FCSTD DOCUMENT  (FreeCAD 1.0R39285 (Git))
Label: suspendAssy_13.5m
License: All rights reserved
LicenseURL: https://en.wikipedia.org/wiki/All_rights_reserved
objects: Sketcher::SketchObject×102, Part::FeaturePython×96, Part::Extrusion×79, App::Part×45, Part::Cut×31, Part::Feature×27, Part::Compound×20, Part::Mirroring×18, Spreadsheet::Sheet×14, Part::Revolution×12, PartDesign::Body×9, Part::MultiFuse×9, Part::Sweep×8, PartDesign::Revolution×7, Part::Cylinder×5, PartDesign::Pad×4, Part::Part2DObjectPython×4, PartDesign::Pocket×3, PartDesign::ShapeBinder×3, PartDesign::PolarPattern×1, +4 more types
note: 552 computed .brp shape members not serialized (recipe doc carries the construction recipe); baked Part::Feature solids carry a one-line shape summary decoded from their .brp

FEATURE [PartDesign::Body] Body  label="ainShaftBerg"
  AllowCompound = false
  Origin = -> Origin001
FEATURE [Sketcher::SketchObject] Sketch
  ArcFitTolerance = 0
  AttachmentSupport = -> [XZ_Plane001]
  FullyConstrained = true
  MakeInternals = false
  MapMode = 5
  Placement = pos=(0,0,0) rot=(1,0,0;1.5708rad)
  sketch-geometry (6):
    g0: LineSegment StartX=0 StartY=0 StartZ=0 EndX=120 EndY=0 EndZ=0
    g1: LineSegment StartX=120 StartY=0 StartZ=0 EndX=120 EndY=16 EndZ=0
    g2: LineSegment StartX=120 StartY=16 StartZ=0 EndX=40 EndY=16 EndZ=0
    g3: LineSegment StartX=40 StartY=16 StartZ=0 EndX=40 EndY=120 EndZ=0
    g4: LineSegment StartX=40 StartY=120 StartZ=0 EndX=0 EndY=120 EndZ=0
    g5: LineSegment StartX=0 StartY=120 StartZ=0 EndX=0 EndY=0 EndZ=0
  constraints (17):
    c: Coincident(g-1,g0)
    c: Horizontal(g0)
    c: Coincident(g0,g1)
    c: Vertical(g1)
    c: Coincident(g1,g2)
    c: Horizontal(g2)
    c: Coincident(g2,g3)
    c: Vertical(g3)
    c: Coincident(g3,g4)
    c: Horizontal(g4)
    c: Coincident(g4,g5)
    c: Coincident(g5,g0)
    c: Vertical(g5)
    c: DistanceX(g4,g4) = 40
    c: DistanceY(g1,g1) = 16
    c: DistanceX(g0,g0) = 120
    c: DistanceY(g5,g5) = 120
FEATURE [PartDesign::Revolution] Revolution
  Angle = 360
  Angle2 = 60
  Axis = (0,2e-16,1)
  Base = (0,0,0)
  Placement = pos=(0,0,0) rot=(1,0,0;1.5708rad)
  Profile = -> Sketch
  ReferenceAxis = -> Sketch [V_Axis]
  Reversed = true
  Suppressed = false
  Type = 0
FEATURE [Sketcher::SketchObject] Sketch001
  ArcFitTolerance = 0
  AttachmentSupport = -> [Revolution]
  FullyConstrained = true
  MakeInternals = false
  MapMode = 5
  Placement = pos=(0,7e-15,16) rot=(0,0,1;3.14159rad)
  sketch-geometry (1):
    g0: Circle CenterX=90 CenterY=0 CenterZ=0 NormalX=0 NormalY=0 NormalZ=1 AngleXU=0 Radius=9.5
  constraints (3):
    c: PointOnObject(g0,g-1)
    c: Diameter(g0) = 19
    c: DistanceX(g-1,g0) = 90
FEATURE [Part::Extrusion] Extrude
  Base = -> Sketch001
  Dir = (0,0,1)
  DirMode = 2
  FaceMakerClass = Part::FaceMakerBullseye
  FaceMakerMode = 3
  LengthFwd = 30
  LengthRev = 0
  Reversed = true
  Solid = true
  Symmetric = false
FEATURE [Part::FeaturePython] Array  # Draft array (typed FeaturePython)
  Angle = 360
  ArrayType = 1
  Axis = (0,0,1)
  Base = -> Extrude
  Center = (0,0,0)
  Count = 4
  Fuse = false
  IntervalAxis = (0,0,0)
  IntervalX = (50,0,0)
  IntervalY = (0,50,0)
  IntervalZ = (0,0,50)
  NumberCircles = 3
  NumberPolar = 4
  NumberX = 2
  NumberY = 2
  NumberZ = 1
  RadialDistance = 50
  Symmetry = 1
  TangentialDistance = 25
FEATURE [Part::Cut] Cut
  Base = -> Revolution
  Tool = -> Array
FEATURE [App::Part] Part001  label="mainShaftBrg"
  Group = -> [Body,Extrude,Array,Revolution,Sketch001,Sketch,Cut]
  Origin = -> Origin002
  Placement = pos=(0,0,0) rot=(0,0,1;0.785398rad)
  mass = 9.64324
FEATURE [Sketcher::SketchObject] Sketch014
  ArcFitTolerance = 0
  FullyConstrained = true
  MakeInternals = false
  Placement = pos=(0,0,0) rot=(1,0,0;1.5708rad)
  expr: Constraints[11] = Spreadsheet001.dia / 2 - 460
  sketch-geometry (4):
    g0: LineSegment StartX=6285 StartY=0 StartZ=0 EndX=6290 EndY=0 EndZ=0
    g1: LineSegment StartX=6290 StartY=0 StartZ=0 EndX=6290 EndY=250 EndZ=0
    g2: LineSegment StartX=6290 StartY=250 StartZ=0 EndX=6285 EndY=250 EndZ=0
    g3: LineSegment StartX=6285 StartY=250 StartZ=0 EndX=6285 EndY=0 EndZ=0
  constraints (12):
    c: Coincident(g0,g1)
    c: Coincident(g1,g2)
    c: Coincident(g2,g3)
    c: Coincident(g3,g0)
    c: Horizontal(g0)
    c: Horizontal(g2)
    c: Vertical(g1)
    c: Vertical(g3)
    c: PointOnObject(g0,g-1)
    c: Distance(g2) = 5
    c: DistanceY(g1,g1) = 250
    c: DistanceX(g-1,g0) = 6290
FEATURE [Part::Revolution] Revolve
  Angle = 360
  Axis = (0,0,1)
  Base = (0,0,0)
  FaceMakerClass = Part::FaceMakerBullseye
  Solid = true
  Source = -> Sketch014
  Symmetric = false
FEATURE [Sketcher::SketchObject] Sketch015
  ArcFitTolerance = 0
  FullyConstrained = true
  MakeInternals = false
  Placement = pos=(0,0,0) rot=(1,0,0;1.5708rad)
  sketch-geometry (3):
    g0: LineSegment StartX=-70 StartY=250 StartZ=0 EndX=70 EndY=250 EndZ=0
    g1: LineSegment StartX=70 StartY=250 StartZ=0 EndX=0 EndY=180 EndZ=0
    g2: LineSegment StartX=0 StartY=180 StartZ=0 EndX=-70 EndY=250 EndZ=0
  constraints (9):
    c: Horizontal(g0)
    c: Coincident(g0,g1)
    c: PointOnObject(g1,g-2)
    c: Coincident(g1,g2)
    c: Coincident(g2,g0)
    c: Angle(g1,g2) = 1.5708
    c: PointOnObject(g0,g-3)
    c: DistanceY(g1,g0) = 70
    c: Angle(g2,g-2) = 2.35619
FEATURE [Part::Extrusion] Extrude006  label="Extrude007"
  Base = -> Sketch015
  Dir = (0,-1,2e-16)
  DirMode = 2
  FaceMakerClass = Part::FaceMakerBullseye
  FaceMakerMode = 3
  LengthFwd = 10000
  LengthRev = 0
  Solid = true
  Symmetric = false
FEATURE [Part::FeaturePython] Array002  # Draft array (typed FeaturePython)
  AlwaysSyncPlacement = false
  Angle = 360
  ArrayType = 1
  Axis = (0,0,1)
  Base = -> Extrude006
  Center = (0,0,0)
  Count = 245
  ExpandArray = false
  Fuse = false
  IntervalAxis = (0,0,0)
  IntervalX = (50,0,0)
  IntervalY = (0,50,0)
  IntervalZ = (0,0,50)
  NumberCircles = 3
  NumberPolar = 245
  NumberX = 2
  NumberY = 2
  NumberZ = 1
  PlacementList = 245 placements: [(0,0,0),(0,0,0),(0,0,0),(0,0,0),(0,0,0),(0,0,0),(0,0,0),(0,0,0),(0,0,0),(0,0,0),(0,0,0),(0,0,0),(0,0,0),(0,0,0),(0,0,0),(0,0,0),(0,0,0),(0,0,0),(0,0,0),(0,0,0),(0,0,0),(0,0,0),(0,0,0),(0,0,0),(0,0,0),(0,0,0),(0,0,0),(0,0,0),(0,0,0),(0,0,0),(0,0,0),(0,0,0),(0,0,0),(0,0,0),(0,0,0),(0,0,0),(0,0,0),(0,0,0),(0,0,0),(0,0,0),(0,0,0),(0,0,0),(0,0,0),(0,0,0),(0,0,0),(0,0,0),(0,0,0),(0,0,0),(0,0,0),(0,0,0),+195 more]
  RadialDistance = 50
  Symmetry = 1
  TangentialDistance = 25
  expr: NumberPolar = Spreadsheet001.dia / 55
FEATURE [Part::Cut] Cut001  label="weir"
  Base = -> Revolve
  Tool = -> Array002
FEATURE [Sketcher::SketchObject] Sketch016
  ArcFitTolerance = 0
  FullyConstrained = true
  MakeInternals = false
  Placement = pos=(0,0,0) rot=(1,0,0;1.5708rad)
  expr: .Constraints.h0 = Spreadsheet001.h0
  expr: Constraints[11] = Spreadsheet001.dia / 2 - (450 + 300)
  sketch-geometry (4):
    g0: LineSegment StartX=5995 StartY=80 StartZ=0 EndX=6000 EndY=80 EndZ=0
    g1: LineSegment StartX=6000 StartY=80 StartZ=0 EndX=6000 EndY=380 EndZ=0
    g2: LineSegment StartX=6000 StartY=380 StartZ=0 EndX=5995 EndY=380 EndZ=0
    g3: LineSegment StartX=5995 StartY=380 StartZ=0 EndX=5995 EndY=80 EndZ=0
  constraints (12):
    c: Coincident(g0,g1)
    c: Coincident(g1,g2)
    c: Coincident(g2,g3)
    c: Coincident(g3,g0)
    c: Horizontal(g0)
    c: Horizontal(g2)
    c: Vertical(g1)
    c: Vertical(g3)
    c: DistanceX(g2,g2) = 5
    c: DistanceY(g1,g1) = 300  'h0'
    c: DistanceY(g-3,g1) = 130
    c: Distance(g1,g-2) = 6000
FEATURE [Part::Revolution] Revolve001
  Angle = 360
  Axis = (0,0,1)
  Base = (0,0,0)
  FaceMakerClass = Part::FaceMakerBullseye
  Solid = true
  Source = -> Sketch016
  Symmetric = false
FEATURE [Part::FeaturePython] AngleSteel001  # WARN: FeaturePython — macro-defined, semantics opaque (R4)
  A = 50
  B = 50
  L = 1000
  Placement = pos=(6000,0,474) rot=(0,1,0;1.5708rad)
  Solid = false
  g0 = 7.85
  mass = 0
  size = 7
  standard = SS_Equal
  t = 6
  expr: .Placement.Base.x = Spreadsheet001.dia / 2 - 750
FEATURE [Part::Revolution] Revolve002
  Angle = 360
  Axis = (0,0,1)
  Base = (0,0,0)
  FaceMakerClass = Part::FaceMakerBullseye
  Placement = pos=(0,0,-94) rot=(0,0,1;0rad)
  Solid = false
  Source = -> AngleSteel001
  Symmetric = false
FEATURE [Sketcher::SketchObject] Sketch017
  ArcFitTolerance = 0
  FullyConstrained = true
  MakeInternals = false
  Placement = pos=(0,0,0) rot=(1,0,0;1.5708rad)
  expr: Constraints[10] = Spreadsheet001.dia / 2 - (460 + 290)
  sketch-geometry (4):
    g0: LineSegment StartX=6000 StartY=80 StartZ=0 EndX=6290 EndY=-163.339 EndZ=0
    g1: LineSegment StartX=6290 StartY=-163.339 StartZ=0 EndX=6290 EndY=-6.69002 EndZ=0
    g2: LineSegment StartX=6290 StartY=-6.69002 StartZ=0 EndX=6000 EndY=236.649 EndZ=0
    g3: LineSegment StartX=6000 StartY=236.649 StartZ=0 EndX=6000 EndY=80 EndZ=0
  constraints (12):
    c: Coincident(g0,g1)
    c: Vertical(g1)
    c: Coincident(g1,g2)
    c: Coincident(g2,g3)
    c: Coincident(g3,g0)
    c: Vertical(g3)
    c: Parallel(g2,g0)
    c: DistanceX(g0,g0) = 290
    c: Distance(g1,g0) = 120
    c: Angle(g0,g3) = 2.26893
    c: Distance(g0,g-2) = 6000
    c: Distance(g0,g-1) = 80
FEATURE [Part::Extrusion] Extrude007  label="Extrude008"
  Base = -> Sketch017
  Dir = (0,-1,2e-16)
  DirMode = 2
  FaceMakerClass = Part::FaceMakerBullseye
  FaceMakerMode = 3
  LengthFwd = 6
  LengthRev = 0
  Solid = true
  Symmetric = true
FEATURE [Spreadsheet::Sheet] Spreadsheet001
  cells = A3='tankDia dia; B3(dia)=13500; A4='waterWay width; B4(W0)=450; A5='nonber of support; B5(n)=12; A6='buffleHight  h0; B6(h0)=300
FEATURE [Part::FeaturePython] AngleSteel002  # WARN: FeaturePython — macro-defined, semantics opaque (R4)
  A = 50
  B = 50
  L = 140
  Placement = pos=(6265,28,-150) rot=(0,0,1;3.14159rad)
  Solid = true
  g0 = 7.85
  mass = 0.620249
  size = 7
  standard = SS_Equal
  t = 6
  expr: .Placement.Base.x = Spreadsheet001.dia / 2 - 485
FEATURE [Part::Mirroring] Mirror002  label="AngleSteel001 (mirrored)"
  Base = (4800,0,0)
  Normal = (0,-1,0)
  Source = -> AngleSteel002
FEATURE [Part::Compound] Compound003  label="support"
  Links = -> [AngleSteel002,Mirror002,Extrude007]
FEATURE [Part::FeaturePython] Array003  label="Array001"  # Draft array (typed FeaturePython)
  AlwaysSyncPlacement = false
  Angle = 360
  ArrayType = 1
  Axis = (0,0,1)
  Base = -> Compound003
  Center = (0,0,0)
  Count = 12
  ExpandArray = false
  Fuse = false
  IntervalAxis = (0,0,0)
  IntervalX = (50,0,0)
  IntervalY = (0,50,0)
  IntervalZ = (0,0,50)
  NumberCircles = 3
  NumberPolar = 12
  NumberX = 2
  NumberY = 2
  NumberZ = 1
  PlacementList = 12 placements: [(0,0,0),(0,0,0),(0,0,0),(0,0,0),(0,0,0),(0,0,0),(0,0,0),(0,0,0),(0,0,0),(0,0,0),(0,0,0),(0,0,0)]
  RadialDistance = 50
  ScaleList = (12) [(1,1,1),(1,1,1),(1,1,1),(1,1,1),(1,1,1),(1,1,1),(1,1,1),(1,1,1),(1,1,1),(1,1,1),(1,1,1),(1,1,1)]
  Symmetry = 1
  TangentialDistance = 25
  expr: NumberPolar = Spreadsheet001.n
FEATURE [Part::Compound] Compound004  label="body"
  Links = -> [Revolve001,Revolve002]
  Placement = pos=(0,0,-50) rot=(0,0,1;0rad)
FEATURE [Part::FeaturePython] SquarePipe  # WARN: FeaturePython — macro-defined, semantics opaque (R4)
  A = 125
  B = 125
  L = 5830
  Placement = pos=(0,0,0) rot=(0,-1,0;1.5708rad)
  Solid = true
  g0 = 7.85
  mass = 106.891
  size = 39
  standard = SS
  t = 1
  expr: L = Spreadsheet002.L0
FEATURE [Sketcher::SketchObject] Sketch018
  ArcFitTolerance = 0
  AttachmentSupport = -> [SquarePipe]
  ExternalGeometry = -> [SquarePipe]
  FullyConstrained = true
  MakeInternals = false
  MapMode = 5
  Placement = pos=(-5830,0,0) rot=(0,-1,0;1.5708rad)
  sketch-geometry (4):
    g0: LineSegment StartX=-62.5 StartY=-62.5 StartZ=0 EndX=62.5 EndY=-62.5 EndZ=0
    g1: LineSegment StartX=62.5 StartY=-62.5 StartZ=0 EndX=62.5 EndY=62.5 EndZ=0
    g2: LineSegment StartX=62.5 StartY=62.5 StartZ=0 EndX=-62.5 EndY=62.5 EndZ=0
    g3: LineSegment StartX=-62.5 StartY=62.5 StartZ=0 EndX=-62.5 EndY=-62.5 EndZ=0
  constraints (11):
    c: Coincident(g0,g1)
    c: Coincident(g1,g2)
    c: Coincident(g2,g3)
    c: Coincident(g3,g0)
    c: Horizontal(g0)
    c: Horizontal(g2)
    c: Vertical(g3)
    c: DistanceX(g2,g2) = 125
    c: Equal(g1,g0)
    c: PointOnObject(g-4,g2)
    c: Tangent(g-3,g1) = -1.5708
FEATURE [Part::Extrusion] Extrude008  label="Extrude009"
  Base = -> Sketch018
  Dir = (-1,0,2e-16)
  DirMode = 2
  FaceMakerClass = Part::FaceMakerBullseye
  FaceMakerMode = 3
  LengthFwd = 6
  LengthRev = 0
  Solid = true
  Symmetric = false
FEATURE [Part::FeaturePython] Clone001  label="Extrude010"  # Draft clone (typed FeaturePython)
  AttacherType = Attacher::AttachEngine3D
  Fuse = false
  Objects = -> [Extrude008]
  Placement = pos=(5836,0,0) rot=(0,0,1;0rad)
  Scale = (1,1,1)
  expr: .Placement.Base.x = Spreadsheet002.L0 + 6
FEATURE [Spreadsheet::Sheet] Spreadsheet002
  cells = A1='tankDia   D0; B1(D0)=13500; A2='buffle Position; B2(bp)=920; A3='beamLength L; B3(L0)==D0 / 2 - bp; A4='bradeWidth W0; B4(W0)==w1 * n0; A5='brade      n0; B5(n0)=5; A6='brade     w1; B6(w1)=900
FEATURE [Sketcher::SketchObject] Sketch019  label="skimmerBrade01"
  ArcFitTolerance = 0
  FullyConstrained = true
  MakeInternals = false
  Placement = pos=(0,0,0) rot=(1,0,0;1.5708rad)
  sketch-geometry (7):
    g0: LineSegment StartX=6 StartY=62.5 StartZ=0 EndX=36 EndY=62.5 EndZ=0
    g1: LineSegment StartX=36 StartY=62.5 StartZ=0 EndX=100.694 EndY=26.1551 EndZ=0
    g2: ArcOfCircle CenterX=86 CenterY=0 CenterZ=0 NormalX=0 NormalY=0 NormalZ=1 AngleXU=0 Radius=30 StartAngle=5.22424 EndAngle=7.34213
    g3: LineSegment StartX=100.694 StartY=-26.1551 StartZ=0 EndX=36 EndY=-62.5 EndZ=0
    g4: LineSegment StartX=36 StartY=-62.5 StartZ=0 EndX=6 EndY=-62.5 EndZ=0
    g5: LineSegment StartX=6 StartY=-62.5 StartZ=0 EndX=6 EndY=62.5 EndZ=0
    g6: Circle CenterX=86 CenterY=0 CenterZ=0 NormalX=0 NormalY=0 NormalZ=1 AngleXU=0 Radius=13
  constraints (17):
    c: Horizontal(g0)
    c: Coincident(g0,g1)
    c: Tangent(g1,g2) = 1.5708
    c: Coincident(g3,g4)
    c: Coincident(g4,g5)
    c: Coincident(g5,g0)
    c: PointOnObject(g6,g-1)
    c: Coincident(g0,g-3)
    c: Coincident(g4,g-3)
    c: Horizontal(g4)
    c: DistanceX(g0,g0) = 30
    c: Equal(g0,g4)
    c: Coincident(g2,g6)
    c: DistanceX(g4,g2) = 80
    c: Diameter(g6) = 26
    c: Radius(g2) = 30
    c: Tangent(g2,g3) = 1.5708
FEATURE [Sketcher::SketchObject] Sketch020
  ArcFitTolerance = 0
  FullyConstrained = false
  MakeInternals = false
  Placement = pos=(0,0,0) rot=(1,0,0;1.5708rad)
  sketch-geometry (7):
    g0: ArcOfCircle CenterX=81.7032 CenterY=0 CenterZ=0 NormalX=0 NormalY=0 NormalZ=1 AngleXU=0 Radius=30 StartAngle=2.05435 EndAngle=4.1734
    g1: LineSegment StartX=67.7553 StartY=26.5604 StartZ=0 EndX=131.703 EndY=60.1419 EndZ=0
    g2: LineSegment StartX=131.703 StartY=60.1419 StartZ=0 EndX=161.703 EndY=60.1419 EndZ=0
    g3: LineSegment StartX=161.703 StartY=60.1419 StartZ=0 EndX=161.703 EndY=-64.8581 EndZ=0
    g4: LineSegment StartX=161.703 StartY=-64.8581 StartZ=0 EndX=131.703 EndY=-64.8581 EndZ=0
    g5: LineSegment StartX=131.703 StartY=-64.8581 StartZ=0 EndX=66.3053 EndY=-25.7469 EndZ=0
    g6: Circle CenterX=81.7032 CenterY=0 CenterZ=0 NormalX=0 NormalY=0 NormalZ=1 AngleXU=0 Radius=13
  constraints (17):
    c: PointOnObject(g0,g-1)
    c: Coincident(g1,g2)
    c: Horizontal(g2)
    c: Coincident(g2,g3)
    c: Coincident(g3,g4)
    c: Coincident(g4,g5)
    c: Tangent(g0,g5) = 1.5708
    c: Tangent(g0,g1) = 1.5708
    c: Vertical(g3)
    c: Distance(g0,g3) = 80
    c: Horizontal(g4)
    c: DistanceX(g2,g2) = 30
    c: Equal(g2,g4)
    c: Radius(g0) = 30
    c: Coincident(g6,g0)
    c: Diameter(g6) = 26
    c: DistanceY(g3,g3) = 125
FEATURE [Part::Extrusion] Extrude009  label="Extrude011"
  Base = -> Sketch020
  Dir = (0,-1,2e-16)
  DirMode = 2
  FaceMakerClass = Part::FaceMakerBullseye
  FaceMakerMode = 3
  LengthFwd = 6
  LengthRev = 0
  Placement = pos=(0,9,0) rot=(0,0,1;0rad)
  Solid = true
  Symmetric = true
FEATURE [Sketcher::SketchObject] Sketch021
  ArcFitTolerance = 0
  AttachmentSupport = -> [Extrude009]
  ExternalGeometry = -> [Extrude009]
  FullyConstrained = false
  MakeInternals = false
  MapMode = 5
  Placement = pos=(161.703,9,0) rot=(0.57735,0.57735,0.57735;2.0944rad)
  sketch-geometry (4):
    g0: LineSegment StartX=-59 StartY=-64.8581 StartZ=0 EndX=41 EndY=-64.8581 EndZ=0
    g1: LineSegment StartX=41 StartY=-64.8581 StartZ=0 EndX=41 EndY=60.1419 EndZ=0
    g2: LineSegment StartX=41 StartY=60.1419 StartZ=0 EndX=-59 EndY=60.1419 EndZ=0
    g3: LineSegment StartX=-59 StartY=60.1419 StartZ=0 EndX=-59 EndY=-64.8581 EndZ=0
  constraints (8):
    c: Coincident(g0,g3)
    c: Coincident(g2,g3)
    c: Coincident(g0,g1)
    c: Coincident(g1,g2)
    c: DistanceY(g1,g1) = 125
    c: Horizontal(g2)
    c: Horizontal(g0)
    c: PointOnObject(g-3,g2)
FEATURE [Part::Extrusion] Extrude010  label="Extrude012"
  Base = -> Sketch021
  Dir = (1,0,0)
  DirMode = 2
  FaceMakerClass = Part::FaceMakerBullseye
  FaceMakerMode = 3
  LengthFwd = 10
  LengthRev = 0
  Solid = true
  Symmetric = false
FEATURE [Part::Feature] Part__Feature001  label="CNROK75-U_b"
  shape: bbox 47.01 x 65.51 x 70.01 mm, 58 faces (baked)
FEATURE [Part::Feature] Part__Feature002  label="CNROK75-U_w"
  shape: bbox 41.3 x 78.6 x 78.6 mm, 86 faces (baked)
FEATURE [App::Part] CNROK75_U  label="CNROK75-U"
  Group = -> [Part__Feature001,Part__Feature002]
  Origin = -> Origin012
  Placement = pos=(-5780,2.9e-14,-118.52) rot=(1,0,0;1.5708rad)
  expr: .Placement.Base.x = -Spreadsheet002.L0 + 50
FEATURE [Part::FeaturePython] Clone002  label="Extrude013"  # Draft clone (typed FeaturePython)
  AttacherType = Attacher::AttachEngine3D
  Fuse = false
  Objects = -> [Extrude009]
  Placement = pos=(0,-9,0) rot=(0,0,1;0rad)
  Scale = (1,1,1)
FEATURE [App::Part] Part006  label="gusset"
  Group = -> [Sketch020,Sketch021,Extrude009,Extrude010,Clone002]
  Origin = -> Origin010
  Placement = pos=(178,-2.13e-14,0) rot=(0,0,1;3.14159rad)
FEATURE [Part::Feature] Part__Feature003  label="HNS3L_1"
  shape: bbox 64 x 7.5 x 21.75 mm, 15 faces (baked)
FEATURE [Part::Feature] Part__Feature004  label="HNS3L_2"
  shape: bbox 64 x 7.5 x 21.75 mm, 12 faces (baked)
FEATURE [App::Part] HNS3L
  Group = -> [Part__Feature003,Part__Feature004]
  Origin = -> Origin013
  Placement = pos=(-400,-8,115) rot=(1,0,0;3.14159rad)
  expr: .Placement.Base.x = -Spreadsheet002.w1 / 2 + 50
FEATURE [Sketcher::SketchObject] Sketch022
  ArcFitTolerance = 0
  FullyConstrained = true
  MakeInternals = false
  Placement = pos=(0,0,0) rot=(1,0,0;1.5708rad)
  expr: Constraints[10] = Spreadsheet002.w1
  sketch-geometry (5):
    g0: LineSegment StartX=-450 StartY=-107.5 StartZ=0 EndX=-450 EndY=107.5 EndZ=0
    g1: LineSegment StartX=-450 StartY=107.5 StartZ=0 EndX=450 EndY=107.5 EndZ=0
    g2: LineSegment StartX=450 StartY=107.5 StartZ=0 EndX=450 EndY=-107.5 EndZ=0
    g3: LineSegment StartX=450 StartY=-107.5 StartZ=0 EndX=-450 EndY=-107.5 EndZ=0
    g4: GeomPoint [constr] X=0 Y=0 Z=0
  constraints (12):
    c: Coincident(g0,g1)
    c: Coincident(g1,g2)
    c: Coincident(g2,g3)
    c: Coincident(g3,g0)
    c: Horizontal(g1)
    c: Horizontal(g3)
    c: Vertical(g0)
    c: Vertical(g2)
    c: Symmetric(g1,g0,g4)
    c: Coincident(g4,g-1)
    c: Distance(g1) = 900
    c: DistanceY(g2,g2) = 215
FEATURE [Part::Extrusion] Extrude011  label="Extrude014"
  Base = -> Sketch022
  Dir = (0,-1,2e-16)
  DirMode = 2
  FaceMakerClass = Part::FaceMakerBullseye
  FaceMakerMode = 3
  LengthFwd = 5
  LengthRev = 0
  Placement = pos=(0,-4.5,-12) rot=(0,0,1;0rad)
  Solid = true
  Symmetric = false
FEATURE [Part::FeaturePython] Clone003  label="HNS3L001"  # Draft clone (typed FeaturePython)
  AttacherType = Attacher::AttachEngine3D
  Fuse = false
  Objects = -> [HNS3L]
  Placement = pos=(336,-8,115) rot=(1,0,0;3.14159rad)
  Scale = (1,1,1)
  expr: .Placement.Base.x = Spreadsheet002.w1 / 2 - 114
FEATURE [Sketcher::SketchObject] Sketch023
  ArcFitTolerance = 0
  FullyConstrained = true
  MakeInternals = false
  Placement = pos=(0,0,0) rot=(1,0,0;1.5708rad)
  expr: Constraints[11] = Spreadsheet002.w1
  sketch-geometry (5):
    g0: LineSegment StartX=-450 StartY=-37.5 StartZ=0 EndX=-450 EndY=37.5 EndZ=0
    g1: LineSegment StartX=-450 StartY=37.5 StartZ=0 EndX=450 EndY=37.5 EndZ=0
    g2: LineSegment StartX=450 StartY=37.5 StartZ=0 EndX=450 EndY=-37.5 EndZ=0
    g3: LineSegment StartX=450 StartY=-37.5 StartZ=0 EndX=-450 EndY=-37.5 EndZ=0
    g4: GeomPoint [constr] X=0 Y=0 Z=0
  constraints (12):
    c: Coincident(g0,g1)
    c: Coincident(g1,g2)
    c: Coincident(g2,g3)
    c: Coincident(g3,g0)
    c: Horizontal(g1)
    c: Horizontal(g3)
    c: Vertical(g0)
    c: Vertical(g2)
    c: Symmetric(g1,g0,g4)
    c: Coincident(g4,g-1)
    c: DistanceY(g2,g2) = 75
    c: DistanceX(g3,g3) = 900
FEATURE [Part::Extrusion] Extrude012  label="Extrude015"
  Base = -> Sketch023
  Dir = (0,-1,2e-16)
  DirMode = 2
  FaceMakerClass = Part::FaceMakerBullseye
  FaceMakerMode = 3
  LengthFwd = 3
  LengthRev = 0
  Placement = pos=(0,-9.5,70) rot=(0,0,1;0rad)
  Solid = true
  Symmetric = false
FEATURE [Sketcher::SketchObject] Sketch024
  ArcFitTolerance = 0
  AttachmentSupport = -> [Extrude011]
  FullyConstrained = true
  MakeInternals = false
  MapMode = 5
  Placement = pos=(-450,-4.5,-12) rot=(0.57735,-0.57735,-0.57735;2.0944rad)
  sketch-geometry (4):
    g0: LineSegment StartX=2.4e-14 StartY=107.5 StartZ=0 EndX=-3 EndY=107.5 EndZ=0
    g1: LineSegment StartX=-3 StartY=107.5 StartZ=0 EndX=-3 EndY=44.5 EndZ=0
    g2: LineSegment StartX=-3 StartY=44.5 StartZ=0 EndX=2.4e-14 EndY=44.5 EndZ=0
    g3: LineSegment StartX=2.4e-14 StartY=44.5 StartZ=0 EndX=2.4e-14 EndY=107.5 EndZ=0
  constraints (11):
    c: Coincident(g0,g1)
    c: Coincident(g1,g2)
    c: Coincident(g2,g3)
    c: Coincident(g3,g0)
    c: Horizontal(g0)
    c: Horizontal(g2)
    c: Vertical(g1)
    c: Vertical(g3)
    c: DistanceX(g0,g0) = 3
    c: Coincident(g0,g-3)
    c: Horizontal(g1,g-4)
FEATURE [Part::Extrusion] Extrude013  label="Extrude016"
  Base = -> Sketch024
  Dir = (-1,0,0)
  DirMode = 2
  FaceMakerClass = Part::FaceMakerBullseye
  FaceMakerMode = 3
  LengthFwd = 900
  LengthRev = 0
  Reversed = true
  Solid = true
  Symmetric = false
  expr: LengthFwd = Spreadsheet002.w1
FEATURE [Sketcher::SketchObject] Sketch025
  ArcFitTolerance = 0
  AttachmentSupport = -> [Extrude011]
  FullyConstrained = false
  MakeInternals = false
  MapMode = 5
  Placement = pos=(-450,-4.5,-12) rot=(0.57735,-0.57735,-0.57735;2.0944rad)
  sketch-geometry (8):
    g0: LineSegment StartX=-104.645 StartY=156.908 StartZ=0 EndX=-4.64507 EndY=156.908 EndZ=0
    g1: LineSegment StartX=3.35493 StartY=148.908 StartZ=0 EndX=3.35493 EndY=130.908 EndZ=0
    g2: LineSegment StartX=3.35493 StartY=130.908 StartZ=0 EndX=0.354931 EndY=130.908 EndZ=0
    g3: LineSegment StartX=0.354931 StartY=130.908 StartZ=0 EndX=0.354931 EndY=148.908 EndZ=0
    g4: LineSegment StartX=-4.64507 StartY=153.908 StartZ=0 EndX=-104.645 EndY=153.908 EndZ=0
    g5: LineSegment StartX=-104.645 StartY=153.908 StartZ=0 EndX=-104.645 EndY=156.908 EndZ=0
    g6: ArcOfCircle CenterX=-4.64507 CenterY=148.908 CenterZ=0 NormalX=0 NormalY=0 NormalZ=1 AngleXU=0 Radius=5 StartAngle=3.3e-15 EndAngle=1.5708
    g7: ArcOfCircle CenterX=-4.64507 CenterY=148.908 CenterZ=0 NormalX=0 NormalY=0 NormalZ=1 AngleXU=0 Radius=8 StartAngle=-1.8e-15 EndAngle=1.5708
  constraints (19):
    c: Horizontal(g0)
    c: Vertical(g1)
    c: Coincident(g1,g2)
    c: Horizontal(g2)
    c: Coincident(g2,g3)
    c: Vertical(g3)
    c: Horizontal(g4)
    c: Coincident(g4,g5)
    c: Coincident(g5,g0)
    c: Vertical(g5)
    c: DistanceX(g2,g2) = 3
    c: Tangent(g3,g6) = -1.5708
    c: Tangent(g4,g6) = -1.5708
    c: Tangent(g1,g7) = 1.5708
    c: Tangent(g0,g7) = 1.5708
    c: Coincident(g6,g7)
    c: DistanceX(g4,g4) = 100
    c: DistanceY(g3,g3) = 18
    c: Radius(g6) = 5
FEATURE [Part::Extrusion] Extrude014  label="Extrude017"
  Base = -> Sketch025
  Dir = (-1,0,0)
  DirMode = 2
  FaceMakerClass = Part::FaceMakerBullseye
  FaceMakerMode = 3
  LengthFwd = 80
  LengthRev = 0
  Placement = pos=(42.5,0,0) rot=(0,0,1;0rad)
  Reversed = true
  Solid = true
  Symmetric = false
FEATURE [Part::FeaturePython] Clone004  label="Extrude018"  # Draft clone (typed FeaturePython)
  AttacherType = Attacher::AttachEngine3D
  Fuse = false
  Objects = -> [Extrude014]
  Placement = pos=(770,0,0) rot=(0,0,1;0rad)
  Scale = (1,1,1)
  expr: .Placement.Base.x = Spreadsheet002.w1 - (50 + 46 + 34)
FEATURE [App::Part] Part008  label="brade"
  Group = -> [Sketch022,Extrude011,Clone003,HNS3L,Sketch023,Extrude012,Sketch024,Extrude013,Sketch025,Extrude014,Clone004]
  Origin = -> Origin014
  Placement = pos=(-5270,-100,-207.547) rot=(0,0,1;0rad)
  expr: .Placement.Base.x = -Spreadsheet002.L0 + 560
FEATURE [Part::FeaturePython] Array004  label="brade001"  # Draft array (typed FeaturePython)
  AlwaysSyncPlacement = false
  Angle = 360
  ArrayType = 0
  Axis = (0,0,1)
  Base = -> Part008
  Center = (0,0,0)
  Count = 5
  ExpandArray = false
  Fuse = false
  IntervalAxis = (0,0,0)
  IntervalX = (900,0,0)
  IntervalY = (0,100,0)
  IntervalZ = (0,0,100)
  NumberCircles = 3
  NumberPolar = 5
  NumberX = 5
  NumberY = 1
  NumberZ = 1
  PlacementList = 5 placements: arithmetic series from (-5270,-100,-207.547) step (900,0,0) to (-1670,-100,-207.547)
  RadialDistance = 50
  ScaleList = (5) [(1,1,1),(1,1,1),(1,1,1),(1,1,1),(1,1,1)]
  Symmetry = 1
  TangentialDistance = 25
  expr: .IntervalX.x = Spreadsheet002.w1
  expr: NumberX = Spreadsheet002.n0
FEATURE [Part::FeaturePython] ChannelSteel  # WARN: FeaturePython — macro-defined, semantics opaque (R4)
  B = 75
  H = 150
  L = 1000
  Placement = pos=(176,0,-75) rot=(0,0,1;0rad)
  Solid = false
  g0 = 7.85
  mass = 0
  size = 3
  standard = SS
  t1 = 6.5
  t2 = 10
FEATURE [Sketcher::SketchObject] Sketch026
  ArcFitTolerance = 0
  FullyConstrained = true
  MakeInternals = false
  MapMode = 5
  Placement = pos=(0,0,62.5) rot=(0,0,1;0rad)
  sketch-geometry (6):
    g0: LineSegment StartX=-2985 StartY=62.5 StartZ=0 EndX=-2985 EndY=112.5 EndZ=0
    g1: ArcOfCircle CenterX=-3000 CenterY=112.5 CenterZ=0 NormalX=0 NormalY=0 NormalZ=1 AngleXU=0 Radius=15 StartAngle=0 EndAngle=1.98689
    g2: LineSegment StartX=-3006.06 StartY=126.22 StartZ=0 EndX=-3105 EndY=82.5 EndZ=0
    g3: LineSegment StartX=-3105 StartY=82.5 StartZ=0 EndX=-3105 EndY=62.5 EndZ=0
    g4: LineSegment StartX=-3105 StartY=62.5 StartZ=0 EndX=-2985 EndY=62.5 EndZ=0
    g5: Circle CenterX=-3000 CenterY=112.5 CenterZ=0 NormalX=0 NormalY=0 NormalZ=1 AngleXU=0 Radius=7.5
  constraints (16):
    c: Tangent(g0,g1) = -1.5708
    c: Coincident(g2,g3)
    c: Vertical(g3)
    c: Coincident(g3,g4)
    c: Coincident(g4,g0)
    c: Coincident(g5,g1)
    c: Diameter(g5) = 15
    c: Radius(g1) = 15
    c: Vertical(g0)
    c: Tangent(g1,g2) = -1.5708
    c: Horizontal(g4)
    c: DistanceY(g3,g3) = 20
    c: DistanceX(g4,g4) = 120
    c: DistanceY(g0,g1) = 50
    c: DistanceY(g-1,g0) = 62.5
    c: DistanceX(g-2,g1) = -3000
FEATURE [Part::Extrusion] Extrude017  label="Extrude020"
  Base = -> Sketch026
  Dir = (0,0,1)
  DirMode = 2
  FaceMakerClass = Part::FaceMakerBullseye
  FaceMakerMode = 3
  LengthFwd = 6
  LengthRev = 0
  Placement = pos=(0,0,-62.5) rot=(0,0,1;0rad)
  Solid = true
  Symmetric = true
FEATURE [Part::Mirroring] Mirror003  label="Extrude020 (mirrored)"
  Base = (-3100,0,0)
  Normal = (0,-1,0)
  Source = -> Extrude017
FEATURE [App::Part] Part005  label="hontai"
  Group = -> [Sketch019,Clone001,SquarePipe,Sketch018,Extrude008,Sketch026,Extrude017,Mirror003]
  Origin = -> Origin009
FEATURE [Part::Compound] Compound005  label="hontai001"
  Links = -> [Part005]
FEATURE [Sketcher::SketchObject] Sketch027  label="Sketch019"
  ArcFitTolerance = 0
  FullyConstrained = false
  MakeInternals = false
  MapMode = 5
  Placement = pos=(0,0,75) rot=(0,0,1;0rad)
  sketch-geometry (7):
    g0: LineSegment StartX=176 StartY=810 StartZ=0 EndX=156 EndY=810 EndZ=0
    g1: LineSegment StartX=156 StartY=810 StartZ=0 EndX=118.097 EndY=782.842 EndZ=0
    g2: ArcOfCircle CenterX=126 CenterY=771.812 CenterZ=0 NormalX=0 NormalY=0 NormalZ=1 AngleXU=0 Radius=13.569 StartAngle=2.19251 EndAngle=4.2132
    g3: LineSegment StartX=119.504 StartY=759.899 StartZ=0 EndX=156 EndY=740 EndZ=0
    g4: LineSegment StartX=156 StartY=740 StartZ=0 EndX=176 EndY=740 EndZ=0
    g5: LineSegment StartX=176 StartY=740 StartZ=0 EndX=176 EndY=810 EndZ=0
    g6: Circle CenterX=126 CenterY=771.812 CenterZ=0 NormalX=0 NormalY=0 NormalZ=1 AngleXU=0 Radius=7.5
  constraints (15):
    c: Horizontal(g0)
    c: Coincident(g0,g1)
    c: Tangent(g1,g2) = -1.5708
    c: Coincident(g3,g4)
    c: Horizontal(g4)
    c: Coincident(g4,g5)
    c: Coincident(g5,g0)
    c: Vertical(g5)
    c: Coincident(g6,g2)
    c: Diameter(g6) = 15
    c: DistanceY(g5,g5) = 70
    c: Tangent(g2,g3) = -1.5708
    c: Vertical(g0,g3)
    c: DistanceX(g0,g0) = 20
    c: Distance(g2,g5) = 50
FEATURE [Spreadsheet::Sheet] Spreadsheet003
  cells = A1='B; A2='rodDia dia; B2(dia)=12; C2='thickness; D2(t0)=6; A3='length L0; B3(L0)=3158; C3='l1; D3(l1)==L0 - (dia * 5 + lx); E3='lx; F3(lx)=150; B4='l; C4='l1; D4='a; E4='b; F4='c; G4='e; H4='f; I4='g; J4='h; K4='i; L4='r; A5='forkEndR; B5=80; D5=25; E5=10; F5=14; G5=16; H5=13; I5=40; J5=5; K5=13; L5=15; A6='turnBackle; B6=100; C6=20; D6=30; E6=16; F6=22; A7='forkEndL; B7=60; D7=25; E7=10; F7=13; G7=16; H7=13; I7=20; L7=15; A8=1; B8=2; C8=3; D8=4; E8=5; F8=6; G8=7; H8=8; I8=9; J8=10; K8=11; L8=12; A9='turnBackle; A10='d; B10='l; C10='l1; D10='a; E10='b; F10='c; G10='t0; A11=10; B11=75; C11=15; D11=24; E11=13; F11=17; G11=6; A12=12; B12=100; C12=20; D12=30; E12=16; F12=22; G12=6; A13=16; B13=125; C13=24; D13=36; E13=20; F13=27; G13=9; A14=20; B14=150; C14=28; D14=42; E14=23; F14=33; G14=9; A15=22; B15=175; C15=33; D15=48; E15=27; F15=37; G15=9; A16=24; B16=200; C16=38; D16=54; E16=30; F16=42; G16=12; A17=30; B17=250; C17=47; D17=66; E17=37; F17=52; G17=12; A18='forkEnd_L; A19='d; B19='l; C19='a; D19='b; E19='c; F19='e; G19='f; H19='g; I19='r; A20=10; B20=50; C20=20; D20=7; E20=10; F20=12; G20=10; H20=15; I20=12; A21=12; B21=60; C21=25; D21=10; E21=13; F21=16; G21=13; H21=20; I21=15; A22=16; B22=75; C22=30; D22=13; E22=16; F22=20; G22=16; H22=25; I22=19; A23=20; B23=90; C23=40; D23=16; E23=20; F23=24; G23=20; H23=30; I23=23; A24=22; B24=100; C24=45; D24=20; E24=23; F24=28; G24=23; H24=35; I24=27; A25=24; B25=115; C25=50; D25=23; E25=26; F25=32; G25=26; H25=40; I25=30; A26=30; B26=140; C26=65; D26=30; E26=33; F26=40; G26=33; H26=50; I26=38; A27='forkEnd_R; A28='d; B28='l; C28='a; D28='b; E28='c; F28='r; G28='e; H28='f; I28='g; +79 more cells
FEATURE [Sketcher::SketchObject] Sketch028
  ArcFitTolerance = 0
  FullyConstrained = true
  MakeInternals = false
  Placement = pos=(0,0,0) rot=(1,0,0;1.5708rad)
  expr: Constraints[11] = Spreadsheet003.I5 + Spreadsheet003.dia * 2
  expr: Constraints[1] = Spreadsheet003.F5 / 2
  expr: Constraints[3] = Spreadsheet003.L5
  sketch-geometry (5):
    g0: Circle CenterX=0 CenterY=0 CenterZ=0 NormalX=0 NormalY=0 NormalZ=1 AngleXU=0 Radius=7
    g1: ArcOfCircle CenterX=0 CenterY=0 CenterZ=0 NormalX=0 NormalY=0 NormalZ=1 AngleXU=0 Radius=15 StartAngle=4.71239 EndAngle=7.85398
    g2: LineSegment StartX=3.6683e-12 StartY=15 StartZ=0 EndX=-64 EndY=15 EndZ=0
    g3: LineSegment StartX=-64 StartY=15 StartZ=0 EndX=-64 EndY=-15 EndZ=0
    g4: LineSegment StartX=-64 StartY=-15 StartZ=0 EndX=0 EndY=-15 EndZ=0
  constraints (12):
    c: Coincident(g0,g-1)
    c: Radius(g0) = 7
    c: Coincident(g1,g0)
    c: Radius(g1) = 15
    c: Horizontal(g2)
    c: Coincident(g2,g3)
    c: Vertical(g3)
    c: Coincident(g3,g4)
    c: Horizontal(g4)
    c: Tangent(g1,g2) = -1.5708
    c: Tangent(g1,g4) = -1.5708
    c: Distance(g2) = 64
FEATURE [Part::Cylinder] Cylinder002  label="円柱001"
  Angle = 360
  AttacherType = Attacher::AttachEngine3D
  FirstAngle = 0
  Height = 150
  Placement = pos=(-24,0,0) rot=(0,-1,0;1.5708rad)
  Radius = 6
  SecondAngle = 0
  expr: .Placement.Base.x = -Spreadsheet003.dia * 2
  expr: Height = Spreadsheet003.lx
  expr: Radius = Spreadsheet003.dia / 2
FEATURE [Sketcher::SketchObject] Sketch029
  ArcFitTolerance = 0
  FullyConstrained = true
  MakeInternals = false
  Placement = pos=(0,0,0) rot=(1,0,0;1.5708rad)
  expr: Constraints[10] = Spreadsheet003.C6
  expr: Constraints[11] = Spreadsheet003.B6
  expr: Constraints[12] = Spreadsheet003.D6 / 2
  expr: Constraints[13] = Spreadsheet003.F6 / 2
  expr: Constraints[14] = Spreadsheet003.B6 / 2
  expr: Constraints[17] = Spreadsheet003.C6
  sketch-geometry (6):
    g0: LineSegment StartX=-50 StartY=0 StartZ=0 EndX=-50 EndY=11 EndZ=0
    g1: LineSegment StartX=-50 StartY=11 StartZ=0 EndX=-30 EndY=15 EndZ=0
    g2: LineSegment StartX=-30 StartY=15 StartZ=0 EndX=30 EndY=15 EndZ=0
    g3: LineSegment StartX=30 StartY=15 StartZ=0 EndX=50 EndY=11 EndZ=0
    g4: LineSegment StartX=50 StartY=11 StartZ=0 EndX=50 EndY=0 EndZ=0
    g5: LineSegment StartX=50 StartY=0 StartZ=0 EndX=-50 EndY=0 EndZ=0
  constraints (18):
    c: PointOnObject(g0,g-1)
    c: Vertical(g0)
    c: Coincident(g0,g1)
    c: Coincident(g1,g2)
    c: Horizontal(g2)
    c: Coincident(g2,g3)
    c: Coincident(g3,g4)
    c: PointOnObject(g4,g-1)
    c: Vertical(g4)
    c: Coincident(g4,g5)
    c: DistanceX(g2,g3) = 20
    c: DistanceX(g0,g3) = 100
    c: Distance(g1,g5) = 15
    c: Distance(g4) = 11
    c: DistanceX(g-1,g4) = 50
    c: Horizontal(g0,g3)
    c: Coincident(g5,g0)
    c: DistanceX(g0,g1) = 20
FEATURE [Part::Revolution] Revolve003
  Angle = 360
  Axis = (-1,0,0)
  AxisLink = -> Sketch029 [Edge6]
  Base = (-50,0,0)
  FaceMakerClass = Part::FaceMakerBullseye
  Solid = true
  Source = -> Sketch029
  Symmetric = false
FEATURE [Sketcher::SketchObject] Sketch030
  ArcFitTolerance = 0
  FullyConstrained = false
  MakeInternals = false
  Placement = pos=(0,0,0) rot=(0.57735,0.57735,0.57735;2.0944rad)
  expr: Constraints[16] = Spreadsheet003.F6
  expr: Constraints[17] = Spreadsheet003.F6 / 2
  sketch-geometry (8):
    g0: LineSegment StartX=-11 StartY=39.685 StartZ=0 EndX=-26 EndY=39.685 EndZ=0
    g1: LineSegment StartX=-26 StartY=39.685 StartZ=0 EndX=-26 EndY=-39.3666 EndZ=0
    g2: LineSegment StartX=-26 StartY=-39.3666 StartZ=0 EndX=-11 EndY=-39.3666 EndZ=0
    g3: LineSegment StartX=-11 StartY=-39.3666 StartZ=0 EndX=-11 EndY=39.685 EndZ=0
    g4: LineSegment StartX=11 StartY=39.685 StartZ=0 EndX=26 EndY=39.685 EndZ=0
    g5: LineSegment StartX=26 StartY=39.685 StartZ=0 EndX=26 EndY=-40.315 EndZ=0
    g6: LineSegment StartX=26 StartY=-40.315 StartZ=0 EndX=11 EndY=-40.315 EndZ=0
    g7: LineSegment StartX=11 StartY=-40.315 StartZ=0 EndX=11 EndY=39.685 EndZ=0
  constraints (22):
    c: Coincident(g0,g1)
    c: Coincident(g1,g2)
    c: Coincident(g2,g3)
    c: Coincident(g3,g0)
    c: Horizontal(g0)
    c: Horizontal(g2)
    c: Vertical(g1)
    c: Vertical(g3)
    c: Coincident(g4,g5)
    c: Coincident(g5,g6)
    c: Coincident(g6,g7)
    c: Coincident(g7,g4)
    c: Horizontal(g4)
    c: Horizontal(g6)
    c: Vertical(g5)
    c: Vertical(g7)
    c: DistanceX(g0,g4) = 22
    c: Distance(g-1,g7) = 11
    c: Distance(g5) = 80
    c: Distance(g4) = 15
    c: Distance(g0) = 15
    c: Horizontal(g0,g4)
FEATURE [Part::Extrusion] Extrude018  label="Extrude021"
  Base = -> Sketch030
  Dir = (1,0,0)
  DirMode = 2
  FaceMakerClass = Part::FaceMakerBullseye
  FaceMakerMode = 3
  LengthFwd = 300
  LengthRev = 0
  Solid = true
  Symmetric = true
FEATURE [Part::Cut] Cut009
  Base = -> Revolve003
  Tool = -> Extrude018
FEATURE [Sketcher::SketchObject] Sketch031
  ArcFitTolerance = 0
  FullyConstrained = true
  MakeInternals = false
  Placement = pos=(0,0,0) rot=(1,0,0;1.5708rad)
  expr: Constraints[17] = Spreadsheet003.E6
  expr: Constraints[18] = Spreadsheet003.B6 - 2 * Spreadsheet003.C6
  expr: Constraints[19] = (Spreadsheet003.B6 - 2 * Spreadsheet003.C6) / 2
  expr: Constraints[20] = Spreadsheet003.E6 / 2
  sketch-geometry (9):
    g0: LineSegment StartX=30 StartY=3 StartZ=0 EndX=30 EndY=-3 EndZ=0
    g1: LineSegment StartX=25 StartY=-8 StartZ=0 EndX=-25 EndY=-8 EndZ=0
    g2: LineSegment StartX=-30 StartY=-3 StartZ=0 EndX=-30 EndY=3 EndZ=0
    g3: LineSegment StartX=-25 StartY=8 StartZ=0 EndX=25 EndY=8 EndZ=0
    g4: GeomPoint [constr] X=0 Y=0 Z=0
    g5: ArcOfCircle CenterX=-25 CenterY=3 CenterZ=0 NormalX=0 NormalY=0 NormalZ=1 AngleXU=0 Radius=5 StartAngle=1.5708 EndAngle=3.14159
    g6: ArcOfCircle CenterX=-25 CenterY=-3 CenterZ=0 NormalX=0 NormalY=0 NormalZ=1 AngleXU=0 Radius=5 StartAngle=3.14159 EndAngle=4.71239
    g7: ArcOfCircle CenterX=25 CenterY=-3 CenterZ=0 NormalX=0 NormalY=0 NormalZ=1 AngleXU=0 Radius=5 StartAngle=4.71239 EndAngle=6.28319
    g8: ArcOfCircle CenterX=25 CenterY=3 CenterZ=0 NormalX=0 NormalY=0 NormalZ=1 AngleXU=0 Radius=5 StartAngle=0 EndAngle=1.5708
  constraints (21):
    c: Horizontal(g1)
    c: Horizontal(g3)
    c: Vertical(g0)
    c: Vertical(g2)
    c: Coincident(g4,g-1)
    c: Tangent(g3,g5) = 1.5708
    c: Tangent(g2,g5) = 1.5708
    c: Tangent(g1,g6) = 1.5708
    c: Tangent(g2,g6) = 1.5708
    c: Tangent(g1,g7) = 1.5708
    c: Tangent(g0,g7) = 1.5708
    c: Tangent(g0,g8) = 1.5708
    c: Tangent(g3,g8) = 1.5708
    c: Radius(g8) = 5
    c: Equal(g8,g7)
    c: Equal(g7,g6)
    c: Equal(g6,g5)
    c: DistanceY(g1,g3) = 16
    c: DistanceX(g2,g0) = 60
    c: Distance(g4,g2) = 30
    c: Distance(g4,g1) = 8
FEATURE [Part::Extrusion] Extrude019  label="Extrude022"
  Base = -> Sketch031
  Dir = (0,-1,2e-16)
  DirMode = 2
  FaceMakerClass = Part::FaceMakerBullseye
  FaceMakerMode = 3
  LengthFwd = 60
  LengthRev = 0
  Solid = true
  Symmetric = true
FEATURE [Part::Cut] Cut010
  Base = -> Cut009
  Tool = -> Extrude019
FEATURE [Sketcher::SketchObject] Sketch032
  ArcFitTolerance = 0
  FullyConstrained = true
  MakeInternals = false
  Placement = pos=(0,0,0) rot=(0.57735,0.57735,0.57735;2.0944rad)
  expr: Constraints[1] = Spreadsheet003.dia / 2
  sketch-geometry (1):
    g0: Circle CenterX=0 CenterY=0 CenterZ=0 NormalX=0 NormalY=0 NormalZ=1 AngleXU=0 Radius=6
  constraints (2):
    c: Coincident(g0,g-1)
    c: Radius(g0) = 6
FEATURE [Part::Extrusion] Extrude020  label="Extrude023"
  Base = -> Sketch032
  Dir = (1,0,0)
  DirMode = 2
  FaceMakerClass = Part::FaceMakerBullseye
  FaceMakerMode = 3
  LengthFwd = 300
  LengthRev = 0
  Solid = true
  Symmetric = true
FEATURE [Part::Cut] Cut011  label="turnBackle001"
  Base = -> Cut010
  Placement = pos=(-180,0,0) rot=(0,0,1;0rad)
  Tool = -> Extrude020
  expr: .Placement.Base.x = -(Spreadsheet003.dia * 2.5 + Spreadsheet003.lx)
FEATURE [Part::Cylinder] Cylinder003  label="rod001"
  Angle = 360
  AttacherType = Attacher::AttachEngine3D
  FirstAngle = 0
  Height = 2948
  Placement = pos=(-186,0,-1.37e-13) rot=(0,-1,0;1.5708rad)
  Radius = 6
  SecondAngle = 0
  expr: .Placement.Base.x = -(Spreadsheet003.dia * 3 + Spreadsheet003.lx)
  expr: Height = Spreadsheet003.l1
  expr: Radius = Spreadsheet003.dia / 2
FEATURE [Part::Extrusion] Extrude021  label="Extrude024"
  Base = -> Sketch028
  Dir = (0,-1,2e-16)
  DirMode = 2
  FaceMakerClass = Part::FaceMakerBullseye
  FaceMakerMode = 3
  LengthFwd = 6
  LengthRev = 0
  Placement = pos=(0,9,0) rot=(0,0,1;0rad)
  Solid = true
  Symmetric = true
  expr: .Placement.Base.y = Spreadsheet003.dia / 2 + Spreadsheet003.t0 / 2
  expr: LengthFwd = Spreadsheet003.t0
FEATURE [Part::FeaturePython] Clone005  label="Extrude025"  # Draft clone (typed FeaturePython)
  AttacherType = Attacher::AttachEngine3D
  Fuse = false
  Objects = -> [Extrude021]
  Placement = pos=(-3158,9,0) rot=(0,1,0;3.14159rad)
  Scale = (1,1,1)
  expr: .Placement.Base.x = -Spreadsheet003.L0
  expr: .Placement.Base.y = Spreadsheet003.t0 / 2 + Spreadsheet003.dia / 2
FEATURE [App::Part] Part009  label="TurnBackleB"
  Group = -> [Spreadsheet003,Sketch028,Cylinder002,Extrude021,Revolve003,Sketch030,Cut010,Cut009,Extrude018,Extrude019,Extrude020,Sketch031,Sketch029,Sketch032,Cut011,Cylinder003,Clone005]
  Origin = -> Origin015
  Placement = pos=(-3000,-112.525,14) rot=(0.022377,0.708337,-0.70552;3.18582rad)
FEATURE [Part::Mirroring] Mirror004  label="TurnBackleB (mirrored)"
  Base = (200,0,0)
  Normal = (0,-1,0)
  Source = -> Part009
FEATURE [App::Part] Part007  label="skimmerBrade"
  Group = -> [Part006,CNROK75_U,Spreadsheet002,Part008,Array004,ChannelSteel,Sketch027,Part005,Compound005,Part009,Mirror004]
  Origin = -> Origin011
  Placement = pos=(-246.5,0,5203.5) rot=(0,0,1;0rad)
  mass = 61.351
FEATURE [Part::FeaturePython] Single_flange_straight_pipe  # WARN: FeaturePython — macro-defined, semantics opaque (R4)
  L = 150
  dia = 17
  fittings = 06_Single_flange_straight_pipe
  material = 0
  standard = 0
  standard2 = 1
FEATURE [Part::FeaturePython] Elbow  # WARN: FeaturePython — macro-defined, semantics opaque (R4)
  Placement = pos=(581.952,178.548,0) rot=(0,0,1;2.35619rad)
  dia = 16
  fittings = 01_Elbow
  material = 0
  standard = 0
FEATURE [Part::FeaturePython] Single_flange_straight_pipe001  # WARN: FeaturePython — macro-defined, semantics opaque (R4)
  L = 550
  Placement = pos=(6600,-1.0634e-12,4800) rot=(0,0,1;0rad)
  dia = 6
  fittings = 06_Single_flange_straight_pipe
  mass = 44.6721
  material = 0
  standard = 0
  standard2 = 1
  expr: .Placement.Base.x = <<Spreadsheet_Assy>>.dia / 2 - 150
FEATURE [Part::FeaturePython] Flange  # WARN: FeaturePython — macro-defined, semantics opaque (R4)
  Placement = pos=(0,0,0) rot=(0.57735,0.57735,0.57735;2.0944rad)
  dia = 6
  fittings = 00_Flange
  material = 0
  standard = 1
FEATURE [Part::FeaturePython] Ring  # WARN: FeaturePython — macro-defined, semantics opaque (R4)
  D = 360
  Placement = pos=(0,0,0) rot=(0,1,0;1.5708rad)
  d = 315
  sface = 0
FEATURE [Part::Extrusion] Extrude035  label="Extrude041"
  Base = -> Ring
  Dir = (1,0,0)
  DirMode = 2
  FaceMakerClass = Part::FaceMakerBullseye
  FaceMakerMode = 3
  LengthFwd = 300
  LengthRev = 0
  Reversed = true
  Solid = true
  Symmetric = false
FEATURE [App::Part] Part015  label="skimmerBrg"
  Group = -> [Ring,Extrude035,Flange]
  Origin = -> Origin021
  Placement = pos=(6766,-1.1983e-12,0) rot=(0,0,1;0rad)
  mass = 72.0095
  expr: .Placement.Base.x = Spreadsheet006.L0 - Spreadsheet006.l1 + Spreadsheet006.l1 - 300 + Spreadsheet006.l4 - 19
FEATURE [Part::FeaturePython] Straight_tube  # WARN: FeaturePython — macro-defined, semantics opaque (R4)
  L = 4985
  Placement = pos=(1480,0,0) rot=(0,0,1;0rad)
  dia = 16
  fittings = 05_Straight pipe
  material = 1
  standard = 1
  expr: .Placement.Base.x = Spreadsheet006.l4 - 320
  expr: L = Spreadsheet006.L0 - 300
FEATURE [Sketcher::SketchObject] Sketch047
  ArcFitTolerance = 0
  FullyConstrained = true
  MakeInternals = false
  Placement = pos=(0,0,0) rot=(1,0,0;1.5708rad)
  expr: Constraints[35] = Spreadsheet006.L0 - 400 + 80
  sketch-geometry (12):
    g0: LineSegment StartX=4945 StartY=159.25 StartZ=0 EndX=4965 EndY=159.25 EndZ=0
    g1: LineSegment StartX=4965 StartY=159.25 StartZ=0 EndX=4965 EndY=164.25 EndZ=0
    g2: LineSegment StartX=4965 StartY=164.25 StartZ=0 EndX=4945 EndY=164.25 EndZ=0
    g3: LineSegment StartX=4945 StartY=164.25 StartZ=0 EndX=4945 EndY=159.25 EndZ=0
    g4: LineSegment StartX=0 StartY=159.25 StartZ=0 EndX=0 EndY=169.25 EndZ=0
    g5: LineSegment StartX=0 StartY=169.25 StartZ=0 EndX=19 EndY=169.25 EndZ=0
    g6: LineSegment StartX=19 StartY=169.25 StartZ=0 EndX=19 EndY=164.25 EndZ=0
    g7: LineSegment StartX=19 StartY=164.25 StartZ=0 EndX=31 EndY=164.25 EndZ=0
    g8: LineSegment StartX=31 StartY=164.25 StartZ=0 EndX=31 EndY=169.25 EndZ=0
    g9: LineSegment StartX=31 StartY=169.25 StartZ=0 EndX=50 EndY=169.25 EndZ=0
    g10: LineSegment StartX=50 StartY=169.25 StartZ=0 EndX=50 EndY=159.25 EndZ=0
    g11: LineSegment StartX=50 StartY=159.25 StartZ=0 EndX=0 EndY=159.25 EndZ=0
  constraints (36):
    c: Coincident(g0,g1)
    c: Coincident(g1,g2)
    c: Coincident(g2,g3)
    c: Coincident(g3,g0)
    c: Horizontal(g0)
    c: Horizontal(g2)
    c: Vertical(g1)
    c: Vertical(g3)
    c: DistanceY(g-1,g0) = 159.25
    c: DistanceY(g1,g1) = 5
    c: DistanceX(g2,g2) = 20
    c: Vertical(g4)
    c: Coincident(g4,g5)
    c: Horizontal(g5)
    c: Coincident(g5,g6)
    c: Vertical(g6)
    c: Coincident(g6,g7)
    c: Coincident(g7,g8)
    c: Coincident(g8,g9)
    c: Coincident(g9,g10)
    c: Coincident(g10,g11)
    c: Coincident(g11,g4)
    c: Horizontal(g11)
    c: Vertical(g10)
    c: Horizontal(g7)
    c: Horizontal(g9)
    c: Vertical(g8)
    c: DistanceY(g10,g10) = 10
    c: DistanceY(g7,g8) = 5
    c: Horizontal(g8,g5)
    c: DistanceX(g11,g11) = 50
    c: DistanceX(g7,g7) = 12
    c: DistanceX(g5,g5) = 19
    c: DistanceY(g-1,g4) = 159.25
    c: Vertical(g-1,g4)
    c: DistanceX(g-1,g0) = 4965
FEATURE [Part::Revolution] Revolve007
  Angle = 360
  Axis = (1,0,0)
  Base = (0,0,0)
  FaceMakerClass = Part::FaceMakerBullseye
  Placement = pos=(1500,0,0) rot=(0,0,1;0rad)
  Solid = true
  Source = -> Sketch047
  Symmetric = false
  expr: .Placement.Base.x = Spreadsheet006.l4 - 300
FEATURE [Spreadsheet::Sheet] Spreadsheet006  label="Spreadsheet_pipeSkimmer"
  cells = A2='tankDia  D0; B2(D0)=13000; A3='fullLength L0; B3(L0)=5285; A4='length       l1; B4(l1)=1100; A5='越流堰数 n0; B5(n0)=4; A6='越流堰長 l3; B6(l3)=1100; A7='開閉台  h2; B7(h2)=1120; A8='開閉台 位置 l2; B8(l2)=700; A9='軸受位置 l4; B9(l4)=1800
FEATURE [Sketcher::SketchObject] Sketch048
  ArcFitTolerance = 0
  FullyConstrained = false
  MakeInternals = false
  Placement = pos=(0,0,0) rot=(0.57735,0.57735,0.57735;2.0944rad)
  sketch-geometry (3):
    g0: LineSegment StartX=0 StartY=0 StartZ=0 EndX=114.659 EndY=220.257 EndZ=0
    g1: LineSegment StartX=0 StartY=0 StartZ=0 EndX=-114.659 EndY=220.257 EndZ=0
    g2: ArcOfCircle CenterX=0 CenterY=0 CenterZ=0 NormalX=0 NormalY=0 NormalZ=1 AngleXU=0 Radius=248.314 StartAngle=1.09083 EndAngle=2.05076
  constraints (7):
    c: Coincident(g-1,g0)
    c: Coincident(g1,g0)
    c: Coincident(g2,g0)
    c: Coincident(g2,g1)
    c: Coincident(g2,g0)
    c: Angle(g0,g-2) = 0.479966
    c: Angle(g0,g1) = 0.959931
FEATURE [Part::Extrusion] Extrude036  label="Extrude042"
  Base = -> Sketch048
  Dir = (1,0,0)
  DirMode = 2
  FaceMakerClass = Part::FaceMakerBullseye
  FaceMakerMode = 3
  LengthFwd = 1100
  LengthRev = 0
  Placement = pos=(-200,0,0) rot=(0,0,1;0rad)
  Solid = true
  Symmetric = false
  expr: LengthFwd = Spreadsheet006.l3
FEATURE [Part::FeaturePython] Array008  # Draft array (typed FeaturePython)
  AlwaysSyncPlacement = false
  Angle = 360
  ArrayType = 0
  Axis = (0,0,1)
  Base = -> Extrude036
  Center = (0,0,0)
  Count = 4
  ExpandArray = false
  Fuse = false
  IntervalAxis = (0,0,0)
  IntervalX = (1150,0,0)
  IntervalY = (0,100,0)
  IntervalZ = (0,0,100)
  NumberCircles = 3
  NumberPolar = 5
  NumberX = 4
  NumberY = 1
  NumberZ = 1
  Placement = pos=(1781,0,0) rot=(0,0,1;0rad)
  PlacementList = 4 placements: arithmetic series from (-200,0,0) step (1150,0,0) to (3250,0,0)
  RadialDistance = 50
  ScaleList = (4) [(1,1,1),(1,1,1),(1,1,1),(1,1,1)]
  Symmetry = 1
  TangentialDistance = 25
  expr: .IntervalX.x = Spreadsheet006.l3 + 50
  expr: .Placement.Base.x = Spreadsheet006.l4 - 19
  expr: NumberX = Spreadsheet006.n0
FEATURE [Part::Cut] Cut014
  Base = -> Straight_tube
  Tool = -> Array008
FEATURE [Sketcher::SketchObject] Sketch049
  ArcFitTolerance = 0
  FullyConstrained = false
  MakeInternals = false
  Placement = pos=(-30,0,0) rot=(0.57735,0.57735,0.57735;2.0944rad)
  expr: .Placement.Base.x = -30
  sketch-geometry (3):
    g0: LineSegment StartX=0 StartY=0 StartZ=0 EndX=-124.513 EndY=239.188 EndZ=0
    g1: LineSegment StartX=0 StartY=0 StartZ=0 EndX=124.513 EndY=239.188 EndZ=0
    g2: ArcOfCircle CenterX=0 CenterY=0 CenterZ=0 NormalX=0 NormalY=0 NormalZ=1 AngleXU=0 Radius=269.656 StartAngle=1.09083 EndAngle=2.05076
  constraints (7):
    c: Coincident(g0,g-1)
    c: Coincident(g1,g0)
    c: Coincident(g2,g1)
    c: Coincident(g2,g0)
    c: Coincident(g2,g0)
    c: Angle(g1,g0) = 0.959931
    c: Angle(g1,g-2) = 0.479966
FEATURE [Part::Extrusion] Extrude037  label="Extrude043"
  Base = -> Sketch049
  Dir = (1,0,0)
  DirMode = 2
  FaceMakerClass = Part::FaceMakerBullseye
  FaceMakerMode = 3
  LengthFwd = 1000
  LengthRev = 0
  Placement = pos=(1455,0,0) rot=(0,0,1;0rad)
  Reversed = true
  Solid = true
  Symmetric = false
  expr: .Placement.Base.x = -25 + Spreadsheet006.l4 - 320
  expr: LengthFwd = Spreadsheet006.l1 - 100
FEATURE [Part::Cut] Cut015
  Base = -> Cut014
  Tool = -> Extrude037
FEATURE [Sketcher::SketchObject] Sketch050
  ArcFitTolerance = 0
  FullyConstrained = true
  MakeInternals = false
  Placement = pos=(0,0,0) rot=(0.57735,0.57735,0.57735;2.0944rad)
  sketch-geometry (6):
    g0: LineSegment [constr] StartX=0 StartY=0 StartZ=0 EndX=247.487 EndY=247.487 EndZ=0
    g1: Circle CenterX=247.487 CenterY=247.487 CenterZ=0 NormalX=0 NormalY=0 NormalZ=1 AngleXU=0 Radius=7.5
    g2: ArcOfCircle CenterX=247.487 CenterY=247.487 CenterZ=0 NormalX=0 NormalY=0 NormalZ=1 AngleXU=0 Radius=20 StartAngle=5.62869 EndAngle=8.50848
    g3: LineSegment StartX=235.312 StartY=263.354 StartZ=0 EndX=74.8903 EndY=140.258 EndZ=0
    g4: LineSegment StartX=263.354 StartY=235.312 StartZ=0 EndX=140.258 EndY=74.8903 EndZ=0
    g5: ArcOfCircle CenterX=0 CenterY=0 CenterZ=0 NormalX=0 NormalY=0 NormalZ=1 AngleXU=0 Radius=159 StartAngle=0.490434 EndAngle=1.08036
  constraints (15):
    c: Coincident(g0,g-1)
    c: Angle(g-1,g0) = 0.785398
    c: Coincident(g1,g0)
    c: Radius(g1) = 7.5
    c: Coincident(g2,g1)
    c: Coincident(g5,g3)
    c: Coincident(g5,g4)
    c: Coincident(g5,g0)
    c: Tangent(g2,g3) = -1.5708
    c: Tangent(g2,g4) = 1.5708
    c: Equal(g4,g3)
    c: Radius(g5) = 159
    c: Angle(g3,g4) = 0.261799
    c: Distance(g5,g1) = 350
    c: Radius(g2) = 20
FEATURE [Part::Extrusion] Extrude038  label="Extrude044"
  Base = -> Sketch050
  Dir = (1,0,0)
  DirMode = 2
  FaceMakerClass = Part::FaceMakerBullseye
  FaceMakerMode = 3
  LengthFwd = 6
  LengthRev = 0
  Placement = pos=(0,0,0) rot=(0,-0.977851,0.209302;0rad)
  Solid = true
  Symmetric = true
FEATURE [App::Part] Part018  label="arm"
  Group = -> [Sketch050,Extrude038]
  Origin = -> Origin024
  Placement = pos=(6366,0,0) rot=(1,0,0;1.8326rad)
  expr: .Placement.Base.x = Spreadsheet006.L0 - Spreadsheet006.l2 + Spreadsheet006.l4 - 19
FEATURE [Sketcher::SketchObject] Sketch051
  ArcFitTolerance = 0
  FullyConstrained = false
  MakeInternals = false
  MapMode = 5
  Placement = pos=(681,0,0) rot=(0.57735,-0.57735,-0.57735;2.0944rad)
  expr: .Placement.Base.x = -Spreadsheet006.l1 + Spreadsheet006.l4 - 19
  sketch-geometry (1):
    g0: Circle CenterX=0 CenterY=0 CenterZ=0 NormalX=0 NormalY=0 NormalZ=1 AngleXU=0 Radius=159.25
  constraints (1):
    c: Coincident(g0,g-1)
FEATURE [Part::Extrusion] Extrude039  label="Extrude045"
  Base = -> Sketch051
  Dir = (-1,0,0)
  DirMode = 2
  FaceMakerClass = Part::FaceMakerBullseye
  FaceMakerMode = 3
  LengthFwd = 6
  LengthRev = 0
  Placement = pos=(-300,0,0) rot=(0,0,1;0rad)
  Solid = true
  Symmetric = false
  expr: .Placement.Base.x = -300
FEATURE [Part::Feature] Part__Feature005  label="電動トップハンドル_LTKD-01 v5"
  Placement = pos=(0,-389.711,-5.7e-14) rot=(1,0,0;1.5708rad)
  shape: bbox 555.2 x 557.2 x 1150 mm, 73 faces (baked)
FEATURE [App::Part] Part019  label="開閉台"
  Group = -> [Part__Feature005]
  Origin = -> Origin025
  Placement = pos=(0,-400,1120) rot=(0,0,1;3.14159rad)
  expr: .Placement.Base.z = Spreadsheet006.h2
FEATURE [Sketcher::SketchObject] Sketch052
  ArcFitTolerance = 0
  FullyConstrained = false
  MakeInternals = false
  Placement = pos=(0,0,0) rot=(0.57735,0.57735,0.57735;2.0944rad)
  sketch-geometry (5):
    g0: Circle CenterX=0 CenterY=0 CenterZ=0 NormalX=0 NormalY=0 NormalZ=1 AngleXU=0 Radius=7.5
    g1: ArcOfCircle CenterX=0 CenterY=0 CenterZ=0 NormalX=0 NormalY=0 NormalZ=1 AngleXU=0 Radius=20 StartAngle=3.14159 EndAngle=6.28319
    g2: LineSegment StartX=-20 StartY=9.32106e-06 StartZ=0 EndX=-20 EndY=80 EndZ=0
    g3: LineSegment StartX=-20 StartY=80 StartZ=0 EndX=20 EndY=80 EndZ=0
    g4: LineSegment StartX=20 StartY=80 StartZ=0 EndX=20 EndY=3.56439e-05 EndZ=0
  constraints (13):
    c: Coincident(g0,g-1)
    c: Coincident(g1,g0)
    c: Radius(g1) = 20
    c: Radius(g0) = 7.5
    c: Vertical(g2)
    c: Coincident(g2,g3)
    c: Horizontal(g3)
    c: Coincident(g3,g4)
    c: Vertical(g4)
    c: Coincident(g1,g4)
    c: Coincident(g1,g2)
    c: DistanceY(g-1,g3) = 80
    c: DistanceX(g3,g3) = 40
FEATURE [Part::Extrusion] Extrude040  label="Extrude046"
  Base = -> Sketch052
  Dir = (1,0,0)
  DirMode = 2
  FaceMakerClass = Part::FaceMakerBullseye
  FaceMakerMode = 3
  LengthFwd = 40
  LengthRev = 0
  Solid = true
  Symmetric = true
FEATURE [Sketcher::SketchObject] Sketch053
  ArcFitTolerance = 0
  ExternalGeometry = -> [Extrude040]
  FullyConstrained = false
  MakeInternals = false
  MapMode = 5
  Placement = pos=(0,-20,0) rot=(1,0,0;1.5708rad)
  sketch-geometry (4):
    g0: LineSegment StartX=-5 StartY=-25.0355 StartZ=0 EndX=5 EndY=-25.0355 EndZ=0
    g1: LineSegment StartX=5 StartY=-25.0355 StartZ=0 EndX=5 EndY=60 EndZ=0
    g2: LineSegment StartX=5 StartY=60 StartZ=0 EndX=-5 EndY=60 EndZ=0
    g3: LineSegment StartX=-5 StartY=60 StartZ=0 EndX=-5 EndY=-25.0355 EndZ=0
  constraints (11):
    c: Coincident(g0,g1)
    c: Coincident(g1,g2)
    c: Coincident(g2,g3)
    c: Coincident(g3,g0)
    c: Horizontal(g0)
    c: Horizontal(g2)
    c: Vertical(g1)
    c: Vertical(g3)
    c: Distance(g1,g-3) = 20
    c: DistanceX(g0,g0) = 10
    c: DistanceX(g0,g-1) = 5
FEATURE [Part::Extrusion] Extrude041  label="Extrude047"
  Base = -> Sketch053
  Dir = (0,-1,2e-16)
  DirMode = 2
  FaceMakerClass = Part::FaceMakerBullseye
  FaceMakerMode = 3
  LengthFwd = 50
  LengthRev = 0
  Reversed = true
  Solid = true
  Symmetric = false
FEATURE [Part::Cut] Cut016
  Base = -> Extrude040
  Tool = -> Extrude041
FEATURE [Sketcher::SketchObject] Sketch054
  ArcFitTolerance = 0
  FullyConstrained = true
  MakeInternals = false
  MapMode = 5
  Placement = pos=(0,0,80) rot=(0,0,1;0rad)
  sketch-geometry (1):
    g0: Circle CenterX=0 CenterY=0 CenterZ=0 NormalX=0 NormalY=0 NormalZ=1 AngleXU=0 Radius=15
  constraints (2):
    c: Coincident(g0,g-1)
    c: Radius(g0) = 15
FEATURE [Part::Extrusion] Extrude042  label="Extrude048"
  Base = -> Sketch054
  Dir = (0,0,1)
  DirMode = 2
  FaceMakerClass = Part::FaceMakerBullseye
  FaceMakerMode = 3
  LengthFwd = 700
  LengthRev = 0
  Solid = true
  Symmetric = false
FEATURE [Part::FeaturePython] Clone006  label="Cut017"  # Draft clone (typed FeaturePython)
  AttacherType = Attacher::AttachEngine3D
  Fuse = false
  Objects = -> [Cut016]
  Placement = pos=(-1.83e-13,0,850) rot=(0,1,0;3.14159rad)
  Scale = (1,1,1)
FEATURE [App::Part] Part020  label="rod"
  Group = -> [Cut016,Clone006,Sketch053,Sketch052,Sketch054,Extrude040,Extrude041,Extrude042]
  Origin = -> Origin026
FEATURE [Sketcher::SketchObject] Sketch055
  ArcFitTolerance = 0
  FullyConstrained = false
  MakeInternals = false
  Placement = pos=(0,0,0) rot=(0.57735,0.57735,0.57735;2.0944rad)
  sketch-geometry (5):
    g0: Circle CenterX=0 CenterY=0 CenterZ=0 NormalX=0 NormalY=0 NormalZ=1 AngleXU=0 Radius=7.5
    g1: ArcOfCircle CenterX=0 CenterY=0 CenterZ=0 NormalX=0 NormalY=0 NormalZ=1 AngleXU=0 Radius=20 StartAngle=3.14864 EndAngle=6.2925
    g2: LineSegment StartX=-19.9995 StartY=-0.141043 StartZ=0 EndX=-19.9995 EndY=80 EndZ=0
    g3: LineSegment StartX=-19.9995 StartY=80 StartZ=0 EndX=19.9991 EndY=80 EndZ=0
    g4: LineSegment StartX=19.9991 StartY=80 StartZ=0 EndX=19.9991 EndY=0.186233 EndZ=0
  constraints (12):
    c: Coincident(g0,g-1)
    c: Coincident(g1,g0)
    c: Vertical(g2)
    c: Coincident(g2,g3)
    c: Horizontal(g3)
    c: Coincident(g3,g4)
    c: Vertical(g4)
    c: Coincident(g1,g4)
    c: Coincident(g1,g2)
    c: Radius(g0) = 7.5
    c: Radius(g1) = 20
    c: DistanceY(g-1,g3) = 80
FEATURE [Part::Extrusion] Extrude043  label="Extrude049"
  Base = -> Sketch055
  Dir = (1,0,0)
  DirMode = 2
  FaceMakerClass = Part::FaceMakerBullseye
  FaceMakerMode = 3
  LengthFwd = 9
  LengthRev = 0
  Solid = true
  Symmetric = true
FEATURE [Part::Cylinder] Cylinder  label="円柱"
  Angle = 360
  AttacherType = Attacher::AttachEngine3D
  FirstAngle = 0
  Height = 1000
  Placement = pos=(0,0,30) rot=(0,0,1;0rad)
  Radius = 15
  SecondAngle = 0
FEATURE [App::Part] Part021  label="rod002"
  Group = -> [Sketch055,Cylinder,Extrude043]
  Origin = -> Origin027
FEATURE [Part::Compound] Compound011  label="pipeSkimmerRod"
  Links = -> [Part021]
  Placement = pos=(6366,-313.888,1024.93) rot=(0.999876,-0.016418,0.001902;5e-06rad)
  mass = 5.80682
  expr: .Placement.Base.x = Spreadsheet006.L0 - Spreadsheet006.l2 + Spreadsheet006.l4 - 19
FEATURE [Part::Compound] Compound012  label="pipeSkimmerControlDevice"
  Links = -> [Part019]
  Placement = pos=(6366,-303.595,0) rot=(0.999778,-0.016584,0;2e-06rad)
  mass = 120
  expr: .Placement.Base.x = Spreadsheet006.L0 - Spreadsheet006.l2 + Spreadsheet006.l4 - 19
FEATURE [Part::Compound] Compound013  label="pipeSkimmerRod001"
  Links = -> [Part020]
  Placement = pos=(6366,-303.109,175) rot=(1,-4e-06,1e-06;0.012683rad)
  mass = 5.72969
  expr: .Placement.Base.x = Spreadsheet006.L0 - Spreadsheet006.l2 + Spreadsheet006.l4 - 19
FEATURE [Part::FeaturePython] Straight_tube001  # WARN: FeaturePython — macro-defined, semantics opaque (R4)
  L = 1100
  Placement = pos=(1480,0,0) rot=(0,0,1;3.14159rad)
  dia = 16
  fittings = 05_Straight pipe
  material = 0
  standard = 0
  expr: .Placement.Base.x = Spreadsheet006.l4 - 320
  expr: L = Spreadsheet006.l1
FEATURE [Part::Cut] Cut017  label="Cut004"
  Base = -> Straight_tube001
  Refine = true
  Tool = -> Extrude037
FEATURE [App::Part] Part016  label="pipe"
  Group = -> [Sketch047,Revolve007,Part018,Extrude036,Extrude037,Cut015,Cut014,Straight_tube,Array008,Sketch048,Sketch049,Sketch051,Straight_tube001,Cut017]
  Origin = -> Origin022
FEATURE [Part::Compound] Compound010  label="pipeSkimmerBody"
  Links = -> [Part016,Extrude039]
  Placement = pos=(-7.28528e-06,0,0) rot=(0,-0.552174,0.703636;0rad)
  mass = 274.65
FEATURE [App::Part] Part017  label="pipeSkimmer"
  Group = -> [Part016,Part015,Spreadsheet006,Part019,Part020,Compound010,Part021,Compound011,Compound012,Compound013]
  Origin = -> Origin023
  Placement = pos=(-195,0,4800) rot=(0,0,1;0rad)
FEATURE [Part::FeaturePython] AngleSteel007  label="AngleSteel012"  # WARN: FeaturePython — macro-defined, semantics opaque (R4)
  A = 75
  B = 75
  L = 500
  Placement = pos=(487.5,-250,712.5) rot=(0.57735,-0.57735,-0.57735;4.18879rad)
  Solid = true
  g0 = 7.85
  mass = 3.4251
  size = 10
  standard = SS_Equal
  t = 6
  expr: .Placement.Base.x = Spreadsheet007.H0 - Spreadsheet007.h1 + 37.5
  expr: .Placement.Base.y = -Spreadsheet007.W0 / 2 + 75
  expr: .Placement.Base.z = Spreadsheet007.H0 - 37.5
  expr: L = Spreadsheet007.W0 - 150
FEATURE [Part::FeaturePython] Clone007  label="AngleSteel008"  # Draft clone (typed FeaturePython)
  AttacherType = Attacher::AttachEngine3D
  Fuse = false
  Objects = -> [AngleSteel007]
  Placement = pos=(37.5,-250,262.5) rot=(0.57735,-0.57735,-0.57735;4.18879rad)
  Scale = (1,1,1)
  expr: .Placement.Base.y = -Spreadsheet007.W0 / 2 + 75
  expr: .Placement.Base.z = Spreadsheet007.h1 - 37.5
FEATURE [Part::FeaturePython] Clone008  label="AngleSteel007"  # Draft clone (typed FeaturePython)
  AttacherType = Attacher::AttachEngine3D
  Fuse = false
  Objects = -> [AngleSteel007]
  Placement = pos=(37.5,-250,37.5) rot=(-1,0,0;1.5708rad)
  Scale = (1,1,1)
  expr: .Placement.Base.y = -Spreadsheet007.W0 / 2 + 75
FEATURE [Part::FeaturePython] Clone009  label="AngleSteel009"  # Draft clone (typed FeaturePython)
  AttacherType = Attacher::AttachEngine3D
  Fuse = false
  Objects = -> [AngleSteel007]
  Placement = pos=(6412.5,-250,37.54) rot=(0.57735,0.57735,0.57735;4.18879rad)
  Scale = (1,1,1)
  expr: .Placement.Base.x = Spreadsheet007.L0 - 37.5
  expr: .Placement.Base.y = -Spreadsheet007.W0 / 2 + 75
FEATURE [Part::FeaturePython] Clone010  label="AngleSteel010"  # Draft clone (typed FeaturePython)
  AttacherType = Attacher::AttachEngine3D
  Fuse = false
  Objects = -> [AngleSteel007]
  Placement = pos=(487.5,-250,37.5) rot=(-1,0,0;1.5708rad)
  Scale = (1,1,1)
  expr: .Placement.Base.x = Spreadsheet007.H0 - Spreadsheet007.h1 + 37.5
  expr: .Placement.Base.y = -Spreadsheet007.W0 / 2 + 75
FEATURE [Part::FeaturePython] Array009  label="bottmMember"  # Draft array (typed FeaturePython)
  AlwaysSyncPlacement = false
  Angle = 360
  ArrayType = 0
  Axis = (0,0,1)
  Base = -> Clone010
  Center = (0,0,0)
  Count = 9
  ExpandArray = false
  Fuse = false
  IntervalAxis = (0,0,0)
  IntervalX = (684.375,0,0)
  IntervalY = (0,100,0)
  IntervalZ = (0,0,100)
  NumberCircles = 3
  NumberPolar = 5
  NumberX = 9
  NumberY = 1
  NumberZ = 1
  PlacementList = 9 placements: arithmetic series from (487.5,-250,37.5) step (684.375,0,0) to (5962.5,-250,37.5)
  RadialDistance = 50
  ScaleList = (9) [(1,1,1),(1,1,1),(1,1,1),(1,1,1),(1,1,1),(1,1,1),(1,1,1),(1,1,1),(1,1,1)]
  Symmetry = 1
  TangentialDistance = 25
  expr: .IntervalX.x = Spreadsheet007.p0
  expr: NumberX = Spreadsheet007.n0
FEATURE [Part::FeaturePython] Clone011  label="AngleSteel011"  # Draft clone (typed FeaturePython)
  AttacherType = Attacher::AttachEngine3D
  Fuse = false
  Objects = -> [AngleSteel007]
  Placement = pos=(5962.5,-250,712.5) rot=(0,0.707107,0.707107;3.14159rad)
  Scale = (1,1,1)
  expr: .Placement.Base.x = Spreadsheet007.L0 - (Spreadsheet007.H0 - Spreadsheet007.h1) - 37.5
  expr: .Placement.Base.y = -Spreadsheet007.W0 / 2 + 75
  expr: .Placement.Base.z = Spreadsheet007.H0 - 37.5
FEATURE [Part::FeaturePython] Array010  label="topMember"  # Draft array (typed FeaturePython)
  AlwaysSyncPlacement = false
  Angle = 360
  ArrayType = 0
  Axis = (0,0,1)
  Base = -> AngleSteel007
  Center = (0,0,0)
  Count = 8
  ExpandArray = false
  Fuse = false
  IntervalAxis = (0,0,0)
  IntervalX = (684.375,0,0)
  IntervalY = (0,100,0)
  IntervalZ = (0,0,100)
  NumberCircles = 3
  NumberPolar = 5
  NumberX = 8
  NumberY = 1
  NumberZ = 1
  PlacementList = 8 placements: arithmetic series from (487.5,-250,712.5) step (684.375,0,0) to (5278.12,-250,712.5)
  RadialDistance = 50
  ScaleList = (8) [(1,1,1),(1,1,1),(1,1,1),(1,1,1),(1,1,1),(1,1,1),(1,1,1),(1,1,1)]
  Symmetry = 1
  TangentialDistance = 25
  expr: .IntervalX.x = <<Spreadsheet007>>.p0
  expr: NumberX = Spreadsheet007.n0 - 1
FEATURE [Sketcher::SketchObject] Sketch057
  ArcFitTolerance = 0
  FullyConstrained = false
  MakeInternals = false
  Placement = pos=(0,0,0) rot=(1,0,0;1.5708rad)
  sketch-geometry (7):
    g0: LineSegment StartX=0 StartY=36.614 StartZ=0 EndX=0 EndY=161.614 EndZ=0
    g1: LineSegment StartX=0 StartY=161.614 StartZ=0 EndX=-30 EndY=161.614 EndZ=0
    g2: LineSegment StartX=-30 StartY=161.614 StartZ=0 EndX=-95.0179 EndY=130.728 EndZ=0
    g3: ArcOfCircle CenterX=-80 CenterY=99.114 CenterZ=0 NormalX=0 NormalY=0 NormalZ=1 AngleXU=0 Radius=35 StartAngle=2.01427 EndAngle=4.26891
    g4: LineSegment StartX=-95.0179 StartY=67.4997 StartZ=0 EndX=-30 EndY=36.614 EndZ=0
    g5: LineSegment StartX=-30 StartY=36.614 StartZ=0 EndX=0 EndY=36.614 EndZ=0
    g6: Circle CenterX=-80 CenterY=99.114 CenterZ=0 NormalX=0 NormalY=0 NormalZ=1 AngleXU=0 Radius=15
  constraints (18):
    c: Vertical(g0)
    c: Coincident(g0,g1)
    c: Horizontal(g1)
    c: Coincident(g1,g2)
    c: Tangent(g2,g3) = -1.5708
    c: Coincident(g4,g5)
    c: Coincident(g5,g0)
    c: Coincident(g6,g3)
    c: Horizontal(g5)
    c: PointOnObject(g0,g-2)
    c: DistanceY(g0,g0) = 125
    c: Equal(g1,g5)
    c: DistanceX(g1,g1) = 30
    c: Tangent(g3,g4) = -1.5708
    c: Distance(g3,g0) = 80
    c: Radius(g6) = 15
    c: Radius(g3) = 35
    c: Equal(g2,g4)
FEATURE [Part::Extrusion] Extrude045  label="bracketBottom"
  Base = -> Sketch057
  Dir = (0,-1,2e-16)
  DirMode = 2
  FaceMakerClass = Part::FaceMakerBullseye
  FaceMakerMode = 3
  LengthFwd = 16
  LengthRev = 0
  Reversed = true
  Solid = true
  Symmetric = false
FEATURE [Part::FeaturePython] AngleSteel008  label="AngleSteel013"  # WARN: FeaturePython — macro-defined, semantics opaque (R4)
  A = 75
  B = 75
  L = 975.317
  Placement = pos=(471.345,-37.5,728.919) rot=(0,1,0;2.35004rad)
  Solid = true
  g0 = 7.85
  mass = 6.68112
  size = 10
  standard = SS_Equal
  t = 6
  expr: .Placement.Base.x = Spreadsheet007.H0 - Spreadsheet007.h1 + Spreadsheet007.lx
  expr: .Placement.Base.z = Spreadsheet007.H0 - Spreadsheet007.lz
  expr: .Placement.Rotation.Angle = Spreadsheet007.sita + 90
  expr: L = Spreadsheet007.l2 - 40
FEATURE [Part::FeaturePython] Array011  label="diagonalMember"  # Draft array (typed FeaturePython)
  AlwaysSyncPlacement = false
  Angle = 360
  ArrayType = 0
  Axis = (0,0,1)
  Base = -> AngleSteel008
  Center = (0,0,0)
  Count = 8
  ExpandArray = false
  Fuse = false
  IntervalAxis = (0,0,0)
  IntervalX = (684.375,0,0)
  IntervalY = (0,100,0)
  IntervalZ = (0,0,100)
  NumberCircles = 3
  NumberPolar = 5
  NumberX = 8
  NumberY = 1
  NumberZ = 1
  PlacementList = 8 placements: arithmetic series from (471.345,-37.5,728.919) step (684.375,0,0) to (5261.97,-37.5,728.919)
  RadialDistance = 50
  ScaleList = (8) [(1,1,1),(1,1,1),(1,1,1),(1,1,1),(1,1,1),(1,1,1),(1,1,1),(1,1,1)]
  Symmetry = 1
  TangentialDistance = 25
  expr: .IntervalX.x = Spreadsheet007.p0
  expr: NumberX = Spreadsheet007.n0 - 1
FEATURE [Part::FeaturePython] AngleSteel009  label="AngleSteel014"  # WARN: FeaturePython — macro-defined, semantics opaque (R4)
  A = 75
  B = 75
  L = 720
  Placement = pos=(487.5,43.5,15) rot=(0,0,1;1.5708rad)
  Solid = true
  g0 = 7.85
  mass = 4.93215
  size = 10
  standard = SS_Equal
  t = 6
  expr: .Placement.Base.x = Spreadsheet007.H0 - Spreadsheet007.h1 + 37.5
  expr: L = Spreadsheet007.H0 - 30
FEATURE [Part::FeaturePython] Array012  label="verticalMember"  # Draft array (typed FeaturePython)
  AlwaysSyncPlacement = false
  Angle = 360
  ArrayType = 0
  Axis = (0,0,1)
  Base = -> AngleSteel009
  Center = (0,0,0)
  Count = 9
  ExpandArray = false
  Fuse = false
  IntervalAxis = (0,0,0)
  IntervalX = (684.375,0,0)
  IntervalY = (0,100,0)
  IntervalZ = (0,0,100)
  NumberCircles = 3
  NumberPolar = 5
  NumberX = 9
  NumberY = 1
  NumberZ = 1
  PlacementList = 9 placements: arithmetic series from (487.5,43.5,15) step (684.375,0,0) to (5962.5,43.5,15)
  RadialDistance = 50
  ScaleList = (9) [(1,1,1),(1,1,1),(1,1,1),(1,1,1),(1,1,1),(1,1,1),(1,1,1),(1,1,1),(1,1,1)]
  Symmetry = 1
  TangentialDistance = 25
  expr: .IntervalX.x = Spreadsheet007.p0
  expr: NumberX = Spreadsheet007.n0
FEATURE [Sketcher::SketchObject] Sketch058
  ArcFitTolerance = 0
  AttachmentSupport = -> [XZ_Plane028]
  FullyConstrained = true
  MakeInternals = false
  MapMode = 5
  Placement = pos=(0,0,0) rot=(1,0,0;1.5708rad)
  expr: Constraints[12] = Spreadsheet007.L0
  expr: Constraints[15] = Spreadsheet007.h1
  expr: Constraints[16] = Spreadsheet007.H0
  sketch-geometry (6):
    g0: LineSegment StartX=0 StartY=0 StartZ=0 EndX=0 EndY=300 EndZ=0
    g1: LineSegment StartX=0 StartY=300 StartZ=0 EndX=450 EndY=750 EndZ=0
    g2: LineSegment StartX=450 StartY=750 StartZ=0 EndX=6000 EndY=750 EndZ=0
    g3: LineSegment StartX=6000 StartY=750 StartZ=0 EndX=6450 EndY=300 EndZ=0
    g4: LineSegment StartX=6450 StartY=300 StartZ=0 EndX=6450 EndY=0 EndZ=0
    g5: LineSegment StartX=6450 StartY=0 StartZ=0 EndX=0 EndY=0 EndZ=0
  constraints (18):
    c: PointOnObject(g0,g-2)
    c: PointOnObject(g0,g-2)
    c: Coincident(g0,g1)
    c: Coincident(g1,g2)
    c: Horizontal(g2)
    c: Coincident(g2,g3)
    c: Coincident(g3,g4)
    c: PointOnObject(g4,g-1)
    c: Vertical(g4)
    c: Coincident(g4,g5)
    c: Coincident(g5,g0)
    c: Horizontal(g5)
    c: Distance(g5) = 6450
    c: Angle(g-2,g1) = 2.35619
    c: Angle(g2,g3) = 2.35619
    c: DistanceY(g0,g0) = 300
    c: Distance(g2,g5) = 750
    c: Equal(g4,g0)
FEATURE [Sketcher::SketchObject] Sketch056
  ArcFitTolerance = 0
  ExternalGeometry = -> [Sketch058,AngleSteel007]
  FullyConstrained = true
  MakeInternals = false
  Placement = pos=(0,0,0) rot=(1,0,0;1.5708rad)
  expr: Constraints[12] = (Spreadsheet007.L0 - (Spreadsheet007.H0 - Spreadsheet007.h1)) / (Spreadsheet007.n0 - 1) - 150
  sketch-geometry (6):
    g0: LineSegment StartX=1250 StartY=750 StartZ=0 EndX=1250 EndY=780 EndZ=0
    g1: LineSegment StartX=1250 StartY=780 StartZ=0 EndX=1104.7 EndY=878.931 EndZ=0
    g2: ArcOfCircle CenterX=1085 CenterY=850 CenterZ=0 NormalX=0 NormalY=0 NormalZ=1 AngleXU=0 Radius=35 StartAngle=0.97303 EndAngle=3.14159
    g3: Circle CenterX=1085 CenterY=850 CenterZ=0 NormalX=0 NormalY=0 NormalZ=1 AngleXU=0 Radius=15
    g4: LineSegment StartX=1050 StartY=850 StartZ=0 EndX=1050 EndY=750 EndZ=0
    g5: LineSegment StartX=1050 StartY=750 StartZ=0 EndX=1250 EndY=750 EndZ=0
  constraints (16):
    c: Coincident(g0,g1)
    c: Tangent(g1,g2) = -1.5708
    c: Coincident(g3,g2)
    c: Vertical(g0)
    c: DistanceY(g0,g0) = 30
    c: Radius(g3) = 15
    c: Radius(g2) = 35
    c: DistanceX(g2,g0) = 200
    c: PointOnObject(g4,g-3)
    c: PointOnObject(g0,g-3)
    c: Coincident(g5,g4)
    c: Coincident(g5,g0)
    c: DistanceX(g-4,g4) = 600
    c: Vertical(g4)
    c: Tangent(g4,g2) = -1.5708
    c: DistanceY(g4,g2) = 100
FEATURE [Part::Extrusion] Extrude044  label="bracketTop"
  Base = -> Sketch056
  Dir = (0,-1,2e-16)
  DirMode = 2
  FaceMakerClass = Part::FaceMakerBullseye
  FaceMakerMode = 3
  LengthFwd = 16
  LengthRev = 0
  Reversed = true
  Solid = true
  Symmetric = false
FEATURE [Spreadsheet::Sheet] Spreadsheet007
  cells = A2='L0; B2(L0)=6450; A3='H0; B3(H0)=750; A4='h1; B4(h1)=300; A5='W0; B5(W0)=650; A6='div n0; B6(n0)=9; A7='p0; B7(p0)=684.375; A8='sita; B8(sita)=44.6474187181845; A9='l2; B9(l2)=1015.31726106917; A10='lx; B10(lx)=21.344550743983; A11='lz; B11(lz)=21.081037771835; A12='beta; B12(beta)=5.7; A13='picketFence  pl; B13(pk)=1000; A14='bradePosition br; B14(br)=750; A15='no of brade n0; B15(n00)=6; A16='bradeSpacing; B16(brs)=1020
FEATURE [Part::FeaturePython] AngleSteel010  label="AngleSteel015"  # WARN: FeaturePython — macro-defined, semantics opaque (R4)
  A = 75
  B = 75
  L = 1000
  Placement = pos=(0,0,0) rot=(0,0,1;1.5708rad)
  Solid = false
  g0 = 7.85
  mass = 0
  size = 10
  standard = SS_Equal
  t = 6
FEATURE [Part::Sweep] Sweep001  label="mainMaterial"
  Frenet = false
  Sections = -> [AngleSteel010]
  Solid = true
  Spine = -> Sketch058 [Edge6,Edge5,Edge4,Edge3,Edge2,Edge1]
  Transition = 1
FEATURE [Part::Compound] Compound014  label="rake"
  Links = -> [Sweep001,Array012,Array011,Extrude045,Extrude044]
  Placement = pos=(0,-325,0) rot=(0,0,1;0rad)
  expr: .Placement.Base.y = -Spreadsheet007.W0 / 2
FEATURE [Part::Mirroring] Mirror016  label="rake001"
  Base = (0,-8.88e-14,400)
  Normal = (0,-1,0)
  Source = -> Compound014
FEATURE [Part::FeaturePython] AngleSteel011  label="AngleSteel016"  # WARN: FeaturePython — macro-defined, semantics opaque (R4)
  A = 50
  B = 50
  L = 200
  Placement = pos=(25,0,0) rot=(0,0,1;0rad)
  Solid = true
  g0 = 7.85
  mass = 0.88607
  size = 7
  standard = SS_Equal
  t = 6
FEATURE [Sketcher::SketchObject] Sketch059
  ArcFitTolerance = 0
  FullyConstrained = false
  MakeInternals = false
  Placement = pos=(0,0,0) rot=(1,0,0;1.5708rad)
  expr: Constraints[6] = Spreadsheet007.beta
  sketch-geometry (3):
    g0: LineSegment StartX=0 StartY=0 StartZ=0 EndX=64.1183 EndY=6.39986 EndZ=0
    g1: LineSegment StartX=64.1183 StartY=6.39986 StartZ=0 EndX=64.1183 EndY=0 EndZ=0
    g2: LineSegment StartX=64.1183 StartY=0 StartZ=0 EndX=0 EndY=0 EndZ=0
  constraints (7):
    c: Coincident(g-1,g0)
    c: Coincident(g0,g1)
    c: Vertical(g1)
    c: Coincident(g1,g2)
    c: Coincident(g2,g0)
    c: Horizontal(g2)
    c: Angle(g2,g0) = 0.0994838
FEATURE [Part::Extrusion] Extrude046  label="Extrude050"
  Base = -> Sketch059
  Dir = (0,-1,2e-16)
  DirMode = 2
  FaceMakerClass = Part::FaceMakerBullseye
  FaceMakerMode = 3
  LengthFwd = 50
  LengthRev = 0
  Solid = true
  Symmetric = true
FEATURE [Part::Cut] Cut018
  Base = -> AngleSteel011
  Placement = pos=(450,0,750) rot=(0,1,0;0.099484rad)
  Tool = -> Extrude046
  expr: .Placement.Base.x = Spreadsheet007.H0 - Spreadsheet007.h1
  expr: .Placement.Base.z = Spreadsheet007.H0
FEATURE [Part::FeaturePython] Array013  label="picketFenceReciever"  # Draft array (typed FeaturePython)
  AlwaysSyncPlacement = false
  Angle = 360
  ArrayType = 0
  Axis = (0,0,1)
  Base = -> Cut018
  Center = (0,0,0)
  Count = 9
  ExpandArray = false
  Fuse = false
  IntervalAxis = (0,0,0)
  IntervalX = (684.375,0,0)
  IntervalY = (0,100,0)
  IntervalZ = (0,0,100)
  NumberCircles = 3
  NumberPolar = 5
  NumberX = 9
  NumberY = 1
  NumberZ = 1
  PlacementList = 9 placements: arithmetic series from (450,0,750) step (684.375,0,0) to (5925,0,750)
  RadialDistance = 50
  ScaleList = (9) [(1,1,1),(1,1,1),(1,1,1),(1,1,1),(1,1,1),(1,1,1),(1,1,1),(1,1,1),(1,1,1)]
  Symmetry = 1
  TangentialDistance = 25
  expr: .IntervalX.x = Spreadsheet007.p0
  expr: NumberX = Spreadsheet007.n0
FEATURE [Part::FeaturePython] AngleSteel012  label="AngleSteel017"  # WARN: FeaturePython — macro-defined, semantics opaque (R4)
  A = 50
  B = 50
  L = 1500
  Placement = pos=(25,0,0) rot=(0,0,1;1.5708rad)
  Solid = true
  g0 = 7.85
  mass = 6.64552
  size = 7
  standard = SS_Equal
  t = 6
FEATURE [App::Part] Part023  label="Part001"
  Group = -> [AngleSteel012]
  Origin = -> Origin029
  Placement = pos=(450.993,50,760) rot=(0,1,0;0.099484rad)
  expr: .Placement.Base.x = Spreadsheet007.H0 - Spreadsheet007.h1 + 10 * sin(Spreadsheet007.beta)
  expr: .Placement.Base.z = Spreadsheet007.H0 + 10
FEATURE [Part::FeaturePython] Array014  # Draft array (typed FeaturePython)
  AlwaysSyncPlacement = false
  Angle = 360
  ArrayType = 0
  Axis = (0,0,1)
  Base = -> Part023
  Center = (0,0,0)
  Count = 9
  ExpandArray = false
  Fuse = false
  IntervalAxis = (0,0,0)
  IntervalX = (684.375,0,0)
  IntervalY = (0,100,0)
  IntervalZ = (0,0,100)
  NumberCircles = 3
  NumberPolar = 5
  NumberX = 9
  NumberY = 1
  NumberZ = 1
  PlacementList = 9 placements: arithmetic series from (450.993,50,760) step (684.375,0,0) to (5925.99,50,760)
  RadialDistance = 50
  ScaleList = (9) [(1,1,1),(1,1,1),(1,1,1),(1,1,1),(1,1,1),(1,1,1),(1,1,1),(1,1,1),(1,1,1)]
  Symmetry = 1
  TangentialDistance = 25
  expr: .IntervalX.x = Spreadsheet007.p0
  expr: NumberX = Spreadsheet007.n0
FEATURE [Sketcher::SketchObject] Sketch060
  ArcFitTolerance = 0
  FullyConstrained = true
  MakeInternals = false
  Placement = pos=(0,0,0) rot=(1,0,0;1.5708rad)
  expr: Constraints[11] = Spreadsheet007.beta
  expr: Constraints[1] = Spreadsheet007.H0 + Spreadsheet007.pk / cos(Spreadsheet007.beta)
  expr: Constraints[2] = Spreadsheet007.H0 - Spreadsheet007.h1 + (Spreadsheet007.pk + 10) * sin(Spreadsheet007.beta) - 20
  expr: Constraints[3] = Spreadsheet007.L0
  sketch-geometry (4):
    g0: LineSegment StartX=530.313 StartY=1754.97 StartZ=0 EndX=6980.31 EndY=1111.17 EndZ=0
    g1: LineSegment StartX=6980.31 StartY=1111.17 StartZ=0 EndX=6980.31 EndY=2554.97 EndZ=0
    g2: LineSegment StartX=530.313 StartY=1754.97 StartZ=0 EndX=530.313 EndY=2554.97 EndZ=0
    g3: LineSegment StartX=530.313 StartY=2554.97 StartZ=0 EndX=6980.31 EndY=2554.97 EndZ=0
  constraints (12):
    c: Coincident(g0,g1)
    c: DistanceY(g-1,g0) = 1754.97
    c: DistanceX(g-1,g0) = 530.313
    c: DistanceX(g0,g1) = 6450
    c: Vertical(g1)
    c: Coincident(g0,g2)
    c: Vertical(g2)
    c: Coincident(g2,g3)
    c: Horizontal(g3)
    c: Coincident(g1,g3)
    c: DistanceY(g2,g2) = 800
    c: Angle(g0,g3) = 0.0994838
FEATURE [Part::Extrusion] Extrude047  label="Extrude051"
  Base = -> Sketch060
  Dir = (0,-1,2e-16)
  DirMode = 2
  FaceMakerClass = Part::FaceMakerBullseye
  FaceMakerMode = 3
  LengthFwd = 200
  LengthRev = 0
  Solid = true
  Symmetric = true
FEATURE [Part::Cut] Cut019  label="picketFence"
  Base = -> Array014
  Tool = -> Extrude047
FEATURE [App::Part] Part022  label="RakeArm"
  Group = -> [AngleSteel010,Sketch058,Sweep001,AngleSteel009,Array012,AngleSteel008,Array011,Sketch057,Extrude045,Sketch056,Extrude044,Compound014,Mirror016,AngleSteel007,Array010,Clone011,Clone010,Array009,Clone009,Clone008,Clone007,Sketch059,Extrude046,AngleSteel011,Cut018,Array013,Part023,Array014,Sketch060,Extrude047,Cut019]
  Origin = -> Origin028
FEATURE [Part::FeaturePython] AngleSteel013  label="AngleSteel018"  # WARN: FeaturePython — macro-defined, semantics opaque (R4)
  A = 75
  B = 75
  L = 1000
  Placement = pos=(0,0,0) rot=(0.707107,0.707107,0;3.14159rad)
  Solid = false
  g0 = 7.85
  mass = 0
  size = 10
  standard = SS_Equal
  t = 6
FEATURE [Part::Extrusion] Extrude048  label="Extrude052"
  Base = -> AngleSteel013
  Dir = (1,-2e-16,1e-16)
  DirMode = 2
  FaceMakerClass = Part::FaceMakerBullseye
  FaceMakerMode = 3
  LengthFwd = 1600
  LengthRev = 0
  Solid = false
  Symmetric = true
FEATURE [Sketcher::SketchObject] Sketch061
  ArcFitTolerance = 0
  AttachmentSupport = -> [Extrude048]
  ExternalGeometry = -> [Extrude048]
  FullyConstrained = false
  MakeInternals = false
  MapMode = 5
  Placement = pos=(0,1.6e-15,0) rot=(1,0,0;1.5708rad)
  sketch-geometry (8):
    g0: Circle CenterX=-700 CenterY=-40.4478 CenterZ=0 NormalX=0 NormalY=0 NormalZ=1 AngleXU=0 Radius=7
    g1: Circle CenterX=700 CenterY=-39.6228 CenterZ=0 NormalX=0 NormalY=0 NormalZ=1 AngleXU=0 Radius=7
    g2: Circle CenterX=-500 CenterY=-40.4478 CenterZ=0 NormalX=0 NormalY=0 NormalZ=1 AngleXU=0 Radius=7
    g3: Circle CenterX=-299.492 CenterY=-40.4478 CenterZ=0 NormalX=0 NormalY=0 NormalZ=1 AngleXU=0 Radius=7
    g4: Circle CenterX=-99.2385 CenterY=-40.4478 CenterZ=0 NormalX=0 NormalY=0 NormalZ=1 AngleXU=0 Radius=7
    g5: Circle CenterX=101.015 CenterY=-40.4478 CenterZ=0 NormalX=0 NormalY=0 NormalZ=1 AngleXU=0 Radius=7
    g6: Circle CenterX=301.269 CenterY=-40.4478 CenterZ=0 NormalX=0 NormalY=0 NormalZ=1 AngleXU=0 Radius=7
    g7: Circle CenterX=501.523 CenterY=-40.4478 CenterZ=0 NormalX=0 NormalY=0 NormalZ=1 AngleXU=0 Radius=7
  constraints (11):
    c: Diameter(g0) = 14
    c: Diameter(g1) = 14
    c: DistanceX(g-3,g0) = 100
    c: DistanceX(g1,g-4) = 100
    c: Equal(g0,g2) = 14
    c: Equal(g0,g3) = 14
    c: Equal(g0,g4) = 14
    c: Equal(g0,g5) = 14
    c: Equal(g0,g6) = 14
    c: Equal(g0,g7) = 14
    c: DistanceX(g0,g2) = 200
FEATURE [Part::Extrusion] Extrude049  label="Extrude053"
  Base = -> Sketch061
  Dir = (0,-1,2e-16)
  DirMode = 2
  FaceMakerClass = Part::FaceMakerBullseye
  FaceMakerMode = 3
  LengthFwd = 10
  LengthRev = 0
  Reversed = true
  Solid = true
  Symmetric = false
FEATURE [Part::Cut] Cut020  label="angle"
  Base = -> Extrude048
  Tool = -> Extrude049
FEATURE [Sketcher::SketchObject] Sketch062
  ArcFitTolerance = 0
  FullyConstrained = false
  MakeInternals = false
  Placement = pos=(0,0,0) rot=(1,0,0;1.5708rad)
  sketch-geometry (67):
    g0: LineSegment StartX=-800 StartY=-70 StartZ=0 EndX=-800 EndY=70 EndZ=0
    g1: LineSegment StartX=-800 StartY=70 StartZ=0 EndX=800 EndY=70 EndZ=0
    g2: LineSegment StartX=800 StartY=70 StartZ=0 EndX=800 EndY=-70 EndZ=0
    g3: LineSegment StartX=800 StartY=-70 StartZ=0 EndX=-800 EndY=-70 EndZ=0
    g4: GeomPoint [constr] X=0 Y=0 Z=0
    g5: Circle CenterX=-700 CenterY=40 CenterZ=0 NormalX=0 NormalY=0 NormalZ=1 AngleXU=0 Radius=7
    g6: Circle CenterX=100 CenterY=40 CenterZ=0 NormalX=0 NormalY=0 NormalZ=1 AngleXU=0 Radius=7
    g7: Circle CenterX=-500 CenterY=40 CenterZ=0 NormalX=0 NormalY=0 NormalZ=1 AngleXU=0 Radius=7
    g8: Circle CenterX=-300 CenterY=40 CenterZ=0 NormalX=0 NormalY=0 NormalZ=1 AngleXU=0 Radius=7
    g9: Circle CenterX=-100 CenterY=40 CenterZ=0 NormalX=0 NormalY=0 NormalZ=1 AngleXU=0 Radius=7
    g10: Circle CenterX=300 CenterY=40 CenterZ=0 NormalX=0 NormalY=0 NormalZ=1 AngleXU=0 Radius=7
    g11: Circle CenterX=500 CenterY=40 CenterZ=0 NormalX=0 NormalY=0 NormalZ=1 AngleXU=0 Radius=7
    g12: Circle CenterX=700 CenterY=40 CenterZ=0 NormalX=0 NormalY=0 NormalZ=1 AngleXU=0 Radius=7
    g13: LineSegment StartX=-743 StartY=5 StartZ=0 EndX=-743 EndY=-45 EndZ=0
    g14: ArcOfCircle CenterX=-750 CenterY=-45 CenterZ=0 NormalX=0 NormalY=0 NormalZ=1 AngleXU=0 Radius=7 StartAngle=3.14159 EndAngle=6.28319
    g15: LineSegment StartX=-757 StartY=-45 StartZ=0 EndX=-757 EndY=5 EndZ=0
    g16: ArcOfCircle CenterX=-750 CenterY=5 CenterZ=0 NormalX=0 NormalY=0 NormalZ=1 AngleXU=0 Radius=7 StartAngle=2e-16 EndAngle=3.14159
    g17: LineSegment StartX=-593 StartY=5 StartZ=0 EndX=-593 EndY=-45 EndZ=0
    g18: ArcOfCircle CenterX=-600 CenterY=-45 CenterZ=0 NormalX=0 NormalY=0 NormalZ=1 AngleXU=0 Radius=7 StartAngle=3.14159 EndAngle=6.28319
    g19: LineSegment StartX=-607 StartY=-45 StartZ=0 EndX=-607 EndY=5 EndZ=0
    g20: ArcOfCircle CenterX=-600 CenterY=5 CenterZ=0 NormalX=0 NormalY=0 NormalZ=1 AngleXU=0 Radius=7 StartAngle=1e-16 EndAngle=3.14159
    g21: LineSegment [constr] StartX=-743 StartY=5 StartZ=0 EndX=-593 EndY=5 EndZ=0
    g22: LineSegment StartX=-443 StartY=5 StartZ=0 EndX=-443 EndY=-45 EndZ=0
    g23: ArcOfCircle CenterX=-450 CenterY=-45 CenterZ=0 NormalX=0 NormalY=0 NormalZ=1 AngleXU=0 Radius=7 StartAngle=3.14159 EndAngle=6.28319
    g24: LineSegment StartX=-457 StartY=-45 StartZ=0 EndX=-457 EndY=5 EndZ=0
    g25: ArcOfCircle CenterX=-450 CenterY=5 CenterZ=0 NormalX=0 NormalY=0 NormalZ=1 AngleXU=0 Radius=7 StartAngle=1e-16 EndAngle=3.14159
    g26: LineSegment [constr] StartX=-593 StartY=5 StartZ=0 EndX=-443 EndY=5 EndZ=0
    g27: LineSegment StartX=-293 StartY=5 StartZ=0 EndX=-293 EndY=-45 EndZ=0
    g28: ArcOfCircle CenterX=-300 CenterY=-45 CenterZ=0 NormalX=0 NormalY=0 NormalZ=1 AngleXU=0 Radius=7 StartAngle=3.14159 EndAngle=6.28319
    g29: LineSegment StartX=-307 StartY=-45 StartZ=0 EndX=-307 EndY=5 EndZ=0
    g30: ArcOfCircle CenterX=-300 CenterY=5 CenterZ=0 NormalX=0 NormalY=0 NormalZ=1 AngleXU=0 Radius=7 StartAngle=1e-16 EndAngle=3.14159
    g31: LineSegment [constr] StartX=-443 StartY=5 StartZ=0 EndX=-293 EndY=5 EndZ=0
    g32: LineSegment StartX=-143 StartY=5 StartZ=0 EndX=-143 EndY=-45 EndZ=0
    g33: ArcOfCircle CenterX=-150 CenterY=-45 CenterZ=0 NormalX=0 NormalY=0 NormalZ=1 AngleXU=0 Radius=7 StartAngle=3.14159 EndAngle=6.28319
    g34: LineSegment StartX=-157 StartY=-45 StartZ=0 EndX=-157 EndY=5 EndZ=0
    g35: ArcOfCircle CenterX=-150 CenterY=5 CenterZ=0 NormalX=0 NormalY=0 NormalZ=1 AngleXU=0 Radius=7 StartAngle=1e-16 EndAngle=3.14159
    g36: LineSegment [constr] StartX=-293 StartY=5 StartZ=0 EndX=-143 EndY=5 EndZ=0
    g37: LineSegment StartX=7 StartY=5 StartZ=0 EndX=7 EndY=-45 EndZ=0
    g38: ArcOfCircle CenterX=-3.42e-14 CenterY=-45 CenterZ=0 NormalX=0 NormalY=0 NormalZ=1 AngleXU=0 Radius=7 StartAngle=3.14159 EndAngle=6.28319
    g39: LineSegment StartX=-7 StartY=-45 StartZ=0 EndX=-7 EndY=5 EndZ=0
    g40: ArcOfCircle CenterX=-3.42e-14 CenterY=5 CenterZ=0 NormalX=0 NormalY=0 NormalZ=1 AngleXU=0 Radius=7 StartAngle=1e-16 EndAngle=3.14159
    g41: LineSegment [constr] StartX=-143 StartY=5 StartZ=0 EndX=7 EndY=5 EndZ=0
    g42: LineSegment StartX=157 StartY=5 StartZ=0 EndX=157 EndY=-45 EndZ=0
    g43: ArcOfCircle CenterX=150 CenterY=-45 CenterZ=0 NormalX=0 NormalY=0 NormalZ=1 AngleXU=0 Radius=7 StartAngle=3.14159 EndAngle=6.28319
    g44: LineSegment StartX=143 StartY=-45 StartZ=0 EndX=143 EndY=5 EndZ=0
    g45: ArcOfCircle CenterX=150 CenterY=5 CenterZ=0 NormalX=0 NormalY=0 NormalZ=1 AngleXU=0 Radius=7 StartAngle=1e-16 EndAngle=3.14159
    g46: LineSegment [constr] StartX=7 StartY=5 StartZ=0 EndX=157 EndY=5 EndZ=0
    g47: LineSegment StartX=307 StartY=5 StartZ=0 EndX=307 EndY=-45 EndZ=0
    g48: ArcOfCircle CenterX=300 CenterY=-45 CenterZ=0 NormalX=0 NormalY=0 NormalZ=1 AngleXU=0 Radius=7 StartAngle=3.14159 EndAngle=6.28319
    g49: LineSegment StartX=293 StartY=-45 StartZ=0 EndX=293 EndY=5 EndZ=0
    g50: ArcOfCircle CenterX=300 CenterY=5 CenterZ=0 NormalX=0 NormalY=0 NormalZ=1 AngleXU=0 Radius=7 StartAngle=1e-16 EndAngle=3.14159
    g51: LineSegment [constr] StartX=157 StartY=5 StartZ=0 EndX=307 EndY=5 EndZ=0
    g52: LineSegment StartX=457 StartY=5 StartZ=0 EndX=457 EndY=-45 EndZ=0
    g53: ArcOfCircle CenterX=450 CenterY=-45 CenterZ=0 NormalX=0 NormalY=0 NormalZ=1 AngleXU=0 Radius=7 StartAngle=3.14159 EndAngle=6.28319
    g54: LineSegment StartX=443 StartY=-45 StartZ=0 EndX=443 EndY=5 EndZ=0
    g55: ArcOfCircle CenterX=450 CenterY=5 CenterZ=0 NormalX=0 NormalY=0 NormalZ=1 AngleXU=0 Radius=7 StartAngle=2e-16 EndAngle=3.14159
    g56: LineSegment [constr] StartX=307 StartY=5 StartZ=0 EndX=457 EndY=5 EndZ=0
    g57: LineSegment StartX=607 StartY=5 StartZ=0 EndX=607 EndY=-45 EndZ=0
    g58: ArcOfCircle CenterX=600 CenterY=-45 CenterZ=0 NormalX=0 NormalY=0 NormalZ=1 AngleXU=0 Radius=7 StartAngle=3.14159 EndAngle=6.28319
    g59: LineSegment StartX=593 StartY=-45 StartZ=0 EndX=593 EndY=5 EndZ=0
    g60: ArcOfCircle CenterX=600 CenterY=5 CenterZ=0 NormalX=0 NormalY=0 NormalZ=1 AngleXU=0 Radius=7 StartAngle=1e-16 EndAngle=3.14159
    g61: LineSegment [constr] StartX=457 StartY=5 StartZ=0 EndX=607 EndY=5 EndZ=0
    g62: LineSegment StartX=757 StartY=5 StartZ=0 EndX=757 EndY=-45 EndZ=0
    g63: ArcOfCircle CenterX=750 CenterY=-45 CenterZ=0 NormalX=0 NormalY=0 NormalZ=1 AngleXU=0 Radius=7 StartAngle=3.14159 EndAngle=6.28319
    g64: LineSegment StartX=743 StartY=-45 StartZ=0 EndX=743 EndY=5 EndZ=0
    g65: ArcOfCircle CenterX=750 CenterY=5 CenterZ=0 NormalX=0 NormalY=0 NormalZ=1 AngleXU=0 Radius=7 StartAngle=1e-16 EndAngle=3.14159
    g66: LineSegment [constr] StartX=607 StartY=5 StartZ=0 EndX=757 EndY=5 EndZ=0
  constraints (160):
    c: Coincident(g0,g1)
    c: Coincident(g1,g2)
    c: Coincident(g2,g3)
    c: Coincident(g3,g0)
    c: Horizontal(g1)
    c: Horizontal(g3)
    c: Vertical(g0)
    c: Vertical(g2)
    c: Symmetric(g1,g0,g4)
    c: Coincident(g4,g-1)
    c: DistanceX(g1,g1) = 1600
    c: DistanceY(g2,g2) = 140
    c: Diameter(g5) = 14
    c: Diameter(g6) = 14
    c: DistanceX(g0,g5) = 100
    c: Distance(g5,g1) = 30
    c: Distance(g6,g1) = 30
    c: Equal(g5,g7) = 14
    c: Equal(g5,g8) = 14
    c: Equal(g5,g9) = 14
    c: Equal(g5,g10) = 14
    c: Equal(g5,g11) = 14
    c: Equal(g5,g12) = 14
    c: DistanceX(g5,g7) = 200
    c: DistanceX(g7,g8) = 200
    c: DistanceX(g8,g9) = 200
    c: DistanceX(g9,g6) = 200
    c: DistanceX(g6,g10) = 200
    c: DistanceX(g10,g11) = 200
    c: DistanceX(g11,g12) = 200
    c: Vertical(g13)
    c: Tangent(g13,g14) = 1.5708
    c: Vertical(g15)
    c: Tangent(g15,g16) = 1.5708
    c: DistanceY(g15,g15) = 50
    c: Tangent(g16,g13) = 1.5708
    c: Tangent(g14,g15) = 1.5708
    c: DistanceX(g15,g13) = 14
    c: Distance(g14,g3) = 25
    c: Distance(g14,g0) = 50
    c: Vertical(g17)
    c: Tangent(g17,g18) = 1.5708
    c: Vertical(g19)
    c: Tangent(g19,g20) = 1.5708
    c: Equal(g15,g19) = 50
    c: Tangent(g20,g17) = 1.5708
    c: Tangent(g18,g19) = 1.5708
    c: DistanceX(g19,g17) = 14
    c: Coincident(g13,g21)
    c: Coincident(g17,g21)
    c: Distance(g21) = 150
    c: Angle(g21) = 0
    c: Vertical(g22)
    c: Tangent(g22,g23) = 1.5708
    c: Vertical(g24)
    c: Tangent(g24,g25) = 1.5708
    c: Equal(g15,g24) = 50
    c: Tangent(g25,g22) = 1.5708
    c: Tangent(g23,g24) = 1.5708
    c: DistanceX(g24,g22) = 14
    c: Coincident(g17,g26)
    c: Coincident(g22,g26)
    c: Equal(g21,g26)
    c: Parallel(g26,g21)
    c: Vertical(g27)
    c: Tangent(g27,g28) = 1.5708
    c: Vertical(g29)
    c: Tangent(g29,g30) = 1.5708
    c: Equal(g15,g29) = 50
    c: Tangent(g30,g27) = 1.5708
    c: Tangent(g28,g29) = 1.5708
    c: DistanceX(g29,g27) = 14
    c: Coincident(g22,g31)
    c: Coincident(g27,g31)
    c: Equal(g21,g31)
    c: Parallel(g31,g21)
    c: Vertical(g32)
    c: Tangent(g32,g33) = 1.5708
    c: Vertical(g34)
    c: Tangent(g34,g35) = 1.5708
    c: Equal(g15,g34) = 50
    c: Tangent(g35,g32) = 1.5708
    c: Tangent(g33,g34) = 1.5708
    c: DistanceX(g34,g32) = 14
    c: Coincident(g27,g36)
    c: Coincident(g32,g36)
    c: Equal(g21,g36)
    c: Parallel(g36,g21)
    c: Vertical(g37)
    c: Tangent(g37,g38) = 1.5708
    c: Vertical(g39)
    c: Tangent(g39,g40) = 1.5708
    c: Equal(g15,g39) = 50
    c: Tangent(g40,g37) = 1.5708
    c: Tangent(g38,g39) = 1.5708
    c: DistanceX(g39,g37) = 14
    c: Coincident(g32,g41)
    c: Coincident(g37,g41)
    c: Equal(g21,g41)
    c: Parallel(g41,g21)
    c: Vertical(g42)
    c: Tangent(g42,g43) = 1.5708
    c: Vertical(g44)
    c: Tangent(g44,g45) = 1.5708
    c: Equal(g15,g44) = 50
    c: Tangent(g45,g42) = 1.5708
    c: Tangent(g43,g44) = 1.5708
    c: DistanceX(g44,g42) = 14
    c: Coincident(g37,g46)
    c: Coincident(g42,g46)
    c: Equal(g21,g46)
    c: Parallel(g46,g21)
    c: Vertical(g47)
    c: Tangent(g47,g48) = 1.5708
    c: Vertical(g49)
    c: Tangent(g49,g50) = 1.5708
    c: Equal(g15,g49) = 50
    c: Tangent(g50,g47) = 1.5708
    c: Tangent(g48,g49) = 1.5708
    c: DistanceX(g49,g47) = 14
    c: Coincident(g42,g51)
    c: Coincident(g47,g51)
    c: Equal(g21,g51)
    c: Parallel(g51,g21)
    c: Vertical(g52)
    c: Tangent(g52,g53) = 1.5708
    c: Vertical(g54)
    c: Tangent(g54,g55) = 1.5708
    c: Equal(g15,g54) = 50
    c: Tangent(g55,g52) = 1.5708
    c: Tangent(g53,g54) = 1.5708
    c: DistanceX(g54,g52) = 14
    c: Coincident(g47,g56)
    c: Coincident(g52,g56)
    c: Equal(g21,g56)
    c: Parallel(g56,g21)
    c: Vertical(g57)
    c: Tangent(g57,g58) = 1.5708
    c: Vertical(g59)
    c: Tangent(g59,g60) = 1.5708
    c: Equal(g15,g59) = 50
    c: Tangent(g60,g57) = 1.5708
    c: Tangent(g58,g59) = 1.5708
    c: DistanceX(g59,g57) = 14
    c: Coincident(g52,g61)
    c: Coincident(g57,g61)
    c: Equal(g21,g61)
    c: Parallel(g61,g21)
    c: Vertical(g62)
    c: Tangent(g62,g63) = 1.5708
    c: Vertical(g64)
    c: Tangent(g64,g65) = 1.5708
    c: Equal(g15,g64) = 50
    c: Tangent(g65,g62) = 1.5708
    c: Tangent(g63,g64) = 1.5708
    c: DistanceX(g64,g62) = 14
    c: Coincident(g57,g66)
    c: Coincident(g62,g66)
    c: Equal(g21,g66)
    c: Parallel(g66,g21)
FEATURE [Part::Extrusion] Extrude050  label="plate_1"
  Base = -> Sketch062
  Dir = (0,-1,2e-16)
  DirMode = 2
  FaceMakerClass = Part::FaceMakerBullseye
  FaceMakerMode = 3
  LengthFwd = 5
  LengthRev = 0
  Placement = pos=(1.14e-13,-2.99e-13,-80.4478) rot=(0,0,1;0rad)
  Solid = true
  Symmetric = false
FEATURE [Sketcher::SketchObject] Sketch063
  ArcFitTolerance = 0
  FullyConstrained = true
  MakeInternals = false
  Placement = pos=(0,0,0) rot=(1,0,0;1.5708rad)
  sketch-geometry (26):
    g0: LineSegment StartX=-800 StartY=-55 StartZ=0 EndX=-800 EndY=55 EndZ=0
    g1: LineSegment StartX=-800 StartY=55 StartZ=0 EndX=800 EndY=55 EndZ=0
    g2: LineSegment StartX=800 StartY=55 StartZ=0 EndX=800 EndY=-55 EndZ=0
    g3: LineSegment StartX=800 StartY=-55 StartZ=0 EndX=-800 EndY=-55 EndZ=0
    g4: GeomPoint [constr] X=0 Y=0 Z=0
    g5: Circle CenterX=-750 CenterY=25 CenterZ=0 NormalX=0 NormalY=0 NormalZ=1 AngleXU=0 Radius=7
    g6: Circle CenterX=-600 CenterY=25 CenterZ=0 NormalX=0 NormalY=0 NormalZ=1 AngleXU=0 Radius=7
    g7: LineSegment [constr] StartX=-750 StartY=25 StartZ=0 EndX=-600 EndY=25 EndZ=0
    g8: Circle CenterX=-450 CenterY=25 CenterZ=0 NormalX=0 NormalY=0 NormalZ=1 AngleXU=0 Radius=7
    g9: LineSegment [constr] StartX=-600 StartY=25 StartZ=0 EndX=-450 EndY=25 EndZ=0
    g10: Circle CenterX=-300 CenterY=25 CenterZ=0 NormalX=0 NormalY=0 NormalZ=1 AngleXU=0 Radius=7
    g11: LineSegment [constr] StartX=-450 StartY=25 StartZ=0 EndX=-300 EndY=25 EndZ=0
    g12: Circle CenterX=-150 CenterY=25 CenterZ=0 NormalX=0 NormalY=0 NormalZ=1 AngleXU=0 Radius=7
    g13: LineSegment [constr] StartX=-300 StartY=25 StartZ=0 EndX=-150 EndY=25 EndZ=0
    g14: Circle CenterX=1.11421e-10 CenterY=25 CenterZ=0 NormalX=0 NormalY=0 NormalZ=1 AngleXU=0 Radius=7
    g15: LineSegment [constr] StartX=-150 StartY=25 StartZ=0 EndX=1.11413e-10 EndY=25 EndZ=0
    g16: Circle CenterX=150 CenterY=25 CenterZ=0 NormalX=0 NormalY=0 NormalZ=1 AngleXU=0 Radius=7
    g17: LineSegment [constr] StartX=1.11421e-10 StartY=25 StartZ=0 EndX=150 EndY=25 EndZ=0
    g18: Circle CenterX=300 CenterY=25 CenterZ=0 NormalX=0 NormalY=0 NormalZ=1 AngleXU=0 Radius=7
    g19: LineSegment [constr] StartX=150 StartY=25 StartZ=0 EndX=300 EndY=25 EndZ=0
    g20: Circle CenterX=450 CenterY=25 CenterZ=0 NormalX=0 NormalY=0 NormalZ=1 AngleXU=0 Radius=7
    g21: LineSegment [constr] StartX=300 StartY=25 StartZ=0 EndX=450 EndY=25 EndZ=0
    g22: Circle CenterX=600 CenterY=25 CenterZ=0 NormalX=0 NormalY=0 NormalZ=1 AngleXU=0 Radius=7
    g23: LineSegment [constr] StartX=450 StartY=25 StartZ=0 EndX=600 EndY=25 EndZ=0
    g24: Circle CenterX=750 CenterY=25 CenterZ=0 NormalX=0 NormalY=0 NormalZ=1 AngleXU=0 Radius=7
    g25: LineSegment [constr] StartX=600 StartY=25 StartZ=0 EndX=750 EndY=25 EndZ=0
  constraints (65):
    c: Coincident(g0,g1)
    c: Coincident(g1,g2)
    c: Coincident(g2,g3)
    c: Coincident(g3,g0)
    c: Horizontal(g1)
    c: Horizontal(g3)
    c: Vertical(g0)
    c: Vertical(g2)
    c: Symmetric(g1,g0,g4)
    c: Coincident(g4,g-1)
    c: DistanceX(g1,g1) = 1600
    c: DistanceY(g2,g2) = 110
    c: Diameter(g5) = 14
    c: Distance(g5,g1) = 30
    c: Distance(g5,g0) = 50
    c: Equal(g5,g6) = 14
    c: Coincident(g5,g7)
    c: Coincident(g6,g7)
    c: Distance(g7) = 150
    c: Angle(g7) = 0
    c: Equal(g5,g8) = 14
    c: Coincident(g6,g9)
    c: Coincident(g8,g9)
    c: Equal(g7,g9)
    c: Parallel(g9,g7)
    c: Equal(g5,g10) = 14
    c: Coincident(g8,g11)
    c: Coincident(g10,g11)
    c: Equal(g7,g11)
    c: Parallel(g11,g7)
    c: Equal(g5,g12) = 14
    c: Coincident(g10,g13)
    c: Coincident(g12,g13)
    c: Equal(g7,g13)
    c: Parallel(g13,g7)
    c: Equal(g5,g14) = 14
    c: Coincident(g12,g15)
    c: Coincident(g14,g15)
    c: Equal(g7,g15)
    c: Parallel(g15,g7)
    c: Equal(g5,g16) = 14
    c: Coincident(g14,g17)
    c: Coincident(g16,g17)
    c: Equal(g7,g17)
    c: Parallel(g17,g7)
    c: Equal(g5,g18) = 14
    c: Coincident(g16,g19)
    c: Coincident(g18,g19)
    c: Equal(g7,g19)
    c: Parallel(g19,g7)
    c: Equal(g5,g20) = 14
    c: Coincident(g18,g21)
    c: Coincident(g20,g21)
    c: Equal(g7,g21)
    c: Parallel(g21,g7)
    c: Equal(g5,g22) = 14
    c: Coincident(g20,g23)
    c: Coincident(g22,g23)
    c: Equal(g7,g23)
    c: Parallel(g23,g7)
    c: Equal(g5,g24) = 14
    c: Coincident(g22,g25)
    c: Coincident(g24,g25)
    c: Equal(g7,g25)
    c: Parallel(g25,g7)
FEATURE [Part::Extrusion] Extrude051  label="rubberPlate"
  Base = -> Sketch063
  Dir = (0,-1,2e-16)
  DirMode = 2
  FaceMakerClass = Part::FaceMakerBullseye
  FaceMakerMode = 3
  LengthFwd = 10
  LengthRev = 0
  Placement = pos=(2.27e-13,-5,-125.45) rot=(0,0,1;0rad)
  Solid = true
  Symmetric = false
FEATURE [Sketcher::SketchObject] Sketch064
  ArcFitTolerance = 0
  FullyConstrained = true
  MakeInternals = false
  Placement = pos=(0,0,0) rot=(1,0,0;1.5708rad)
  sketch-geometry (26):
    g0: LineSegment StartX=-800 StartY=-25 StartZ=0 EndX=-800 EndY=25 EndZ=0
    g1: LineSegment StartX=-800 StartY=25 StartZ=0 EndX=800 EndY=25 EndZ=0
    g2: LineSegment StartX=800 StartY=25 StartZ=0 EndX=800 EndY=-25 EndZ=0
    g3: LineSegment StartX=800 StartY=-25 StartZ=0 EndX=-800 EndY=-25 EndZ=0
    g4: GeomPoint [constr] X=0 Y=0 Z=0
    g5: Circle CenterX=-750 CenterY=0 CenterZ=0 NormalX=0 NormalY=0 NormalZ=1 AngleXU=0 Radius=7
    g6: Circle CenterX=-600 CenterY=0 CenterZ=0 NormalX=0 NormalY=0 NormalZ=1 AngleXU=0 Radius=7
    g7: LineSegment [constr] StartX=-750 StartY=0 StartZ=0 EndX=-600 EndY=0 EndZ=0
    g8: Circle CenterX=-450 CenterY=0 CenterZ=0 NormalX=0 NormalY=0 NormalZ=1 AngleXU=0 Radius=7
    g9: LineSegment [constr] StartX=-600 StartY=0 StartZ=0 EndX=-450 EndY=0 EndZ=0
    g10: Circle CenterX=-300 CenterY=0 CenterZ=0 NormalX=0 NormalY=0 NormalZ=1 AngleXU=0 Radius=7
    g11: LineSegment [constr] StartX=-450 StartY=0 StartZ=0 EndX=-300 EndY=0 EndZ=0
    g12: Circle CenterX=-150 CenterY=0 CenterZ=0 NormalX=0 NormalY=0 NormalZ=1 AngleXU=0 Radius=7
    g13: LineSegment [constr] StartX=-300 StartY=0 StartZ=0 EndX=-150 EndY=0 EndZ=0
    g14: Circle CenterX=5.68e-14 CenterY=0 CenterZ=0 NormalX=0 NormalY=0 NormalZ=1 AngleXU=0 Radius=7
    g15: LineSegment [constr] StartX=-150 StartY=0 StartZ=0 EndX=5.68e-14 EndY=0 EndZ=0
    g16: Circle CenterX=150 CenterY=0 CenterZ=0 NormalX=0 NormalY=0 NormalZ=1 AngleXU=0 Radius=7
    g17: LineSegment [constr] StartX=5.68e-14 StartY=0 StartZ=0 EndX=150 EndY=0 EndZ=0
    g18: Circle CenterX=300 CenterY=0 CenterZ=0 NormalX=0 NormalY=0 NormalZ=1 AngleXU=0 Radius=7
    g19: LineSegment [constr] StartX=150 StartY=0 StartZ=0 EndX=300 EndY=0 EndZ=0
    g20: Circle CenterX=450 CenterY=0 CenterZ=0 NormalX=0 NormalY=0 NormalZ=1 AngleXU=0 Radius=7
    g21: LineSegment [constr] StartX=300 StartY=0 StartZ=0 EndX=450 EndY=0 EndZ=0
    g22: Circle CenterX=600 CenterY=0 CenterZ=0 NormalX=0 NormalY=0 NormalZ=1 AngleXU=0 Radius=7
    g23: LineSegment [constr] StartX=450 StartY=0 StartZ=0 EndX=600 EndY=0 EndZ=0
    g24: Circle CenterX=750 CenterY=0 CenterZ=0 NormalX=0 NormalY=0 NormalZ=1 AngleXU=0 Radius=7
    g25: LineSegment [constr] StartX=600 StartY=0 StartZ=0 EndX=750 EndY=0 EndZ=0
  constraints (65):
    c: Coincident(g0,g1)
    c: Coincident(g1,g2)
    c: Coincident(g2,g3)
    c: Coincident(g3,g0)
    c: Horizontal(g1)
    c: Horizontal(g3)
    c: Vertical(g0)
    c: Vertical(g2)
    c: Symmetric(g1,g0,g4)
    c: Coincident(g4,g-1)
    c: DistanceX(g1,g1) = 1600
    c: DistanceY(g2,g2) = 50
    c: PointOnObject(g5,g-1)
    c: Diameter(g5) = 14
    c: DistanceX(g0,g5) = 50
    c: Equal(g5,g6) = 14
    c: Coincident(g5,g7)
    c: Coincident(g6,g7)
    c: Distance(g7) = 150
    c: Angle(g7) = 0
    c: Equal(g5,g8) = 14
    c: Coincident(g6,g9)
    c: Coincident(g8,g9)
    c: Equal(g7,g9)
    c: Parallel(g9,g7)
    c: Equal(g5,g10) = 14
    c: Coincident(g8,g11)
    c: Coincident(g10,g11)
    c: Equal(g7,g11)
    c: Parallel(g11,g7)
    c: Equal(g5,g12) = 14
    c: Coincident(g10,g13)
    c: Coincident(g12,g13)
    c: Equal(g7,g13)
    c: Parallel(g13,g7)
    c: Equal(g5,g14) = 14
    c: Coincident(g12,g15)
    c: Coincident(g14,g15)
    c: Equal(g7,g15)
    c: Parallel(g15,g7)
    c: Equal(g5,g16) = 14
    c: Coincident(g14,g17)
    c: Coincident(g16,g17)
    c: Equal(g7,g17)
    c: Parallel(g17,g7)
    c: Equal(g5,g18) = 14
    c: Coincident(g16,g19)
    c: Coincident(g18,g19)
    c: Equal(g7,g19)
    c: Parallel(g19,g7)
    c: Equal(g5,g20) = 14
    c: Coincident(g18,g21)
    c: Coincident(g20,g21)
    c: Equal(g7,g21)
    c: Parallel(g21,g7)
    c: Equal(g5,g22) = 14
    c: Coincident(g20,g23)
    c: Coincident(g22,g23)
    c: Equal(g7,g23)
    c: Parallel(g23,g7)
    c: Equal(g5,g24) = 14
    c: Coincident(g22,g25)
    c: Coincident(g24,g25)
    c: Equal(g7,g25)
    c: Parallel(g25,g7)
FEATURE [Part::Extrusion] Extrude052  label="plate_2"
  Base = -> Sketch064
  Dir = (0,-1,2e-16)
  DirMode = 2
  FaceMakerClass = Part::FaceMakerBullseye
  FaceMakerMode = 3
  LengthFwd = 5
  LengthRev = 0
  Placement = pos=(0,-15,-100.45) rot=(0,0,1;0rad)
  Solid = true
  Symmetric = false
FEATURE [App::Part] Part024  label="blade"
  Group = -> [AngleSteel013,Extrude048,Extrude049,Sketch061,Cut020,Sketch062,Extrude050,Sketch063,Extrude051,Sketch064,Extrude052]
  Origin = -> Origin030
  Placement = pos=(750,0,0) rot=(0,0,1;5.49779rad)
  expr: .Placement.Base.x = Spreadsheet007.br
FEATURE [Part::FeaturePython] Array015  # Draft array (typed FeaturePython)
  AlwaysSyncPlacement = false
  Angle = 360
  ArrayType = 0
  Axis = (0,0,1)
  Base = -> Part024
  Center = (0,0,0)
  Count = 6
  ExpandArray = false
  Fuse = false
  IntervalAxis = (0,0,0)
  IntervalX = (1020,0,0)
  IntervalY = (0,100,0)
  IntervalZ = (0,0,100)
  NumberCircles = 3
  NumberPolar = 5
  NumberX = 6
  NumberY = 1
  NumberZ = 1
  PlacementList = 6 placements: arithmetic series from (750,0,0) step (1020,0,0) to (5850,0,0)
  RadialDistance = 50
  ScaleList = (6) [(1,1,1),(1,1,1),(1,1,1),(1,1,1),(1,1,1),(1,1,1)]
  Symmetry = 1
  TangentialDistance = 25
  expr: .IntervalX.x = Spreadsheet007.brs
  expr: NumberX = Spreadsheet007.n00
FEATURE [Part::Feature] Part__Feature007  label="7926A5 Inner ring"
  shape: bbox 24 x 167.8 x 167.8 mm, 8 faces (baked)
FEATURE [Part::Feature] Part__Feature008  label="7926A5 Outer ring"
  shape: bbox 24 x 194.8 x 194.8 mm, 8 faces (baked)
FEATURE [Part::Feature] Part__Feature009  label="7926A5 Ball"
  Placement = pos=(12,77.5,0) rot=(0,0,1;3.14159rad)
  shape: bbox 13.75 x 13.75 x 13.75 mm, 1 faces (baked)
FEATURE [Part::Feature] Part__Feature010  label="7926A5 Ball001"
  Placement = pos=(12,70.7998,31.5221) rot=(0,0,1;3.14159rad)
  shape: bbox 13.75 x 13.75 x 13.75 mm, 1 faces (baked)
FEATURE [Part::Feature] Part__Feature011  label="7926A5 Ball002"
  Placement = pos=(12,51.8576,57.5937) rot=(0,0,1;3.14159rad)
  shape: bbox 13.75 x 13.75 x 13.75 mm, 1 faces (baked)
FEATURE [Part::Feature] Part__Feature012  label="7926A5 Ball003"
  Placement = pos=(12,23.9488,73.7069) rot=(0,0,1;3.14159rad)
  shape: bbox 13.75 x 13.75 x 13.75 mm, 1 faces (baked)
FEATURE [Part::Feature] Part__Feature013  label="7926A5 Ball004"
  Placement = pos=(12,-8.10096,77.0754) rot=(0,0,1;3.14159rad)
  shape: bbox 13.75 x 13.75 x 13.75 mm, 1 faces (baked)
FEATURE [Part::Feature] Part__Feature014  label="7926A5 Ball005"
  Placement = pos=(12,-38.75,67.117) rot=(0,0,1;3.14159rad)
  shape: bbox 13.75 x 13.75 x 13.75 mm, 1 faces (baked)
FEATURE [Part::Feature] Part__Feature015  label="7926A5 Ball006"
  Placement = pos=(12,-62.6988,45.5534) rot=(0,0,1;3.14159rad)
  shape: bbox 13.75 x 13.75 x 13.75 mm, 1 faces (baked)
FEATURE [Part::Feature] Part__Feature016  label="7926A5 Ball007"
  Placement = pos=(12,-75.8064,16.1132) rot=(0,0,1;3.14159rad)
  shape: bbox 13.75 x 13.75 x 13.75 mm, 1 faces (baked)
FEATURE [Part::Feature] Part__Feature017  label="7926A5 Ball008"
  Placement = pos=(12,-75.8064,-16.1132) rot=(0,0,1;3.14159rad)
  shape: bbox 13.75 x 13.75 x 13.75 mm, 1 faces (baked)
FEATURE [Part::Feature] Part__Feature018  label="7926A5 Ball009"
  Placement = pos=(12,-62.6988,-45.5534) rot=(0,0,1;3.14159rad)
  shape: bbox 13.75 x 13.75 x 13.75 mm, 1 faces (baked)
FEATURE [Part::Feature] Part__Feature019  label="7926A5 Ball010"
  Placement = pos=(12,-38.75,-67.117) rot=(0,0,1;3.14159rad)
  shape: bbox 13.75 x 13.75 x 13.75 mm, 1 faces (baked)
FEATURE [Part::Feature] Part__Feature020  label="7926A5 Ball011"
  Placement = pos=(12,-8.10096,-77.0754) rot=(0,0,1;3.14159rad)
  shape: bbox 13.75 x 13.75 x 13.75 mm, 1 faces (baked)
FEATURE [Part::Feature] Part__Feature021  label="7926A5 Ball012"
  Placement = pos=(12,23.9488,-73.7069) rot=(0,0,1;3.14159rad)
  shape: bbox 13.75 x 13.75 x 13.75 mm, 1 faces (baked)
FEATURE [Part::Feature] Part__Feature022  label="7926A5 Ball013"
  Placement = pos=(12,51.8576,-57.5937) rot=(0,0,1;3.14159rad)
  shape: bbox 13.75 x 13.75 x 13.75 mm, 1 faces (baked)
FEATURE [Part::Feature] Part__Feature023  label="7926A5 Ball014"
  Placement = pos=(12,70.7998,-31.5221) rot=(0,0,1;3.14159rad)
  shape: bbox 13.75 x 13.75 x 13.75 mm, 1 faces (baked)
FEATURE [Part::Compound] Compound019
  Links = -> [Part__Feature007,Part__Feature008,Part__Feature009,Part__Feature010,Part__Feature011,Part__Feature012,Part__Feature013,Part__Feature014,Part__Feature015,Part__Feature016,Part__Feature017,Part__Feature018,Part__Feature019,Part__Feature020,Part__Feature021,Part__Feature022,Part__Feature023]
FEATURE [App::Part] NSK_7926A5
  Group = -> [Part__Feature007,Part__Feature008,Part__Feature009,Part__Feature010,Part__Feature011,Part__Feature012,Part__Feature013,Part__Feature014,Part__Feature015,Part__Feature016,Part__Feature017,Part__Feature018,Part__Feature019,Part__Feature020,Part__Feature021,Part__Feature022,Part__Feature023,Compound019]
  Origin = -> Origin039
  Placement = pos=(0,0,0) rot=(0,1,0;4.71239rad)
FEATURE [Sketcher::SketchObject] Sketch081
  ArcFitTolerance = 0
  AttachmentSupport = -> [XZ_Plane040]
  FullyConstrained = false
  MakeInternals = false
  MapMode = 5
  Placement = pos=(0,0,0) rot=(1,0,0;1.5708rad)
  sketch-geometry (6):
    g0: LineSegment StartX=90 StartY=28 StartZ=0 EndX=90 EndY=0 EndZ=0
    g1: LineSegment StartX=90 StartY=0 StartZ=0 EndX=84.9357 EndY=0 EndZ=0
    g2: LineSegment StartX=84.9357 StartY=0 StartZ=0 EndX=84.9357 EndY=-5 EndZ=0
    g3: LineSegment StartX=84.9357 StartY=-5 StartZ=0 EndX=110 EndY=-5 EndZ=0
    g4: LineSegment StartX=110 StartY=-5 StartZ=0 EndX=110 EndY=28 EndZ=0
    g5: LineSegment StartX=110 StartY=28 StartZ=0 EndX=90 EndY=28 EndZ=0
  constraints (17):
    c: PointOnObject(g0,g-1)
    c: Vertical(g0)
    c: Coincident(g0,g1)
    c: PointOnObject(g1,g-1)
    c: Coincident(g1,g2)
    c: Vertical(g2)
    c: Coincident(g2,g3)
    c: Horizontal(g3)
    c: Coincident(g3,g4)
    c: Vertical(g4)
    c: Coincident(g4,g5)
    c: Coincident(g5,g0)
    c: Horizontal(g5)
    c: DistanceX(g-1,g0) = 90
    c: DistanceY(g0,g0) = 28
    c: DistanceX(g-2,g4) = 110
    c: DistanceY(g2,g2) = 5
FEATURE [PartDesign::Revolution] Revolution003
  Angle = 360
  Angle2 = 60
  Axis = (0,2e-16,1)
  Base = (0,0,0)
  Placement = pos=(0,0,0) rot=(1,0,0;1.5708rad)
  Profile = -> Sketch081
  ReferenceAxis = -> Sketch081 [V_Axis]
  Reversed = true
  Suppressed = false
  Type = 0
FEATURE [PartDesign::Body] Body005
  AllowCompound = false
  Group = -> [Sketch081,Revolution003]
  Origin = -> Origin040
  Tip = -> Revolution003
FEATURE [Part::FeaturePython] Screw  label="M10x20-Screw"  # Fasteners workbench fastener (typed FeaturePython)
  Placement = pos=(100,0,28.046) rot=(0,0,1;0rad)
  diameter = 10
  invert = false
  leftHanded = false
  length = 0
  lengthCustom = 20
  matchOuter = false
  offset = 0
  thread = true
  type = 22
FEATURE [Part::FeaturePython] Array021  # Draft array (typed FeaturePython)
  AlwaysSyncPlacement = false
  Angle = 360
  ArrayType = 1
  Axis = (0,0,1)
  Base = -> Screw
  Center = (0,0,0)
  Count = 6
  ExpandArray = false
  Fuse = false
  IntervalAxis = (0,0,0)
  IntervalX = (50,0,0)
  IntervalY = (0,50,0)
  IntervalZ = (0,0,50)
  NumberCircles = 3
  NumberPolar = 6
  NumberX = 2
  NumberY = 2
  NumberZ = 1
  PlacementList = 6 placements: [(100,0,28.046),(50,86.6025,28.046),(-50,86.6025,28.046),(-100,1.22465e-14,28.046),(-50,-86.6025,28.046),(50,-86.6025,28.046)]
  RadialDistance = 50
  ScaleList = (6) [(1,1,1),(1,1,1),(1,1,1),(1,1,1),(1,1,1),(1,1,1)]
  Symmetry = 1
  TangentialDistance = 25
FEATURE [Part::Cut] Cut024
  Base = -> Body005
  Tool = -> Array021
FEATURE [Sketcher::SketchObject] Sketch082
  ArcFitTolerance = 0
  AttachmentSupport = -> [XZ_Plane041]
  FullyConstrained = true
  MakeInternals = false
  MapMode = 5
  Placement = pos=(0,0,0) rot=(1,0,0;1.5708rad)
  sketch-geometry (8):
    g0: LineSegment StartX=65 StartY=-272 StartZ=0 EndX=65 EndY=28 EndZ=0
    g1: LineSegment StartX=65 StartY=28 StartZ=0 EndX=70 EndY=28 EndZ=0
    g2: LineSegment StartX=70 StartY=28 StartZ=0 EndX=70 EndY=35 EndZ=0
    g3: LineSegment StartX=70 StartY=35 StartZ=0 EndX=65 EndY=35 EndZ=0
    g4: LineSegment StartX=65 StartY=35 StartZ=0 EndX=65 EndY=325 EndZ=0
    g5: LineSegment StartX=65 StartY=325 StartZ=0 EndX=0 EndY=325 EndZ=0
    g6: LineSegment StartX=0 StartY=325 StartZ=0 EndX=0 EndY=-272 EndZ=0
    g7: LineSegment StartX=0 StartY=-272 StartZ=0 EndX=65 EndY=-272 EndZ=0
  constraints (24):
    c: Vertical(g0)
    c: Coincident(g0,g1)
    c: Horizontal(g1)
    c: Coincident(g1,g2)
    c: Vertical(g2)
    c: Coincident(g2,g3)
    c: Coincident(g3,g4)
    c: Vertical(g4)
    c: Coincident(g4,g5)
    c: Horizontal(g5)
    c: Coincident(g5,g6)
    c: Vertical(g6)
    c: Coincident(g6,g7)
    c: Horizontal(g7)
    c: Horizontal(g3)
    c: DistanceY(g2,g2) = 7
    c: DistanceX(g5,g5) = 65
    c: DistanceX(g3,g3) = 5
    c: Vertical(g3,g0)
    c: PointOnObject(g5,g-2)
    c: DistanceY(g-1,g0) = 28
    c: DistanceY(g4,g4) = 290
    c: Coincident(g0,g7)
    c: DistanceY(g0,g0) = 300
FEATURE [PartDesign::Revolution] Revolution004
  Angle = 360
  Angle2 = 60
  Axis = (0,2e-16,1)
  Base = (0,0,0)
  Placement = pos=(0,0,0) rot=(1,0,0;1.5708rad)
  Profile = -> Sketch082
  ReferenceAxis = -> Sketch082 [V_Axis]
  Reversed = true
  Suppressed = false
  Type = 0
FEATURE [PartDesign::Body] Body006  label="shaft001"
  AllowCompound = false
  Group = -> [Sketch082,Revolution004]
  Origin = -> Origin041
  Tip = -> Revolution004
FEATURE [Sketcher::SketchObject] Sketch083
  ArcFitTolerance = 0
  AttachmentSupport = -> [XZ_Plane042]
  FullyConstrained = false
  MakeInternals = false
  MapMode = 5
  Placement = pos=(0,0,0) rot=(1,0,0;1.5708rad)
  sketch-geometry (12):
    g0: LineSegment StartX=90 StartY=28 StartZ=0 EndX=110 EndY=28 EndZ=0
    g1: LineSegment StartX=110 StartY=28 StartZ=0 EndX=110 EndY=38 EndZ=0
    g2: LineSegment StartX=110 StartY=38 StartZ=0 EndX=90 EndY=38 EndZ=0
    g3: LineSegment StartX=90 StartY=38 StartZ=0 EndX=90 EndY=58 EndZ=0
    g4: LineSegment StartX=90 StartY=58 StartZ=0 EndX=80 EndY=58 EndZ=0
    g5: LineSegment StartX=74.4009 StartY=44 StartZ=0 EndX=74.4009 EndY=39 EndZ=0
    g6: LineSegment StartX=74.4009 StartY=39 StartZ=0 EndX=86 EndY=39 EndZ=0
    g7: LineSegment StartX=86 StartY=39 StartZ=0 EndX=86 EndY=24 EndZ=0
    g8: LineSegment StartX=86 StartY=24 StartZ=0 EndX=90 EndY=24 EndZ=0
    g9: LineSegment StartX=90 StartY=24 StartZ=0 EndX=90 EndY=28 EndZ=0
    g10: LineSegment StartX=74.4009 StartY=44 StartZ=0 EndX=80 EndY=44 EndZ=0
    g11: LineSegment StartX=80 StartY=44 StartZ=0 EndX=80 EndY=58 EndZ=0
  constraints (35):
    c: Horizontal(g0)
    c: Coincident(g0,g1)
    c: Vertical(g1)
    c: Coincident(g1,g2)
    c: Horizontal(g2)
    c: Coincident(g2,g3)
    c: Vertical(g3)
    c: Coincident(g3,g4)
    c: Horizontal(g4)
    c: Vertical(g5)
    c: Coincident(g5,g6)
    c: Horizontal(g6)
    c: Coincident(g6,g7)
    c: Vertical(g7)
    c: Coincident(g7,g8)
    c: Horizontal(g8)
    c: Coincident(g8,g9)
    c: Coincident(g9,g0)
    c: Vertical(g9)
    c: Horizontal(g10)
    c: Coincident(g10,g11)
    c: Vertical(g11)
    c: Coincident(g4,g11)
    c: Coincident(g5,g10)
    c: DistanceX(g8,g8) = 4
    c: DistanceX(g-2,g8) = 90
    c: DistanceY(g9,g9) = 4
    c: DistanceY(g-1,g0) = 28
    c: Vertical(g0,g2)
    c: DistanceX(g-1,g0) = 110
    c: DistanceY(g5,g5) = 5
    c: DistanceY(g7,g7) = 15
    c: DistanceY(g1,g1) = 10
    c: DistanceX(g-1,g10) = 80
    c: DistanceY(g3,g3) = 20
FEATURE [PartDesign::Revolution] Revolution005
  Angle = 360
  Angle2 = 60
  Axis = (0,2e-16,1)
  Base = (0,0,0)
  Placement = pos=(0,0,0) rot=(1,0,0;1.5708rad)
  Profile = -> Sketch083
  ReferenceAxis = -> Sketch083 [V_Axis]
  Reversed = true
  Suppressed = false
  Type = 0
FEATURE [Sketcher::SketchObject] Sketch084
  ArcFitTolerance = 0
  AttachmentSupport = -> [Revolution005]
  FullyConstrained = true
  MakeInternals = false
  MapMode = 5
  Placement = pos=(0,1.67e-14,38) rot=(0,0,1;3.14159rad)
  sketch-geometry (1):
    g0: Circle CenterX=100 CenterY=0 CenterZ=0 NormalX=0 NormalY=0 NormalZ=1 AngleXU=0 Radius=6
  constraints (3):
    c: PointOnObject(g0,g-1)
    c: Diameter(g0) = 12
    c: DistanceX(g-1,g0) = 100
FEATURE [PartDesign::Pocket] Pocket002
  BaseFeature = -> Revolution005
  Direction = (0,0,-1)
  Length = 5
  Length2 = 5
  Placement = pos=(0,0,0) rot=(1,0,0;1.5708rad)
  Profile = -> Sketch084
  ReferenceAxis = -> Sketch084 [N_Axis]
  Suppressed = false
  Type = 1
FEATURE [PartDesign::PolarPattern] PolarPattern
  Angle = 360
  Axis = -> Sketch084 [N_Axis]
  BaseFeature = -> Pocket002
  Mode = 0
  Occurrences = 6
  Offset = 120
  Originals = -> [Pocket002]
  Placement = pos=(0,0,0) rot=(1,0,0;1.5708rad)
  Suppressed = false
  TransformMode = 0
FEATURE [PartDesign::Body] Body007  label="oilsealCover"
  AllowCompound = false
  Group = -> [Sketch083,Revolution005,Sketch084,Pocket002,PolarPattern]
  Origin = -> Origin042
  Tip = -> PolarPattern
FEATURE [Sketcher::SketchObject] Sketch085
  ArcFitTolerance = 0
  ExternalGeometry = -> [Cut024]
  FullyConstrained = true
  MakeInternals = false
  Placement = pos=(0,0,0) rot=(1,0,0;1.5708rad)
  sketch-geometry (4):
    g0: LineSegment StartX=110 StartY=0 StartZ=0 EndX=210 EndY=0 EndZ=0
    g1: LineSegment StartX=210 StartY=0 StartZ=0 EndX=210 EndY=15 EndZ=0
    g2: LineSegment StartX=210 StartY=15 StartZ=0 EndX=110 EndY=15 EndZ=0
    g3: LineSegment StartX=110 StartY=15 StartZ=0 EndX=110 EndY=0 EndZ=0
  constraints (12):
    c: Coincident(g0,g1)
    c: Coincident(g1,g2)
    c: Coincident(g2,g3)
    c: Coincident(g3,g0)
    c: Horizontal(g0)
    c: Horizontal(g2)
    c: Vertical(g1)
    c: Vertical(g3)
    c: PointOnObject(g0,g-1)
    c: PointOnObject(g0,g-3)
    c: DistanceX(g2,g2) = 100
    c: DistanceY(g1,g1) = 15
FEATURE [Part::Revolution] Revolve009
  Angle = 360
  Axis = (0,0,1)
  Base = (0,0,0)
  FaceMakerClass = Part::FaceMakerBullseye
  Solid = true
  Source = -> Sketch085
  Symmetric = false
FEATURE [Sketcher::SketchObject] Sketch086
  ArcFitTolerance = 0
  AttachmentSupport = -> [XZ_Plane044]
  FullyConstrained = true
  MakeInternals = false
  MapMode = 5
  Placement = pos=(0,0,0) rot=(1,0,0;1.5708rad)
  expr: Constraints[12] = Spreadsheet010.b0
  expr: Constraints[13] = Spreadsheet010.h0
  expr: Constraints[14] = Spreadsheet010.r1
  expr: Constraints[15] = Spreadsheet010.b0 * 0.67
  expr: Constraints[16] = Spreadsheet010.b0 * 0.16
  expr: Constraints[17] = Spreadsheet010.b0 * 0.65
  expr: Constraints[18] = Spreadsheet010.h0 * 0.07
  expr: Constraints[19] = Spreadsheet010.h0 * 0.1
  expr: Constraints[20] = Spreadsheet010.b0 * 0.29
  expr: Constraints[21] = Spreadsheet010.h0 * 0.114
  expr: Constraints[22] = Spreadsheet010.h0 * 0.19
  expr: Constraints[23] = Spreadsheet010.h0 * 0.335
  expr: Constraints[24] = Spreadsheet010.b0 * 0.163
  expr: Constraints[25] = Spreadsheet010.b0 * 0.316
  expr: Constraints[26] = Spreadsheet010.b0 * 0.38
  expr: Constraints[27] = Spreadsheet010.h0 * 0.317
  expr: Constraints[28] = Spreadsheet010.b0 * 0.126
  expr: Constraints[29] = Spreadsheet010.b0 * 0.099
  expr: Constraints[30] = Spreadsheet010.b0 * 0.22
  expr: Constraints[31] = Spreadsheet010.h0 * 0.217
  expr: Constraints[32] = Spreadsheet010.h0 * 0.122
  expr: Constraints[44] = Spreadsheet010.h0 * 0.289
  expr: Constraints[45] = Spreadsheet010.h0 * 0.339
  sketch-geometry (15):
    g0: LineSegment StartX=10.08 StartY=80 StartZ=0 EndX=12 EndY=78.17 EndZ=0
    g1: LineSegment StartX=12 StartY=78.17 StartZ=0 EndX=11.4818 EndY=67.46 EndZ=0
    g2: LineSegment StartX=11.4818 StartY=67.46 StartZ=0 EndX=6.92177 EndY=67.46 EndZ=0
    g3: LineSegment StartX=6.92177 StartY=67.46 StartZ=0 EndX=3.12977 EndY=65 EndZ=0
    g4: LineSegment StartX=1.17377 StartY=71.405 StartZ=0 EndX=2.68577 EndY=71.405 EndZ=0
    g5: LineSegment StartX=5.88 StartY=70.085 StartZ=0 EndX=8.52 EndY=70.715 EndZ=0
    g6: LineSegment StartX=8.52 StartY=70.715 StartZ=0 EndX=8.52 EndY=75.74 EndZ=0
    g7: LineSegment StartX=8.52 StartY=75.74 StartZ=0 EndX=0.72 EndY=75.74 EndZ=0
    g8: LineSegment StartX=0.72 StartY=75.74 StartZ=0 EndX=1e-16 EndY=76.79 EndZ=0
    g9: LineSegment StartX=0 StartY=76.79 StartZ=0 EndX=0 EndY=78.29 EndZ=0
    g10: LineSegment StartX=0 StartY=78.29 StartZ=0 EndX=2.04 EndY=80 EndZ=0
    g11: ArcOfCircle CenterX=3.87377 CenterY=69.755 CenterZ=0 NormalX=0 NormalY=0 NormalZ=1 AngleXU=0 Radius=2.03319 StartAngle=0.163028 EndAngle=2.19482
    g12: LineSegment StartX=2.04 StartY=80 StartZ=0 EndX=10.08 EndY=80 EndZ=0
    g13: LineSegment StartX=1.17377 StartY=68.555 StartZ=0 EndX=1.17377 EndY=71.405 EndZ=0
    g14: LineSegment StartX=3.12977 StartY=65 StartZ=0 EndX=1.17377 EndY=68.555 EndZ=0
  constraints (46):
    c: Horizontal(g2)
    c: Coincident(g2,g3)
    c: Coincident(g6,g7)
    c: Horizontal(g7)
    c: Coincident(g7,g8)
    c: PointOnObject(g8,g-2)
    c: Coincident(g8,g9)
    c: PointOnObject(g9,g-2)
    c: Coincident(g9,g10)
    c: Coincident(g12,g10)
    c: Coincident(g12,g0)
    c: Horizontal(g12)
    c: DistanceX(g9,g0) = 12
    c: DistanceY(g3,g10) = 15
    c: DistanceY(g-1,g3) = 65
    c: DistanceX(g12,g12) = 8.04
    c: DistanceX(g0,g0) = 1.92
    c: DistanceX(g7,g7) = 7.8
    c: DistanceY(g7,g8) = 1.05
    c: DistanceY(g9,g9) = 1.5
    c: DistanceX(g6,g0) = 3.48
    c: DistanceY(g9,g10) = 1.71
    c: DistanceY(g13,g13) = 2.85
    c: DistanceY(g6,g6) = 5.025
    c: DistanceX(g4,g3) = 1.956
    c: DistanceX(g3,g2) = 3.792
    c: DistanceX(g2,g2) = 4.56
    c: DistanceY(g3,g11) = 4.755
    c: DistanceX(g4,g4) = 1.512
    c: DistanceX(g4,g11) = 1.188
    c: DistanceX(g5,g5) = 2.64
    c: DistanceY(g2,g6) = 3.255
    c: DistanceY(g0,g0) = 1.83
    c: Coincident(g11,g4)
    c: Coincident(g6,g5)
    c: Coincident(g11,g5)
    c: Coincident(g4,g13)
    c: Vertical(g13)
    c: Coincident(g13,g14)
    c: Horizontal(g4)
    c: Vertical(g6)
    c: Coincident(g14,g3)
    c: Coincident(g1,g2)
    c: Coincident(g1,g0)
    c: DistanceY(g4,g7) = 4.335
    c: DistanceY(g3,g5) = 5.085
FEATURE [Spreadsheet::Sheet] Spreadsheet010
  cells = A1='name; B1='130 160 12; A2='d1; B2(d1)=130; A3='D0; B3(D0)=160; A4='b0; B4(b0)=12; A5='r1=d1/2; B5(r1)==d1 / 2; A6='R0=D0/2; B6(R0)==D0 / 2; A7='h0=(D0-d1)/2; B7(h0)==(D0 - d1) / 2
FEATURE [PartDesign::Revolution] Revolution006
  Angle = 360
  Angle2 = 60
  Axis = (1,0,0)
  Base = (0,0,0)
  Placement = pos=(0,0,0) rot=(1,0,0;1.5708rad)
  Profile = -> Sketch086
  ReferenceAxis = -> Sketch086 [H_Axis]
  Suppressed = false
  Type = 0
FEATURE [PartDesign::Body] Body008  label="Oilseal"
  AllowCompound = false
  Group = -> [Sketch086,Revolution006]
  Origin = -> Origin044
  Placement = pos=(0,0,0) rot=(0,-1,0;1.5708rad)
  Tip = -> Revolution006
FEATURE [App::Part] Part032  label="oilseal"
  Group = -> [Body008,Spreadsheet010]
  Origin = -> Origin045
  Placement = pos=(0,0,44) rot=(0,0,1;0rad)
FEATURE [Part::FeaturePython] __basic  # WARN: FeaturePython — macro-defined, semantics opaque (R4)
  D = 300
  I = 32460.7
  L = 520
  g0 = 7.85
  mass = 288.54
  type = 0_basic
  expr: D = Spreadsheet011.D
  expr: L = Spreadsheet011.L
FEATURE [Part::FeaturePython] __keyway_boss  # WARN: FeaturePython — macro-defined, semantics opaque (R4)
  D = 130
  g0 = 7.85
  mass = 0
  expr: D = Spreadsheet011.d
FEATURE [Part::Extrusion] Extrude066  label="Extrude069"
  Base = -> __keyway_boss
  Dir = (1,0,0)
  DirMode = 2
  FaceMakerClass = Part::FaceMakerBullseye
  FaceMakerMode = 3
  LengthFwd = 520
  LengthRev = 0
  Solid = false
  Symmetric = false
  expr: LengthFwd = Spreadsheet011.L
FEATURE [Part::Cut] Cut025
  Base = -> __basic
  Tool = -> Extrude066
FEATURE [Sketcher::SketchObject] Sketch087
  ArcFitTolerance = 0
  FullyConstrained = true
  MakeInternals = false
  Placement = pos=(0,0,0) rot=(0.57735,-0.57735,-0.57735;2.0944rad)
  expr: Constraints[10] = Spreadsheet011.E
  expr: Constraints[9] = Spreadsheet011.D
  sketch-geometry (4):
    g0: LineSegment StartX=-150 StartY=-1 StartZ=0 EndX=150 EndY=-1 EndZ=0
    g1: LineSegment StartX=150 StartY=-1 StartZ=0 EndX=150 EndY=1 EndZ=0
    g2: LineSegment StartX=150 StartY=1 StartZ=0 EndX=-150 EndY=1 EndZ=0
    g3: LineSegment StartX=-150 StartY=1 StartZ=0 EndX=-150 EndY=-1 EndZ=0
  constraints (11):
    c: Coincident(g0,g1)
    c: Coincident(g1,g2)
    c: Coincident(g2,g3)
    c: Coincident(g3,g0)
    c: Horizontal(g0)
    c: Horizontal(g2)
    c: Vertical(g1)
    c: Vertical(g3)
    c: Symmetric(g1,g0,g-1)
    c: DistanceX(g2,g2) = 300
    c: DistanceY(g3,g3) = 2
FEATURE [Part::Extrusion] Extrude067  label="Extrude070"
  Base = -> Sketch087
  Dir = (-1,0,0)
  DirMode = 2
  FaceMakerClass = Part::FaceMakerBullseye
  FaceMakerMode = 3
  LengthFwd = 520
  LengthRev = 0
  Reversed = true
  Solid = true
  Symmetric = false
  expr: LengthFwd = Spreadsheet011.L
FEATURE [Part::Cut] Cut026
  Base = -> Cut025
  Tool = -> Extrude067
FEATURE [Sketcher::SketchObject] Sketch088
  ArcFitTolerance = 0
  FullyConstrained = true
  MakeInternals = false
  Placement = pos=(0,0,59) rot=(0,0,1;0rad)
  expr: .Placement.Base.z = Spreadsheet011.C0 + Spreadsheet011.E / 2
  expr: Constraints[10] = Spreadsheet011.F0
  expr: Constraints[6] = Spreadsheet011.A0 / 2
  expr: Constraints[8] = Spreadsheet011.H0
  expr: Constraints[9] = Spreadsheet011.D / 2
  sketch-geometry (4):
    g0: LineSegment StartX=24.5 StartY=150 StartZ=0 EndX=24.5 EndY=91.5 EndZ=0
    g1: ArcOfCircle CenterX=65 CenterY=91.5 CenterZ=0 NormalX=0 NormalY=0 NormalZ=1 AngleXU=0 Radius=40.5 StartAngle=3.14159 EndAngle=6.28319
    g2: LineSegment StartX=105.5 StartY=91.5 StartZ=0 EndX=105.5 EndY=150 EndZ=0
    g3: LineSegment StartX=105.5 StartY=150 StartZ=0 EndX=24.5 EndY=150 EndZ=0
  constraints (11):
    c: Vertical(g0)
    c: Tangent(g0,g1) = -1.5708
    c: Coincident(g2,g3)
    c: Coincident(g3,g0)
    c: Horizontal(g3)
    c: Vertical(g2)
    c: DistanceY(g-1,g1) = 91.5
    c: Tangent(g1,g2) = -1.5708
    c: DistanceX(g3,g3) = 81
    c: DistanceY(g-1,g0) = 150
    c: DistanceX(g-1,g1) = 65
FEATURE [Part::Extrusion] Extrude068  label="Extrude071"
  Base = -> Sketch088
  Dir = (0,0,1)
  DirMode = 2
  FaceMakerClass = Part::FaceMakerBullseye
  FaceMakerMode = 3
  LengthFwd = 180
  LengthRev = 0
  Solid = true
  Symmetric = false
  expr: LengthFwd = Spreadsheet011.D * 0.6
FEATURE [Sketcher::SketchObject] Sketch089
  ArcFitTolerance = 0
  FullyConstrained = true
  MakeInternals = false
  expr: Constraints[0] = Spreadsheet011.F0
  expr: Constraints[1] = Spreadsheet011.S0
  expr: Constraints[2] = Spreadsheet011.A0 / 2
  sketch-geometry (1):
    g0: Circle CenterX=65 CenterY=91.5 CenterZ=0 NormalX=0 NormalY=0 NormalZ=1 AngleXU=0 Radius=17.5
  constraints (3):
    c: DistanceX(g-1,g0) = 65
    c: Diameter(g0) = 35
    c: DistanceY(g-1,g0) = 91.5
FEATURE [Part::Extrusion] Extrude069  label="Extrude072"
  Base = -> Sketch089
  Dir = (0,0,1)
  DirMode = 2
  FaceMakerClass = Part::FaceMakerBullseye
  FaceMakerMode = 3
  LengthFwd = 118
  LengthRev = 0
  Solid = true
  Symmetric = true
  expr: LengthFwd = Spreadsheet011.C0 * 2 + Spreadsheet011.E
FEATURE [Part::FeaturePython] Array022  label="BoltHoles"  # Draft array (typed FeaturePython)
  Angle = 360
  ArrayType = 0
  Axis = (0,0,1)
  Base = -> Extrude069
  Center = (0,0,0)
  Count = 16
  Fuse = false
  IntervalAxis = (0,0,0)
  IntervalX = (130,0,0)
  IntervalY = (0,-183,0)
  IntervalZ = (0,0,59)
  NumberCircles = 3
  NumberPolar = 5
  NumberX = 8
  NumberY = 2
  NumberZ = 1
  RadialDistance = 50
  Symmetry = 1
  TangentialDistance = 25
  expr: .IntervalX.x = Spreadsheet011.G0
  expr: .IntervalY.y = -Spreadsheet011.A0
  expr: .IntervalZ.z = Spreadsheet011.C0 + Spreadsheet011.E / 2
  expr: NumberX = Spreadsheet011.BoltNo
FEATURE [Spreadsheet::Sheet] Spreadsheet011
  cells = B2=130; A3='d; B3(d)=130; A4='D; B4(D)=300; A5='L; B5(L)=520; A6='A0; B6(A0)=183; A7='B; B7(B)=101; A8='C0; B8(C0)=58; A9='E; B9(E)=2; A10='F0; B10(F0)=65; A11='G0; B11(G0)=130; A12='H0; B12(H0)=81; A13='S0; B13(S0)=35; A14='BoltNo; B14(BoltNo)=8; A15='BoltSize; B15(BoltSize)='M32; A16='BoltL; B16(BoltL)==2 * B8 + B9 + B13
FEATURE [Part::FeaturePython] Array023  # Draft array (typed FeaturePython)
  Angle = 360
  ArrayType = 0
  Axis = (0,0,1)
  Base = -> Extrude068
  Center = (0,0,0)
  Count = 4
  Fuse = false
  IntervalAxis = (0,0,0)
  IntervalX = (130,0,0)
  IntervalY = (0,1,0)
  IntervalZ = (0,0,50)
  NumberCircles = 3
  NumberPolar = 5
  NumberX = 4
  NumberY = 1
  NumberZ = 1
  RadialDistance = 50
  Symmetry = 1
  TangentialDistance = 25
  expr: .IntervalX.x = Spreadsheet011.G0
  expr: NumberX = Spreadsheet011.BoltNo / 2
FEATURE [Part::Mirroring] mirror  label="Array (mirrored) "
  Base = (-1000,0,0)
  Normal = (0,-1,0)
  Source = -> Array023
FEATURE [Part::MultiFuse] Fusion005
  Shapes = -> [mirror,Array023]
FEATURE [Part::Mirroring] mirror001  label="Fusion (mirrored) "
  Base = (-1000,0,0)
  Normal = (0,0,-1)
  Source = -> Fusion005
FEATURE [Part::MultiFuse] Fusion006
  Shapes = -> [mirror001,Fusion005]
FEATURE [Part::Cut] Cut027
  Base = -> Cut026
  Tool = -> Fusion006
FEATURE [Part::Cut] Cut004  label="SplitTubeJoint"
  Base = -> Cut027
  Tool = -> Array022
FEATURE [App::Part] Part033  label="筒割形継手"
  Group = -> [__keyway_boss,Sketch088,Array022,__basic,Extrude067,Extrude068,Extrude069,Extrude066,Cut025,Cut026,Sketch087,Sketch089,Spreadsheet011,Array023,mirror,Fusion005,mirror001,Fusion006,Cut027,Cut004]
  Origin = -> Origin046
  Placement = pos=(-1.56e-14,0,70.092) rot=(0,1,0;4.71239rad)
FEATURE [Part::FeaturePython] Clone016  label="筒割形継手001"  # Draft clone (typed FeaturePython)
  AttacherType = Attacher::AttachEngine3D
  Fuse = false
  Objects = -> [Part033]
  Placement = pos=(1.2e-13,0,-533.21) rot=(0,-1,0;1.5708rad)
  Scale = (1,1,1)
FEATURE [Sketcher::SketchObject] Sketch090
  ArcFitTolerance = 0
  AttachmentSupport = -> [Revolve009]
  FullyConstrained = false
  MakeInternals = false
  MapMode = 5
  Placement = pos=(0,0,15) rot=(0,0,1;0rad)
  sketch-geometry (1):
    g0: Circle CenterX=185 CenterY=-0.1655 CenterZ=0 NormalX=0 NormalY=0 NormalZ=1 AngleXU=0 Radius=9.5
  constraints (2):
    c: Diameter(g0) = 19
    c: DistanceX(g-1,g0) = 185
FEATURE [Part::Extrusion] Extrude070  label="Extrude073"
  Base = -> Sketch090
  Dir = (0,0,1)
  DirMode = 2
  FaceMakerClass = Part::FaceMakerBullseye
  FaceMakerMode = 3
  LengthFwd = 30
  LengthRev = 0
  Reversed = true
  Solid = true
  Symmetric = false
FEATURE [Part::FeaturePython] Array024  # Draft array (typed FeaturePython)
  AlwaysSyncPlacement = false
  Angle = 360
  ArrayType = 1
  Axis = (0,0,1)
  Base = -> Extrude070
  Center = (0,0,590.09)
  Count = 6
  ExpandArray = false
  Fuse = false
  IntervalAxis = (0,0,0)
  IntervalX = (50,0,0)
  IntervalY = (0,50,0)
  IntervalZ = (0,0,50)
  NumberCircles = 3
  NumberPolar = 6
  NumberX = 2
  NumberY = 2
  NumberZ = 1
  PlacementList = 6 placements: [(0,0,0),(0,0,0),(0,0,0),(0,0,0),(0,0,1.13687e-13),(0,0,0)]
  RadialDistance = 50
  ScaleList = (6) [(1,1,1),(1,1,1),(1,1,1),(1,1,1),(1,1,1),(1,1,1)]
  Symmetry = 1
  TangentialDistance = 25
FEATURE [Part::Cut] Cut005
  Base = -> Revolve009
  Tool = -> Array024
FEATURE [App::Part] Part031  label="house"
  Group = -> [Cut024,Body005,Revolve009,Extrude070,Array024,Screw,Array021,Sketch085,Sketch090,Cut005]
  Origin = -> Origin043
FEATURE [Part::Feature] Part__Feature024  label="減速機 v2"
  Placement = pos=(0,-7.2e-14,324.85) rot=(1,0,0;1.5708rad)
  shape: bbox 550 x 550 x 1097 mm, 38 faces (baked)
FEATURE [Sketcher::SketchObject] Sketch091
  ArcFitTolerance = 0
  FullyConstrained = true
  MakeInternals = false
  Placement = pos=(0,0,0) rot=(1,0,0;1.5708rad)
  sketch-geometry (12):
    g0: LineSegment StartX=170 StartY=0 StartZ=0 EndX=400 EndY=0 EndZ=0
    g1: LineSegment StartX=400 StartY=0 StartZ=0 EndX=400 EndY=-20 EndZ=0
    g2: LineSegment StartX=400 StartY=-20 StartZ=0 EndX=170 EndY=-20 EndZ=0
    g3: LineSegment StartX=170 StartY=-20 StartZ=0 EndX=170 EndY=0 EndZ=0
    g4: LineSegment StartX=250 StartY=625 StartZ=0 EndX=345 EndY=625 EndZ=0
    g5: LineSegment StartX=345 StartY=625 StartZ=0 EndX=345 EndY=595 EndZ=0
    g6: LineSegment StartX=345 StartY=595 StartZ=0 EndX=250 EndY=595 EndZ=0
    g7: LineSegment StartX=250 StartY=595 StartZ=0 EndX=250 EndY=625 EndZ=0
    g8: LineSegment StartX=245 StartY=595 StartZ=0 EndX=257 EndY=595 EndZ=0
    g9: LineSegment StartX=257 StartY=595 StartZ=0 EndX=257 EndY=0 EndZ=0
    g10: LineSegment StartX=257 StartY=0 StartZ=0 EndX=245 EndY=0 EndZ=0
    g11: LineSegment StartX=245 StartY=0 StartZ=0 EndX=245 EndY=595 EndZ=0
  constraints (36):
    c: Coincident(g0,g1)
    c: Coincident(g1,g2)
    c: Coincident(g2,g3)
    c: Coincident(g3,g0)
    c: Horizontal(g0)
    c: Horizontal(g2)
    c: Vertical(g1)
    c: Vertical(g3)
    c: Coincident(g4,g5)
    c: Coincident(g5,g6)
    c: Coincident(g6,g7)
    c: Coincident(g7,g4)
    c: Horizontal(g4)
    c: Horizontal(g6)
    c: Vertical(g7)
    c: Coincident(g8,g9)
    c: Coincident(g9,g10)
    c: Coincident(g10,g11)
    c: Coincident(g11,g8)
    c: Horizontal(g8)
    c: Horizontal(g10)
    c: Vertical(g9)
    c: Vertical(g11)
    c: PointOnObject(g8,g6)
    c: PointOnObject(g9,g0)
    c: DistanceY(g5,g5) = 30
    c: DistanceY(g1,g1) = 20
    c: PointOnObject(g0,g-1)
    c: DistanceX(g-1,g2) = 170
    c: DistanceX(g-1,g1) = 400
    c: DistanceY(g1,g4) = 645
    c: Vertical(g5)
    c: DistanceX(g-2,g6) = 250
    c: DistanceX(g6,g6) = 95
    c: DistanceX(g-2,g8) = 245
    c: DistanceX(g8,g8) = 12
FEATURE [Part::Revolution] Revolve010
  Angle = 360
  Axis = (0,0,1)
  Base = (0,0,0)
  FaceMakerClass = Part::FaceMakerBullseye
  Solid = true
  Source = -> Sketch091
  Symmetric = false
FEATURE [Sketcher::SketchObject] Sketch092
  ArcFitTolerance = 0
  AttachmentSupport = -> [Revolve010]
  FullyConstrained = false
  MakeInternals = false
  MapMode = 5
  sketch-geometry (1):
    g0: Circle CenterX=360 CenterY=0 CenterZ=0 NormalX=0 NormalY=0 NormalZ=1 AngleXU=0 Radius=12.4969
  constraints (2):
    c: PointOnObject(g0,g-1)
    c: DistanceX(g-1,g0) = 360
FEATURE [Part::Extrusion] Extrude071  label="Extrude074"
  Base = -> Sketch092
  Dir = (0,0,1)
  DirMode = 2
  FaceMakerClass = Part::FaceMakerBullseye
  FaceMakerMode = 3
  LengthFwd = 30
  LengthRev = 0
  Reversed = true
  Solid = true
  Symmetric = false
FEATURE [Part::FeaturePython] Array025  label="Array004"  # Draft array (typed FeaturePython)
  AlwaysSyncPlacement = false
  Angle = 360
  ArrayType = 1
  Axis = (0,0,1)
  Base = -> Extrude071
  Center = (0,0,38)
  Count = 8
  ExpandArray = false
  Fuse = false
  IntervalAxis = (0,0,0)
  IntervalX = (50,0,0)
  IntervalY = (0,50,0)
  IntervalZ = (0,0,50)
  NumberCircles = 3
  NumberPolar = 8
  NumberX = 2
  NumberY = 2
  NumberZ = 1
  PlacementList = 8 placements: [(0,0,0),(0,0,0),(0,0,-7.10543e-15),(0,0,0),(0,0,0),(0,0,0),(0,0,0),(0,0,0)]
  RadialDistance = 50
  ScaleList = (8) [(1,1,1),(1,1,1),(1,1,1),(1,1,1),(1,1,1),(1,1,1),(1,1,1),(1,1,1)]
  Symmetry = 1
  TangentialDistance = 25
FEATURE [Sketcher::SketchObject] Sketch093
  ArcFitTolerance = 0
  ExternalGeometry = -> [Revolve010]
  FullyConstrained = true
  MakeInternals = false
  Placement = pos=(0,0,0) rot=(1,0,0;1.5708rad)
  sketch-geometry (4):
    g0: LineSegment StartX=257 StartY=595 StartZ=0 EndX=257 EndY=0 EndZ=0
    g1: LineSegment StartX=257 StartY=0 StartZ=0 EndX=400 EndY=0 EndZ=0
    g2: LineSegment StartX=400 StartY=0 StartZ=0 EndX=345 EndY=595 EndZ=0
    g3: LineSegment StartX=345 StartY=595 StartZ=0 EndX=257 EndY=595 EndZ=0
  constraints (8):
    c: Coincident(g0,g1)
    c: Coincident(g1,g2)
    c: Coincident(g2,g3)
    c: Coincident(g3,g0)
    c: Coincident(g0,g-4)
    c: Coincident(g0,g-4)
    c: Coincident(g2,g-3)
    c: Coincident(g1,g-5)
FEATURE [Part::Extrusion] Extrude072  label="Extrude075"
  Base = -> Sketch093
  Dir = (0,-1,2e-16)
  DirMode = 2
  FaceMakerClass = Part::FaceMakerBullseye
  FaceMakerMode = 3
  LengthFwd = 12
  LengthRev = 0
  Placement = pos=(0,0,0) rot=(0,0,1;0.392699rad)
  Solid = true
  Symmetric = true
FEATURE [Part::FeaturePython] Array026  # Draft array (typed FeaturePython)
  AlwaysSyncPlacement = false
  Angle = 360
  ArrayType = 1
  Axis = (0,0,1)
  Base = -> Extrude072
  Center = (0,0,58)
  Count = 8
  ExpandArray = false
  Fuse = false
  IntervalAxis = (0,0,0)
  IntervalX = (50,0,0)
  IntervalY = (0,50,0)
  IntervalZ = (0,0,50)
  NumberCircles = 3
  NumberPolar = 8
  NumberX = 2
  NumberY = 2
  NumberZ = 1
  PlacementList = 8 placements: [(0,0,0),(0,0,0),(0,0,-1.42109e-14),(0,0,0),(0,0,0),(0,0,0),(0,0,0),(0,0,0)]
  RadialDistance = 50
  ScaleList = (8) [(1,1,1),(1,1,1),(1,1,1),(1,1,1),(1,1,1),(1,1,1),(1,1,1),(1,1,1)]
  Symmetry = 1
  TangentialDistance = 25
FEATURE [App::Part] Part034  label="reducerBase"
  Group = -> [Revolve010,Sketch092,Extrude071,Sketch091,Array025,Sketch093,Extrude072,Array026]
  Origin = -> Origin047
FEATURE [App::Part] Part035  label="DriveSystem"
  Group = -> [Part034,Part__Feature024,Clone016,Part033,Part032,Part031,Body007,Body006,NSK_7926A5]
  Origin = -> Origin048
  Placement = pos=(0,0,5942) rot=(0,0,1;0rad)
  mass = 1145.89
FEATURE [Part::FeaturePython] Both_flanges_straight_pipe  # WARN: FeaturePython — macro-defined, semantics opaque (R4)
  L = 700
  Placement = pos=(-7300,-3.22e-13,3521) rot=(0,0,1;0rad)
  dia = 8
  fittings = 07_Both_flanges_straight_pipe
  material = 0
  standard = 0
  standard2 = 1
  expr: .Placement.Base.x = -<<Spreadsheet_Assy>>.dia / 2 - 550
FEATURE [Part::FeaturePython] Both_flanges_straight_pipe001  # WARN: FeaturePython — macro-defined, semantics opaque (R4)
  L = 5100
  Placement = pos=(-6600,-3.22e-13,3521) rot=(0,0,1;0rad)
  dia = 8
  fittings = 07_Both_flanges_straight_pipe
  material = 0
  standard = 0
  standard2 = 1
  expr: .Placement.Base.x = -<<Spreadsheet_Assy>>.dia / 2 + 150
  expr: L = <<Spreadsheet_Assy>>.dia * 0.4 - 300
FEATURE [Sketcher::SketchObject] Sketch002
  ArcFitTolerance = 0
  AttachmentSupport = -> [XZ_Plane053]
  FullyConstrained = true
  MakeInternals = false
  MapMode = 5
  Placement = pos=(0,0,0) rot=(1,0,0;1.5708rad)
  sketch-geometry (8):
    g0: LineSegment StartX=40 StartY=0 StartZ=0 EndX=62.5 EndY=0 EndZ=0
    g1: LineSegment StartX=62.5 StartY=0 StartZ=0 EndX=62.5 EndY=90 EndZ=0
    g2: LineSegment StartX=62.5 StartY=90 StartZ=0 EndX=108 EndY=90 EndZ=0
    g3: LineSegment StartX=108 StartY=90 StartZ=0 EndX=108 EndY=110 EndZ=0
    g4: LineSegment StartX=108 StartY=110 StartZ=0 EndX=0 EndY=110 EndZ=0
    g5: LineSegment StartX=0 StartY=110 StartZ=0 EndX=0 EndY=65 EndZ=0
    g6: LineSegment StartX=40 StartY=0 StartZ=0 EndX=40 EndY=65 EndZ=0
    g7: LineSegment StartX=40 StartY=65 StartZ=0 EndX=0 EndY=65 EndZ=0
  constraints (24):
    c: PointOnObject(g0,g-1)
    c: Coincident(g0,g1)
    c: Vertical(g1)
    c: Coincident(g1,g2)
    c: Horizontal(g2)
    c: Coincident(g2,g3)
    c: Vertical(g3)
    c: Coincident(g3,g4)
    c: Horizontal(g4)
    c: Coincident(g4,g5)
    c: Vertical(g5)
    c: Vertical(g6)
    c: Coincident(g6,g7)
    c: Horizontal(g7)
    c: Coincident(g0,g6)
    c: Coincident(g5,g7)
    c: DistanceX(g-1,g0) = 40
    c: DistanceX(g-1,g0) = 62.5
    c: DistanceY(g6,g6) = 65
    c: Horizontal(g0)
    c: DistanceY(g1,g1) = 90
    c: DistanceY(g3,g3) = 20
    c: DistanceX(g4,g4) = 108
    c: PointOnObject(g4,g-2)
FEATURE [PartDesign::Revolution] Revolution001
  Angle = 360
  Angle2 = 60
  Axis = (0,2e-16,1)
  Base = (0,0,0)
  Placement = pos=(0,0,0) rot=(1,0,0;1.5708rad)
  Profile = -> Sketch002
  ReferenceAxis = -> Sketch002 [V_Axis]
  Reversed = true
  Suppressed = false
  Type = 0
FEATURE [PartDesign::Chamfer] Chamfer001
  Angle = 45
  Base = -> Revolution001 [Edge6]
  BaseFeature = -> Revolution001
  ChamferType = 0
  FlipDirection = false
  Placement = pos=(0,0,0) rot=(1,0,0;1.5708rad)
  Size = 5
  Size2 = 1
  SupportTransform = false
  Suppressed = false
  UseAllEdges = false
FEATURE [Spreadsheet::Sheet] Spreadsheet
  cells = A2='full Length   L0; B2(L0)=5600; A3='pipe Length   l1; B3(l1)==L0 - (110 + 310); A4='rake Position lk; B4(lk)=1015; A5='rake Braket Width; B5(rbw)=615; A6='skimmer Position  ls; B6(ls)=5203; A7='skimmer Bracket Width; B7(sbw)=750; A8='rake turnbackle spacing; B8(rts)=1200
FEATURE [Sketcher::SketchObject] Sketch003
  ArcFitTolerance = 0
  AttachmentSupport = -> [XZ_Plane054]
  FullyConstrained = true
  MakeInternals = false
  MapMode = 5
  Placement = pos=(0,0,0) rot=(1,0,0;1.5708rad)
  expr: Constraints[17] = Spreadsheet.l1 + 170
  sketch-geometry (6):
    g0: LineSegment StartX=0 StartY=5350 StartZ=0 EndX=108 EndY=5350 EndZ=0
    g1: LineSegment StartX=108 StartY=5350 StartZ=0 EndX=108 EndY=5380 EndZ=0
    g2: LineSegment StartX=108 StartY=5380 StartZ=0 EndX=65 EndY=5380 EndZ=0
    g3: LineSegment StartX=65 StartY=5380 StartZ=0 EndX=65 EndY=5660 EndZ=0
    g4: LineSegment StartX=65 StartY=5660 StartZ=0 EndX=0 EndY=5660 EndZ=0
    g5: LineSegment StartX=0 StartY=5660 StartZ=0 EndX=0 EndY=5350 EndZ=0
  constraints (18):
    c: Horizontal(g0)
    c: Coincident(g0,g1)
    c: Coincident(g1,g2)
    c: Coincident(g2,g3)
    c: Vertical(g3)
    c: Coincident(g3,g4)
    c: Horizontal(g4)
    c: Coincident(g4,g5)
    c: Coincident(g5,g0)
    c: Vertical(g5)
    c: PointOnObject(g4,g-2)
    c: DistanceX(g4,g4) = 65
    c: Horizontal(g2)
    c: Vertical(g1)
    c: DistanceY(g1,g1) = 30
    c: DistanceX(g0,g0) = 108
    c: DistanceY(g3,g3) = 280
    c: DistanceY(g-1,g0) = 5350
FEATURE [PartDesign::Revolution] Revolution002
  Angle = 360
  Angle2 = 60
  Axis = (0,2e-16,1)
  Base = (0,0,0)
  Placement = pos=(0,0,0) rot=(1,0,0;1.5708rad)
  Profile = -> Sketch003
  ReferenceAxis = -> Sketch003 [V_Axis]
  Reversed = true
  Suppressed = false
  Type = 0
FEATURE [PartDesign::Body] Body002  label="top"
  AllowCompound = false
  Group = -> [Sketch003,Revolution002]
  Origin = -> Origin054
  Tip = -> Revolution002
FEATURE [Sketcher::SketchObject] Sketch004
  ArcFitTolerance = 0
  FullyConstrained = true
  MakeInternals = false
  Placement = pos=(0,0,0) rot=(0.57735,0.57735,0.57735;2.0944rad)
  sketch-geometry (2):
    g0: Circle CenterX=0 CenterY=0 CenterZ=0 NormalX=0 NormalY=0 NormalZ=1 AngleXU=0 Radius=50
    g1: Circle CenterX=0 CenterY=0 CenterZ=0 NormalX=0 NormalY=0 NormalZ=1 AngleXU=0 Radius=57
  constraints (4):
    c: Coincident(g0,g-1)
    c: Coincident(g1,g0)
    c: Diameter(g1) = 114
    c: Diameter(g0) = 100
FEATURE [Part::Extrusion] Extrude073  label="Extrude076"
  Base = -> Sketch004
  Dir = (1,0,0)
  DirMode = 2
  FaceMakerClass = Part::FaceMakerBullseye
  FaceMakerMode = 3
  LengthFwd = 649
  LengthRev = 0
  Solid = true
  Symmetric = true
  expr: LengthFwd = Spreadsheet.rbw + 34
FEATURE [Sketcher::SketchObject] Sketch005
  ArcFitTolerance = 0
  AttachmentSupport = -> [Extrude073]
  FullyConstrained = true
  MakeInternals = false
  MapMode = 5
  Placement = pos=(324.5,0,0) rot=(0.57735,0.57735,0.57735;2.0944rad)
  sketch-geometry (10):
    g0: LineSegment StartX=32.5 StartY=56.2917 StartZ=0 EndX=100 EndY=17.3205 EndZ=0
    g1: ArcOfCircle CenterX=90 CenterY=0 CenterZ=0 NormalX=0 NormalY=0 NormalZ=1 AngleXU=0 Radius=20 StartAngle=5.23599 EndAngle=7.33038
    g2: LineSegment StartX=100 StartY=-17.3205 StartZ=0 EndX=32.5 EndY=-56.2917 EndZ=0
    g3: ArcOfCircle CenterX=0 CenterY=0 CenterZ=0 NormalX=0 NormalY=0 NormalZ=1 AngleXU=0 Radius=65 StartAngle=4.18879 EndAngle=5.23599
    g4: LineSegment StartX=-32.5 StartY=-56.2917 StartZ=0 EndX=-100 EndY=-17.3205 EndZ=0
    g5: ArcOfCircle CenterX=-90 CenterY=0 CenterZ=0 NormalX=0 NormalY=0 NormalZ=1 AngleXU=0 Radius=20 StartAngle=2.0944 EndAngle=4.18879
    g6: LineSegment StartX=-100 StartY=17.3205 StartZ=0 EndX=-32.5 EndY=56.2917 EndZ=0
    g7: ArcOfCircle CenterX=0 CenterY=0 CenterZ=0 NormalX=0 NormalY=0 NormalZ=1 AngleXU=0 Radius=65 StartAngle=1.0472 EndAngle=2.0944
    g8: Circle CenterX=90 CenterY=0 CenterZ=0 NormalX=0 NormalY=0 NormalZ=1 AngleXU=0 Radius=10
    g9: Circle CenterX=-90 CenterY=0 CenterZ=0 NormalX=0 NormalY=0 NormalZ=1 AngleXU=0 Radius=10
  constraints (24):
    c: Tangent(g0,g1) = 1.5708
    c: Coincident(g1,g2)
    c: Tangent(g2,g3) = 1.5708
    c: Coincident(g3,g4)
    c: Tangent(g4,g5) = 1.5708
    c: Tangent(g6,g7) = 1.5708
    c: Coincident(g7,g0)
    c: Coincident(g8,g1)
    c: Coincident(g9,g5)
    c: Coincident(g-1,g3)
    c: Coincident(g-1,g7)
    c: Diameter(g8) = 20
    c: Equal(g8,g9)
    c: Radius(g1) = 20
    c: Equal(g1,g5)
    c: Symmetric(g5,g1,g3)
    c: PointOnObject(g5,g-1)
    c: Tangent(g5,g6) = 1.5708
    c: Equal(g0,g2)
    c: Equal(g2,g4)
    c: Equal(g4,g6)
    c: DistanceX(g3,g1) = 90
    c: Radius(g3) = 65
    c: Equal(g3,g7)
FEATURE [Part::Extrusion] Extrude001
  Base = -> Sketch005
  Dir = (1,0,0)
  DirMode = 2
  FaceMakerClass = Part::FaceMakerBullseye
  FaceMakerMode = 3
  LengthFwd = 9
  LengthRev = 0
  Solid = true
  Symmetric = false
FEATURE [Part::FeaturePython] Clone  label="Extrude002"  # Draft clone (typed FeaturePython)
  AttacherType = Attacher::AttachEngine3D
  Fuse = false
  Objects = -> [Extrude001]
  Placement = pos=(-25,0,0) rot=(0,0,1;0rad)
  Scale = (1,1,1)
FEATURE [Part::Compound] Compound
  Links = -> [Extrude001,Clone]
FEATURE [Part::Mirroring] Part__Mirroring  label="Compound (Mirror #1)"
  Base = (0,0,0)
  Normal = (1,0,0)
  Source = -> Compound
FEATURE [Part::Compound] Compound001  label="arm_rake"
  Links = -> [Extrude073,Part__Mirroring,Compound]
  Placement = pos=(0,0,1015) rot=(0,0,1;0rad)
  expr: .Placement.Base.z = Spreadsheet.lk
FEATURE [Sketcher::SketchObject] Sketch006
  ArcFitTolerance = 0
  FullyConstrained = true
  MakeInternals = false
  Placement = pos=(0,0,0) rot=(0.57735,0.57735,0.57735;2.0944rad)
  sketch-geometry (2):
    g0: Circle CenterX=0 CenterY=0 CenterZ=0 NormalX=0 NormalY=0 NormalZ=1 AngleXU=0 Radius=50
    g1: Circle CenterX=0 CenterY=0 CenterZ=0 NormalX=0 NormalY=0 NormalZ=1 AngleXU=0 Radius=57
  constraints (4):
    c: Coincident(g0,g-1)
    c: Coincident(g1,g0)
    c: Diameter(g0) = 100
    c: Diameter(g1) = 114
FEATURE [Part::Extrusion] Extrude002  label="Extrude003"
  Base = -> Sketch006
  Dir = (1,0,0)
  DirMode = 2
  FaceMakerClass = Part::FaceMakerBullseye
  FaceMakerMode = 3
  LengthFwd = 750
  LengthRev = 0
  Solid = true
  Symmetric = true
  expr: LengthFwd = Spreadsheet.sbw
FEATURE [Sketcher::SketchObject] Sketch007
  ArcFitTolerance = 0
  FullyConstrained = false
  MakeInternals = false
  Placement = pos=(0,0,0) rot=(0.57735,0.57735,0.57735;2.0944rad)
  sketch-geometry (5):
    g0: LineSegment StartX=-47.753 StartY=31.1231 StartZ=0 EndX=-152.141 EndY=19.8851 EndZ=0
    g1: ArcOfCircle CenterX=-150 CenterY=0 CenterZ=0 NormalX=0 NormalY=0 NormalZ=1 AngleXU=0 Radius=20 StartAngle=1.67804 EndAngle=4.60515
    g2: LineSegment StartX=-152.141 StartY=-19.8851 StartZ=0 EndX=-47.753 EndY=-31.1231 EndZ=0
    g3: ArcOfCircle CenterX=0 CenterY=0 CenterZ=0 NormalX=0 NormalY=0 NormalZ=1 AngleXU=0 Radius=57 StartAngle=2.56399 EndAngle=3.7192
    g4: Circle CenterX=-150 CenterY=0 CenterZ=0 NormalX=0 NormalY=0 NormalZ=1 AngleXU=0 Radius=10
  constraints (12):
    c: Tangent(g0,g1) = -1.5708
    c: Coincident(g3,g2)
    c: Coincident(g3,g0)
    c: Coincident(g3,g-3)
    c: Radius(g3) = 57
    c: Horizontal(g1,g3)
    c: Vertical(g2,g0)
    c: Coincident(g4,g1)
    c: Radius(g4) = 10
    c: Radius(g1) = 20
    c: Tangent(g1,g2) = -1.5708
    c: DistanceX(g1,g3) = 150
FEATURE [Part::Extrusion] Extrude003  label="Extrude004"
  Base = -> Sketch007
  Dir = (1,0,0)
  DirMode = 2
  FaceMakerClass = Part::FaceMakerBullseye
  FaceMakerMode = 3
  LengthFwd = 6
  LengthRev = 0
  Solid = true
  Symmetric = true
FEATURE [Sketcher::SketchObject] Sketch009
  ArcFitTolerance = 0
  FullyConstrained = true
  MakeInternals = false
  sketch-geometry (5):
    g0: LineSegment StartX=350 StartY=-57 StartZ=0 EndX=270 EndY=-57 EndZ=0
    g1: LineSegment StartX=270 StartY=-57 StartZ=0 EndX=291.771 EndY=-105.229 EndZ=0
    g2: ArcOfCircle CenterX=310 CenterY=-97 CenterZ=0 NormalX=0 NormalY=0 NormalZ=1 AngleXU=0 Radius=20 StartAngle=3.56562 EndAngle=5.85915
    g3: LineSegment StartX=328.229 StartY=-105.229 StartZ=0 EndX=350 EndY=-57 EndZ=0
    g4: Circle CenterX=310 CenterY=-97 CenterZ=0 NormalX=0 NormalY=0 NormalZ=1 AngleXU=0 Radius=10
  constraints (13):
    c: Horizontal(g0)
    c: Coincident(g0,g1)
    c: Tangent(g1,g2) = -1.5708
    c: Coincident(g3,g0)
    c: Coincident(g4,g2)
    c: Diameter(g4) = 20
    c: Radius(g2) = 20
    c: DistanceX(g0,g0) = 80
    c: Distance(g2,g0) = 40
    c: Tangent(g2,g3) = -1.5708
    c: Equal(g1,g3)
    c: DistanceY(g0,g-1) = 57
    c: DistanceX(g-1,g0) = 350
FEATURE [Part::Extrusion] Extrude005  label="Extrude006"
  Base = -> Sketch009
  Dir = (0,0,1)
  DirMode = 2
  FaceMakerClass = Part::FaceMakerBullseye
  FaceMakerMode = 3
  LengthFwd = 6
  LengthRev = 0
  Solid = true
  Symmetric = true
FEATURE [Part::Mirroring] Mirror001  label="Extrude006 (mirrored)"
  Base = (0,-500,0)
  Normal = (1,0,0)
  Source = -> Extrude005
FEATURE [Sketcher::SketchObject] Sketch098
  ArcFitTolerance = 1e-06
  AttachmentSupport = -> [Chamfer001]
  FullyConstrained = true
  MakeInternals = false
  MapMode = 5
  Placement = pos=(0,4.84e-14,110) rot=(0,0,1;3.14159rad)
  sketch-geometry (1):
    g0: Circle CenterX=0 CenterY=0 CenterZ=0 NormalX=0 NormalY=0 NormalZ=1 AngleXU=0 Radius=108
  constraints (2):
    c: Coincident(g0,g-1)
    c: Diameter(g0) = 216
FEATURE [PartDesign::Pad] Pad
  BaseFeature = -> Chamfer001
  Direction = (0,0,1)
  Length = 5180
  Length2 = 10
  Placement = pos=(0,0,0) rot=(1,0,0;1.5708rad)
  Profile = -> Sketch098
  ReferenceAxis = -> Sketch098 [N_Axis]
  Suppressed = false
  Type = 0
  expr: Length = Spreadsheet.l1
FEATURE [Sketcher::SketchObject] Sketch010
  ArcFitTolerance = 1e-06
  AttachmentSupport = -> [Pad]
  FullyConstrained = true
  MakeInternals = false
  MapMode = 5
  Placement = pos=(0,0,5290) rot=(0,0,1;3.14159rad)
  sketch-geometry (1):
    g0: Circle CenterX=0 CenterY=0 CenterZ=0 NormalX=0 NormalY=0 NormalZ=1 AngleXU=0 Radius=100
  constraints (2):
    c: Coincident(g0,g-1)
    c: Diameter(g0) = 200
FEATURE [PartDesign::Pocket] Pocket
  BaseFeature = -> Pad
  Direction = (0,0,-1)
  Length = 5180
  Length2 = 5
  Placement = pos=(0,0,0) rot=(1,0,0;1.5708rad)
  Profile = -> Sketch010
  ReferenceAxis = -> Sketch010 [N_Axis]
  Suppressed = false
  Type = 0
  expr: Length = Spreadsheet.l1
FEATURE [PartDesign::Body] Body001  label="pipe002"
  AllowCompound = false
  Group = -> [Sketch002,Revolution001,Chamfer001,Sketch098,Pad,Sketch010,Pocket]
  Origin = -> Origin053
  Placement = pos=(0,0,60) rot=(0,0,1;0rad)
  Tip = -> Pocket
FEATURE [PartDesign::ShapeBinder] CopyExtrude002
  TraceSupport = false
FEATURE [Sketcher::SketchObject] Sketch011
  ArcFitTolerance = 1e-06
  AttachmentSupport = -> [CopyExtrude002]
  FullyConstrained = true
  MakeInternals = false
  MapMode = 5
  Placement = pos=(-375,0,0) rot=(0.57735,-0.57735,-0.57735;2.0944rad)
  sketch-geometry (1):
    g0: Circle CenterX=0 CenterY=0 CenterZ=0 NormalX=0 NormalY=0 NormalZ=1 AngleXU=0 Radius=57
  constraints (2):
    c: Coincident(g0,g-1)
    c: Diameter(g0) = 114
FEATURE [PartDesign::Pad] Pad001
  Direction = (-1,0,0)
  Length = 6
  Length2 = 10
  Profile = -> Sketch011
  ReferenceAxis = -> Sketch011 [N_Axis]
  Suppressed = false
  Type = 0
FEATURE [PartDesign::ShapeBinder] CopyExtrude003
  TraceSupport = false
FEATURE [PartDesign::ShapeBinder] ReferenceExtrude002
  Support = -> [Extrude002]
  TraceSupport = false
FEATURE [PartDesign::Body] Body009  label="Body"
  AllowCompound = false
  Group = -> [CopyExtrude002,Sketch011,Pad001,CopyExtrude003,ReferenceExtrude002]
  Origin = -> Origin055
  Tip = -> Pad001
FEATURE [Part::Mirroring] Mirror  label="Pad001 (mirrored)"
  Base = (0,4.44e-14,-200)
  Normal = (-1,0,0)
  Source = -> Pad001
FEATURE [Part::Compound] Compound002  label="arm_skimmer"
  Links = -> [Mirror001,Extrude005,Extrude003,Extrude002,Body009,Mirror]
  Placement = pos=(0,0,5203) rot=(0,0,1;0rad)
  expr: .Placement.Base.z = Spreadsheet.ls
FEATURE [Sketcher::SketchObject] Sketch013
  ArcFitTolerance = 1e-06
  FullyConstrained = true
  MakeInternals = false
  Placement = pos=(0,0,0) rot=(0.57735,0.57735,0.57735;2.0944rad)
  sketch-geometry (3):
    g0: LineSegment StartX=0 StartY=770 StartZ=0 EndX=760 EndY=770 EndZ=0
    g1: LineSegment StartX=760 StartY=770 StartZ=0 EndX=470 EndY=0 EndZ=0
    g2: LineSegment StartX=470 StartY=0 StartZ=0 EndX=190 EndY=0 EndZ=0
  constraints (10):
    c: Horizontal(g0)
    c: Coincident(g0,g1)
    c: PointOnObject(g1,g-1)
    c: Coincident(g1,g2)
    c: PointOnObject(g2,g-1)
    c: PointOnObject(g0,g-2)
    c: DistanceX(g0,g0) = 760
    c: DistanceY(g-1,g0) = 770
    c: DistanceX(g2,g1) = 280
    c: Distance(g1,g-2) = 470
FEATURE [Part::FeaturePython] AngleSteel  # WARN: FeaturePython — macro-defined, semantics opaque (R4)
  A = 75
  B = 75
  L = 5500
  Placement = pos=(0,0,770) rot=(0,1,0;3.14159rad)
  Solid = false
  g0 = 7.85
  mass = 0
  size = 10
  standard = SS_Equal
  t = 6
  type = 00_Angle
FEATURE [Part::Sweep] Sweep
  Frenet = true
  Sections = -> [AngleSteel]
  Solid = true
  Spine = -> Sketch013 [Edge1,Edge2,Edge3]
  Transition = 1
FEATURE [App::Part] Part040  label="shaft"
  Group = -> [Sketch013,AngleSteel,Sweep]
  Origin = -> Origin004
  Placement = pos=(0,0,60) rot=(0,0,1;0rad)
FEATURE [Sketcher::SketchObject] Sketch099
  ArcFitTolerance = 0
  FullyConstrained = true
  MakeInternals = false
  Placement = pos=(0,0,0) rot=(0.57735,0.57735,0.57735;2.0944rad)
  sketch-geometry (2):
    g0: Circle CenterX=0 CenterY=0 CenterZ=0 NormalX=0 NormalY=0 NormalZ=1 AngleXU=0 Radius=50
    g1: Circle CenterX=0 CenterY=0 CenterZ=0 NormalX=0 NormalY=0 NormalZ=1 AngleXU=0 Radius=57
  constraints (4):
    c: Coincident(g0,g-1)
    c: Coincident(g1,g0)
    c: Diameter(g1) = 114
    c: Diameter(g0) = 100
FEATURE [Part::Extrusion] Extrude074  label="Extrude077"
  Base = -> Sketch099
  Dir = (1,0,0)
  DirMode = 2
  FaceMakerClass = Part::FaceMakerBullseye
  FaceMakerMode = 3
  LengthFwd = 649
  LengthRev = 0
  Solid = true
  Symmetric = true
  expr: LengthFwd = Spreadsheet.rbw + 34
FEATURE [Sketcher::SketchObject] Sketch100
  ArcFitTolerance = 0
  AttachmentSupport = -> [Extrude074]
  FullyConstrained = true
  MakeInternals = false
  MapMode = 5
  Placement = pos=(324.5,0,0) rot=(0.57735,0.57735,0.57735;2.0944rad)
  sketch-geometry (10):
    g0: LineSegment StartX=32.5 StartY=56.2917 StartZ=0 EndX=100 EndY=17.3205 EndZ=0
    g1: ArcOfCircle CenterX=90 CenterY=0 CenterZ=0 NormalX=0 NormalY=0 NormalZ=1 AngleXU=0 Radius=20 StartAngle=5.23599 EndAngle=7.33038
    g2: LineSegment StartX=100 StartY=-17.3205 StartZ=0 EndX=32.5 EndY=-56.2917 EndZ=0
    g3: ArcOfCircle CenterX=0 CenterY=0 CenterZ=0 NormalX=0 NormalY=0 NormalZ=1 AngleXU=0 Radius=65 StartAngle=4.18879 EndAngle=5.23599
    g4: LineSegment StartX=-32.5 StartY=-56.2917 StartZ=0 EndX=-100 EndY=-17.3205 EndZ=0
    g5: ArcOfCircle CenterX=-90 CenterY=0 CenterZ=0 NormalX=0 NormalY=0 NormalZ=1 AngleXU=0 Radius=20 StartAngle=2.0944 EndAngle=4.18879
    g6: LineSegment StartX=-100 StartY=17.3205 StartZ=0 EndX=-32.5 EndY=56.2917 EndZ=0
    g7: ArcOfCircle CenterX=0 CenterY=0 CenterZ=0 NormalX=0 NormalY=0 NormalZ=1 AngleXU=0 Radius=65 StartAngle=1.0472 EndAngle=2.0944
    g8: Circle CenterX=90 CenterY=0 CenterZ=0 NormalX=0 NormalY=0 NormalZ=1 AngleXU=0 Radius=10
    g9: Circle CenterX=-90 CenterY=0 CenterZ=0 NormalX=0 NormalY=0 NormalZ=1 AngleXU=0 Radius=10
  constraints (24):
    c: Tangent(g0,g1) = 1.5708
    c: Coincident(g1,g2)
    c: Tangent(g2,g3) = 1.5708
    c: Coincident(g3,g4)
    c: Tangent(g4,g5) = 1.5708
    c: Tangent(g6,g7) = 1.5708
    c: Coincident(g7,g0)
    c: Coincident(g8,g1)
    c: Coincident(g9,g5)
    c: Coincident(g-1,g3)
    c: Coincident(g-1,g7)
    c: Diameter(g8) = 20
    c: Equal(g8,g9)
    c: Radius(g1) = 20
    c: Equal(g1,g5)
    c: Symmetric(g5,g1,g3)
    c: PointOnObject(g5,g-1)
    c: Tangent(g5,g6) = 1.5708
    c: Equal(g0,g2)
    c: Equal(g2,g4)
    c: Equal(g4,g6)
    c: DistanceX(g3,g1) = 90
    c: Radius(g3) = 65
    c: Equal(g3,g7)
FEATURE [Part::Extrusion] Extrude075  label="Extrude078"
  Base = -> Sketch100
  Dir = (1,0,0)
  DirMode = 2
  FaceMakerClass = Part::FaceMakerBullseye
  FaceMakerMode = 3
  LengthFwd = 9
  LengthRev = 0
  Placement = pos=(-12.5,0,0) rot=(0,0,1;0rad)
  Solid = true
  Symmetric = false
FEATURE [Part::FeaturePython] Clone017  label="Extrude079"  # Draft clone (typed FeaturePython)
  AttacherType = Attacher::AttachEngine3D
  Fuse = false
  Objects = -> [Extrude075]
  Placement = pos=(-646,0,0) rot=(0,0,1;0rad)
  Scale = (1,1,1)
  expr: .Placement.Base.x = -Spreadsheet.rbw - 34 + 3
FEATURE [Part::Compound] Compound020  label="turnBackle"
  Links = -> [Clone017,Extrude074,Extrude075]
  Placement = pos=(0,0,2515) rot=(0,0,1;0rad)
  expr: .Placement.Base.z = Spreadsheet.lk + 1500
FEATURE [App::Part] Part041  label="mainShaft"
  Group = -> [Part040,Spreadsheet,Sketch004,Clone,Extrude001,Sketch005,Extrude073,Compound,Part__Mirroring,Compound001,Sketch006,Extrude002,Sketch007,Extrude003,Body002,Body001,Sketch009,Extrude005,Mirror001,Compound002,Extrude075,Extrude074,Sketch099,Sketch100,Clone017,Compound020]
  Origin = -> Origin006
  Placement = pos=(0,0,0) rot=(0,0,1;4.71239rad)
  mass = 321.204
FEATURE [Sketcher::SketchObject] Sketch101
  ArcFitTolerance = 0
  FullyConstrained = true
  MakeInternals = false
  MapMode = 5
  Placement = pos=(0,0,0) rot=(1,0,0;1.5708rad)
  expr: Constraints[10] = Spreadsheet012.L7 * 2
  expr: Constraints[9] = Spreadsheet012.B7
  sketch-geometry (4):
    g0: LineSegment StartX=90 StartY=23 StartZ=0 EndX=-8.967e-12 EndY=23 EndZ=0
    g1: ArcOfCircle CenterX=0 CenterY=0 CenterZ=0 NormalX=0 NormalY=0 NormalZ=1 AngleXU=0 Radius=23 StartAngle=1.5708 EndAngle=4.71239
    g2: LineSegment StartX=-9.439e-13 StartY=-23 StartZ=0 EndX=90 EndY=-23 EndZ=0
    g3: LineSegment StartX=90 StartY=-23 StartZ=0 EndX=90 EndY=23 EndZ=0
  constraints (11):
    c: Horizontal(g0)
    c: Tangent(g0,g1) = -1.5708
    c: PointOnObject(g1,g-2)
    c: Coincident(g1,g2)
    c: Horizontal(g2)
    c: Coincident(g2,g3)
    c: Coincident(g3,g0)
    c: Vertical(g3)
    c: Coincident(g-1,g1)
    c: DistanceX(g0,g0) = 90
    c: Distance(g3) = 46
FEATURE [PartDesign::Pad] Pad002
  Direction = (0,-1,0)
  Length = 40
  Length2 = 10
  Midplane = true
  Placement = pos=(0,0,0) rot=(1,0,0;1.5708rad)
  Profile = -> Sketch101
  ReferenceAxis = -> Sketch101 [N_Axis]
  Suppressed = false
  Type = 0
  expr: Length = Spreadsheet012.D7
FEATURE [Spreadsheet::Sheet] Spreadsheet012
  cells = A2='rodDia dia; B2(dia)=20; A3='length L0; B3(L0)=1255; B4='l; C4='l1; D4='a; E4='b; F4='c; G4='e; H4='f; I4='g; J4='h; K4='i; L4='r; A5='forkEndR; B5=120; D5=40; E5=16; F5=21; G5=24; H5=20; I5=60; J5=10; K5=20; L5=23; A6='turnBackle; B6=150; C6=28; D6=42; E6=23; F6=33; A7='forkEndL; B7=90; D7=40; E7=16; F7=20; G7=24; H7=20; I7=30; L7=23; A8=1; B8=2; C8=3; D8=4; E8=5; F8=6; G8=7; H8=8; I8=9; J8=10; K8=11; L8=12; A9='turnBackle; A10='d; B10='l; C10='l1; D10='a; E10='b; F10='c; A11=10; B11=75; C11=15; D11=24; E11=13; F11=17; A12=12; B12=100; C12=20; D12=30; E12=16; F12=22; A13=16; B13=125; C13=24; D13=36; E13=20; F13=27; A14=20; B14=150; C14=28; D14=42; E14=23; F14=33; A15=22; B15=175; C15=33; D15=48; E15=27; F15=37; A16=24; B16=200; C16=38; D16=54; E16=30; F16=42; A17=30; B17=250; C17=47; D17=66; E17=37; F17=52; A18='forkEnd_L; A19='d; B19='l; C19='a; D19='b; E19='c; F19='e; G19='f; H19='g; I19='r; A20=10; B20=50; C20=20; D20=7; E20=10; F20=12; G20=10; H20=15; I20=12; A21=12; B21=60; C21=25; D21=10; E21=13; F21=16; G21=13; H21=20; I21=15; A22=16; B22=75; C22=30; D22=13; E22=16; F22=20; G22=16; H22=25; I22=19; A23=20; B23=90; C23=40; D23=16; E23=20; F23=24; G23=20; H23=30; I23=23; A24=22; B24=100; C24=45; D24=20; E24=23; F24=28; G24=23; H24=35; I24=27; A25=24; B25=115; C25=50; D25=23; E25=26; F25=32; G25=26; H25=40; I25=30; A26=30; B26=140; C26=65; D26=30; E26=33; F26=40; G26=33; H26=50; I26=38; A27='forkEnd_R; A28='d; B28='l; C28='a; D28='b; E28='c; F28='r; G28='e; H28='f; I28='g; J28='h; K28='i; A29=10; B29=60; C29=20; D29=7; E29=11; F29=12; G29=12; H29=10; I29=30; J29=5; K29=10; A30=12; B30=80; +64 more cells
FEATURE [Sketcher::SketchObject] Sketch102
  ArcFitTolerance = 0
  AttachmentSupport = -> [Pad002]
  FullyConstrained = true
  MakeInternals = false
  MapMode = 5
  Placement = pos=(0,-20,0) rot=(1,0,0;1.5708rad)
  expr: Constraints[1] = Spreadsheet012.F7 / 2
  sketch-geometry (1):
    g0: Circle CenterX=0 CenterY=0 CenterZ=0 NormalX=0 NormalY=0 NormalZ=1 AngleXU=0 Radius=10
  constraints (2):
    c: Coincident(g0,g-1)
    c: Radius(g0) = 10
FEATURE [Part::Extrusion] Extrude076  label="Extrude080"
  Base = -> Sketch102
  Dir = (0,-1,2e-16)
  DirMode = 2
  FaceMakerClass = Part::FaceMakerBullseye
  FaceMakerMode = 3
  LengthFwd = 65
  LengthRev = 0
  Reversed = true
  Solid = true
  Symmetric = false
FEATURE [Sketcher::SketchObject] Sketch103
  ArcFitTolerance = 0
  FullyConstrained = true
  MakeInternals = false
  Placement = pos=(0,0,0) rot=(1,0,0;1.5708rad)
  expr: Constraints[11] = Spreadsheet012.I5
  expr: Constraints[1] = Spreadsheet012.F5 / 2
  expr: Constraints[3] = Spreadsheet012.L5
  sketch-geometry (5):
    g0: Circle CenterX=0 CenterY=0 CenterZ=0 NormalX=0 NormalY=0 NormalZ=1 AngleXU=0 Radius=10.5
    g1: ArcOfCircle CenterX=0 CenterY=0 CenterZ=0 NormalX=0 NormalY=0 NormalZ=1 AngleXU=0 Radius=23 StartAngle=4.71239 EndAngle=7.85398
    g2: LineSegment StartX=-1.34e-14 StartY=23 StartZ=0 EndX=-60 EndY=23 EndZ=0
    g3: LineSegment StartX=-60 StartY=23 StartZ=0 EndX=-60 EndY=-23 EndZ=0
    g4: LineSegment StartX=-60 StartY=-23 StartZ=0 EndX=-7.1e-15 EndY=-23 EndZ=0
  constraints (12):
    c: Coincident(g0,g-1)
    c: Radius(g0) = 10.5
    c: Coincident(g1,g0)
    c: Radius(g1) = 23
    c: Horizontal(g2)
    c: Coincident(g2,g3)
    c: Vertical(g3)
    c: Coincident(g3,g4)
    c: Horizontal(g4)
    c: Tangent(g1,g2) = -1.5708
    c: Tangent(g1,g4) = -1.5708
    c: Distance(g2) = 60
FEATURE [Part::Extrusion] Extrude077  label="Extrude081"
  Base = -> Sketch103
  Dir = (0,-1,2e-16)
  DirMode = 2
  FaceMakerClass = Part::FaceMakerBullseye
  FaceMakerMode = 3
  LengthFwd = 40
  LengthRev = 0
  Solid = true
  Symmetric = true
  expr: LengthFwd = Spreadsheet012.D5
FEATURE [Sketcher::SketchObject] Sketch104
  ArcFitTolerance = 0
  AttachmentSupport = -> [Extrude077]
  ExternalGeometry = -> [Extrude077]
  FullyConstrained = true
  MakeInternals = false
  MapMode = 5
  Placement = pos=(0,5.1e-15,23) rot=(0,0,1;0rad)
  expr: Constraints[10] = Spreadsheet012.E5
  expr: Constraints[24] = Spreadsheet012.G5
  expr: Constraints[25] = Spreadsheet012.K5
  expr: Constraints[26] = Spreadsheet012.H5
  expr: Constraints[31] = Spreadsheet012.E5 / 2
  expr: Constraints[32] = Spreadsheet012.G5 / 2
  expr: Constraints[9] = Spreadsheet012.L5
  sketch-geometry (12):
    g0: LineSegment StartX=23 StartY=8 StartZ=0 EndX=-20 EndY=8 EndZ=0
    g1: LineSegment StartX=-21 StartY=12 StartZ=0 EndX=-39 EndY=12 EndZ=0
    g2: LineSegment StartX=-40 StartY=11 StartZ=0 EndX=-40 EndY=-11 EndZ=0
    g3: LineSegment StartX=-39 StartY=-12 StartZ=0 EndX=-21 EndY=-12 EndZ=0
    g4: LineSegment StartX=-20 StartY=-11 StartZ=0 EndX=-20 EndY=-8 EndZ=0
    g5: LineSegment StartX=-20 StartY=-8 StartZ=0 EndX=23 EndY=-8 EndZ=0
    g6: LineSegment StartX=23 StartY=-8 StartZ=0 EndX=23 EndY=8 EndZ=0
    g7: ArcOfCircle CenterX=-21 CenterY=11 CenterZ=0 NormalX=0 NormalY=0 NormalZ=1 AngleXU=0 Radius=1 StartAngle=6.28317 EndAngle=7.85398
    g8: ArcOfCircle CenterX=-21 CenterY=-11 CenterZ=0 NormalX=0 NormalY=0 NormalZ=1 AngleXU=0 Radius=1 StartAngle=4.71239 EndAngle=6.28319
    g9: ArcOfCircle CenterX=-39 CenterY=11 CenterZ=0 NormalX=0 NormalY=0 NormalZ=1 AngleXU=0 Radius=1 StartAngle=1.5708 EndAngle=3.14159
    g10: ArcOfCircle CenterX=-39 CenterY=-11 CenterZ=0 NormalX=0 NormalY=0 NormalZ=1 AngleXU=0 Radius=1 StartAngle=3.14159 EndAngle=4.71239
    g11: LineSegment StartX=-20 StartY=8 StartZ=0 EndX=-20 EndY=11 EndZ=0
  constraints (33):
    c: Horizontal(g0)
    c: Horizontal(g1)
    c: Vertical(g2)
    c: Horizontal(g3)
    c: Coincident(g4,g5)
    c: Horizontal(g5)
    c: Coincident(g5,g6)
    c: Coincident(g6,g0)
    c: Vertical(g6)
    c: DistanceX(g-1,g5) = 23
    c: Distance(g6) = 16
    c: Vertical(g4)
    c: Vertical(g4,g0)
    c: Tangent(g1,g7) = -1.5708
    c: Tangent(g4,g8) = -1.5708
    c: Tangent(g3,g8) = -1.5708
    c: Tangent(g2,g9) = -1.5708
    c: Tangent(g1,g9) = -1.5708
    c: Tangent(g3,g10) = -1.5708
    c: Tangent(g2,g10) = -1.5708
    c: Radius(g7) = 1
    c: Radius(g8) = 1
    c: Equal(g10,g9)
    c: Radius(g10) = 1
    c: DistanceY(g3,g1) = 24
    c: DistanceX(g-3,g2) = 20
    c: DistanceX(g4,g-1) = 20
    c: Equal(g3,g1)
    c: Coincident(g11,g0)
    c: Coincident(g11,g7)
    c: Vertical(g11)
    c: DistanceY(g-1,g0) = 8
    c: DistanceY(g-1,g1) = 12
FEATURE [Part::Extrusion] Extrude078  label="Extrude082"
  Base = -> Sketch104
  Dir = (0,0,1)
  DirMode = 2
  FaceMakerClass = Part::FaceMakerBullseye
  FaceMakerMode = 3
  LengthFwd = 80
  LengthRev = 0
  Reversed = true
  Solid = true
  Symmetric = false
FEATURE [Part::Cut] Cut030
  Base = -> Extrude077
  Tool = -> Extrude078
FEATURE [Part::Cylinder] Cylinder004  label="円柱002"
  Angle = 360
  AttacherType = Attacher::AttachEngine3D
  FirstAngle = 0
  Height = 120
  Placement = pos=(-60,0,0) rot=(0,-1,0;1.5708rad)
  Radius = 10
  SecondAngle = 0
  expr: .Placement.Base.x = -Spreadsheet012.I5
  expr: Height = Spreadsheet012.B5
  expr: Radius = Spreadsheet012.dia / 2
FEATURE [Part::MultiFuse] Fusion007  label="forkEndR"
  Shapes = -> [Cut030,Cylinder004]
FEATURE [Sketcher::SketchObject] Sketch105
  ArcFitTolerance = 0
  FullyConstrained = true
  MakeInternals = false
  Placement = pos=(0,0,0) rot=(1,0,0;1.5708rad)
  expr: Constraints[10] = Spreadsheet012.C6
  expr: Constraints[11] = Spreadsheet012.B6
  expr: Constraints[12] = Spreadsheet012.D6 / 2
  expr: Constraints[13] = Spreadsheet012.F6 / 2
  expr: Constraints[14] = Spreadsheet012.B6 / 2
  expr: Constraints[17] = Spreadsheet012.C6
  sketch-geometry (6):
    g0: LineSegment StartX=-75 StartY=0 StartZ=0 EndX=-75 EndY=16.5 EndZ=0
    g1: LineSegment StartX=-75 StartY=16.5 StartZ=0 EndX=-47 EndY=21 EndZ=0
    g2: LineSegment StartX=-47 StartY=21 StartZ=0 EndX=47 EndY=21 EndZ=0
    g3: LineSegment StartX=47 StartY=21 StartZ=0 EndX=75 EndY=16.5 EndZ=0
    g4: LineSegment StartX=75 StartY=16.5 StartZ=0 EndX=75 EndY=0 EndZ=0
    g5: LineSegment StartX=75 StartY=0 StartZ=0 EndX=-75 EndY=0 EndZ=0
  constraints (18):
    c: PointOnObject(g0,g-1)
    c: Vertical(g0)
    c: Coincident(g0,g1)
    c: Coincident(g1,g2)
    c: Horizontal(g2)
    c: Coincident(g2,g3)
    c: Coincident(g3,g4)
    c: PointOnObject(g4,g-1)
    c: Vertical(g4)
    c: Coincident(g4,g5)
    c: DistanceX(g2,g3) = 28
    c: DistanceX(g0,g3) = 150
    c: Distance(g1,g5) = 21
    c: Distance(g4) = 16.5
    c: DistanceX(g-1,g4) = 75
    c: Horizontal(g0,g3)
    c: Coincident(g5,g0)
    c: DistanceX(g0,g1) = 28
FEATURE [Part::Revolution] Revolve012
  Angle = 360
  Axis = (-1,0,0)
  AxisLink = -> Sketch105 [Edge6]
  Base = (-75,0,0)
  FaceMakerClass = Part::FaceMakerBullseye
  Solid = true
  Source = -> Sketch105
  Symmetric = false
FEATURE [Sketcher::SketchObject] Sketch012
  ArcFitTolerance = 0
  FullyConstrained = false
  MakeInternals = false
  Placement = pos=(0,0,0) rot=(0.57735,0.57735,0.57735;2.0944rad)
  expr: Constraints[16] = Spreadsheet012.F6
  expr: Constraints[17] = Spreadsheet012.F6 / 2
  sketch-geometry (8):
    g0: LineSegment StartX=-16.5 StartY=39.685 StartZ=0 EndX=-31.5 EndY=39.685 EndZ=0
    g1: LineSegment StartX=-31.5 StartY=39.685 StartZ=0 EndX=-31.5 EndY=-39.3666 EndZ=0
    g2: LineSegment StartX=-31.5 StartY=-39.3666 StartZ=0 EndX=-16.5 EndY=-39.3666 EndZ=0
    g3: LineSegment StartX=-16.5 StartY=-39.3666 StartZ=0 EndX=-16.5 EndY=39.685 EndZ=0
    g4: LineSegment StartX=16.5 StartY=39.685 StartZ=0 EndX=31.5 EndY=39.685 EndZ=0
    g5: LineSegment StartX=31.5 StartY=39.685 StartZ=0 EndX=31.5 EndY=-40.315 EndZ=0
    g6: LineSegment StartX=31.5 StartY=-40.315 StartZ=0 EndX=16.5 EndY=-40.315 EndZ=0
    g7: LineSegment StartX=16.5 StartY=-40.315 StartZ=0 EndX=16.5 EndY=39.685 EndZ=0
  constraints (22):
    c: Coincident(g0,g1)
    c: Coincident(g1,g2)
    c: Coincident(g2,g3)
    c: Coincident(g3,g0)
    c: Horizontal(g0)
    c: Horizontal(g2)
    c: Vertical(g1)
    c: Vertical(g3)
    c: Coincident(g4,g5)
    c: Coincident(g5,g6)
    c: Coincident(g6,g7)
    c: Coincident(g7,g4)
    c: Horizontal(g4)
    c: Horizontal(g6)
    c: Vertical(g5)
    c: Vertical(g7)
    c: DistanceX(g0,g4) = 33
    c: Distance(g-1,g7) = 16.5
    c: Distance(g5) = 80
    c: Distance(g4) = 15
    c: Distance(g0) = 15
    c: Horizontal(g0,g4)
FEATURE [Part::Extrusion] Extrude004  label="Extrude083"
  Base = -> Sketch012
  Dir = (1,0,0)
  DirMode = 2
  FaceMakerClass = Part::FaceMakerBullseye
  FaceMakerMode = 3
  LengthFwd = 300
  LengthRev = 0
  Solid = true
  Symmetric = true
FEATURE [Part::Cut] Cut031
  Base = -> Revolve012
  Tool = -> Extrude004
FEATURE [Sketcher::SketchObject] Sketch106
  ArcFitTolerance = 0
  FullyConstrained = true
  MakeInternals = false
  Placement = pos=(0,0,0) rot=(1,0,0;1.5708rad)
  expr: Constraints[17] = Spreadsheet012.E6
  expr: Constraints[18] = Spreadsheet012.B6 - 2 * Spreadsheet012.C6
  expr: Constraints[19] = (Spreadsheet012.B6 - 2 * Spreadsheet012.C6) / 2
  expr: Constraints[20] = Spreadsheet012.E6 / 2
  sketch-geometry (9):
    g0: LineSegment StartX=47 StartY=6.5 StartZ=0 EndX=47 EndY=-6.5 EndZ=0
    g1: LineSegment StartX=42 StartY=-11.5 StartZ=0 EndX=-42 EndY=-11.5 EndZ=0
    g2: LineSegment StartX=-47 StartY=-6.5 StartZ=0 EndX=-47 EndY=6.5 EndZ=0
    g3: LineSegment StartX=-42 StartY=11.5 StartZ=0 EndX=42 EndY=11.5 EndZ=0
    g4: GeomPoint [constr] X=0 Y=0 Z=0
    g5: ArcOfCircle CenterX=-42 CenterY=6.5 CenterZ=0 NormalX=0 NormalY=0 NormalZ=1 AngleXU=0 Radius=5 StartAngle=1.5708 EndAngle=3.14159
    g6: ArcOfCircle CenterX=-42 CenterY=-6.5 CenterZ=0 NormalX=0 NormalY=0 NormalZ=1 AngleXU=0 Radius=5 StartAngle=3.14159 EndAngle=4.71239
    g7: ArcOfCircle CenterX=42 CenterY=-6.5 CenterZ=0 NormalX=0 NormalY=0 NormalZ=1 AngleXU=0 Radius=5 StartAngle=4.71239 EndAngle=6.28319
    g8: ArcOfCircle CenterX=42 CenterY=6.5 CenterZ=0 NormalX=0 NormalY=0 NormalZ=1 AngleXU=0 Radius=5 StartAngle=0 EndAngle=1.5708
  constraints (21):
    c: Horizontal(g1)
    c: Horizontal(g3)
    c: Vertical(g0)
    c: Vertical(g2)
    c: Coincident(g4,g-1)
    c: Tangent(g3,g5) = 1.5708
    c: Tangent(g2,g5) = 1.5708
    c: Tangent(g1,g6) = 1.5708
    c: Tangent(g2,g6) = 1.5708
    c: Tangent(g1,g7) = 1.5708
    c: Tangent(g0,g7) = 1.5708
    c: Tangent(g0,g8) = 1.5708
    c: Tangent(g3,g8) = 1.5708
    c: Radius(g8) = 5
    c: Equal(g8,g7)
    c: Equal(g7,g6)
    c: Equal(g6,g5)
    c: DistanceY(g1,g3) = 23
    c: DistanceX(g2,g0) = 94
    c: Distance(g4,g2) = 47
    c: Distance(g4,g1) = 11.5
FEATURE [Part::Extrusion] Extrude079  label="Extrude005"
  Base = -> Sketch106
  Dir = (0,-1,2e-16)
  DirMode = 2
  FaceMakerClass = Part::FaceMakerBullseye
  FaceMakerMode = 3
  LengthFwd = 60
  LengthRev = 0
  Solid = true
  Symmetric = true
FEATURE [Part::Cut] Cut032
  Base = -> Cut031
  Tool = -> Extrude079
FEATURE [Sketcher::SketchObject] Sketch107
  ArcFitTolerance = 0
  FullyConstrained = true
  MakeInternals = false
  Placement = pos=(0,0,0) rot=(0.57735,0.57735,0.57735;2.0944rad)
  expr: Constraints[1] = Spreadsheet012.dia / 2
  sketch-geometry (1):
    g0: Circle CenterX=0 CenterY=0 CenterZ=0 NormalX=0 NormalY=0 NormalZ=1 AngleXU=0 Radius=10
  constraints (2):
    c: Coincident(g0,g-1)
    c: Radius(g0) = 10
FEATURE [Part::Extrusion] Extrude080  label="Extrude084"
  Base = -> Sketch107
  Dir = (1,0,0)
  DirMode = 2
  FaceMakerClass = Part::FaceMakerBullseye
  FaceMakerMode = 3
  LengthFwd = 300
  LengthRev = 0
  Solid = true
  Symmetric = true
FEATURE [Part::Cut] Cut006  label="turnBackle003"
  Base = -> Cut032
  Placement = pos=(-200,0,0) rot=(0,0,1;0rad)
  Tool = -> Extrude080
  expr: .Placement.Base.x = -(Spreadsheet012.B5 + Spreadsheet012.I5 + Spreadsheet012.dia)
FEATURE [Part::Cylinder] Cylinder001  label="rod004"
  Angle = 360
  AttacherType = Attacher::AttachEngine3D
  FirstAngle = 0
  Height = 981
  Placement = pos=(-220,0,-8.8e-14) rot=(0,-1,0;1.5708rad)
  Radius = 10
  SecondAngle = 0
  expr: .Placement.Base.x = -(Spreadsheet012.B5 + Spreadsheet012.I5 + Spreadsheet012.dia * 2)
  expr: Height = Spreadsheet012.L0 - (Spreadsheet012.B5 + Spreadsheet012.I5 + Spreadsheet012.B6 - 4 * Spreadsheet012.dia - 2 * Spreadsheet012.C6) - Spreadsheet012.B7 + Spreadsheet012.I7 - Spreadsheet012.dia
  expr: Radius = Spreadsheet012.dia / 2
FEATURE [Sketcher::SketchObject] Sketch108
  ArcFitTolerance = 0
  FullyConstrained = true
  MakeInternals = false
  MapMode = 5
  Placement = pos=(90,0,0) rot=(0.57735,0.57735,0.57735;2.0944rad)
  expr: Constraints[1] = Spreadsheet012.dia
  sketch-geometry (1):
    g0: Circle CenterX=0 CenterY=0 CenterZ=0 NormalX=0 NormalY=0 NormalZ=1 AngleXU=0 Radius=10
  constraints (2):
    c: Coincident(g0,g-1)
    c: Diameter(g0) = 20
FEATURE [Part::Extrusion] Extrude081  label="Extrude085"
  Base = -> Sketch108
  Dir = (1,0,0)
  DirMode = 2
  FaceMakerClass = Part::FaceMakerBullseye
  FaceMakerMode = 3
  LengthFwd = 30
  LengthRev = 0
  Solid = true
  Symmetric = false
  expr: LengthFwd = Spreadsheet012.I7
FEATURE [Sketcher::SketchObject] Sketch109
  ArcFitTolerance = 0
  ExternalGeometry = -> [Pad002]
  FullyConstrained = true
  MakeInternals = false
  expr: Constraints[17] = Spreadsheet012.G7
  expr: Constraints[18] = Spreadsheet012.G7 / 2
  expr: Constraints[27] = Spreadsheet012.E7 / 2
  expr: Constraints[31] = Spreadsheet012.I7
  expr: Constraints[32] = Spreadsheet012.L7
  expr: Constraints[6] = Spreadsheet012.E7
  expr: Constraints[7] = Spreadsheet012.H7
  sketch-geometry (12):
    g0: LineSegment StartX=-23 StartY=8 StartZ=0 EndX=20 EndY=8 EndZ=0
    g1: LineSegment StartX=22 StartY=12 StartZ=0 EndX=58 EndY=12 EndZ=0
    g2: LineSegment StartX=60 StartY=10 StartZ=0 EndX=60 EndY=-10 EndZ=0
    g3: LineSegment StartX=58 StartY=-12 StartZ=0 EndX=22 EndY=-12 EndZ=0
    g4: LineSegment StartX=20 StartY=-10 StartZ=0 EndX=20 EndY=-8 EndZ=0
    g5: LineSegment StartX=20 StartY=-8 StartZ=0 EndX=-23 EndY=-8 EndZ=0
    g6: LineSegment StartX=-23 StartY=-8 StartZ=0 EndX=-23 EndY=8 EndZ=0
    g7: ArcOfCircle CenterX=22 CenterY=10 CenterZ=0 NormalX=0 NormalY=0 NormalZ=1 AngleXU=0 Radius=2 StartAngle=1.5708 EndAngle=3.14159
    g8: ArcOfCircle CenterX=22 CenterY=-10 CenterZ=0 NormalX=0 NormalY=0 NormalZ=1 AngleXU=0 Radius=2 StartAngle=3.14159 EndAngle=4.71239
    g9: ArcOfCircle CenterX=58 CenterY=-10 CenterZ=0 NormalX=0 NormalY=0 NormalZ=1 AngleXU=0 Radius=2 StartAngle=4.71239 EndAngle=6.28319
    g10: ArcOfCircle CenterX=58 CenterY=10 CenterZ=0 NormalX=0 NormalY=0 NormalZ=1 AngleXU=0 Radius=2 StartAngle=5e-16 EndAngle=1.5708
    g11: LineSegment StartX=20 StartY=8 StartZ=0 EndX=20 EndY=10 EndZ=0
  constraints (33):
    c: Horizontal(g0)
    c: Coincident(g4,g5)
    c: Horizontal(g5)
    c: Coincident(g5,g6)
    c: Coincident(g6,g0)
    c: Vertical(g6)
    c: DistanceY(g6,g6) = 16
    c: DistanceX(g-1,g0) = 20
    c: Horizontal(g1)
    c: Horizontal(g3)
    c: Coincident(g11,g0)
    c: Vertical(g11)
    c: Vertical(g2)
    c: Tangent(g9,g2) = 1.5708
    c: Tangent(g1,g10) = 1.5708
    c: Tangent(g10,g2) = 1.5708
    c: Tangent(g1,g7) = 1.5708
    c: DistanceY(g3,g1) = 24
    c: DistanceY(g-1,g1) = 12
    c: Radius(g10) = 2
    c: Equal(g10,g9)
    c: Equal(g9,g7)
    c: Radius(g8) = 2
    c: Vertical(g4)
    c: Vertical(g4,g0)
    c: Tangent(g8,g4) = 1.5708
    c: Vertical(g8,g8)
    c: DistanceY(g-1,g0) = 8
    c: Tangent(g9,g3) = 1.5708
    c: Tangent(g7,g11) = 1.5708
    c: Coincident(g8,g3)
    c: DistanceX(g2,g-3) = 30
    c: DistanceX(g0,g-1) = 23
FEATURE [Part::Extrusion] Extrude082  label="Extrude086"
  Base = -> Sketch109
  Dir = (0,0,1)
  DirMode = 2
  FaceMakerClass = Part::FaceMakerBullseye
  FaceMakerMode = 3
  LengthFwd = 150
  LengthRev = 0
  Solid = true
  Symmetric = true
FEATURE [Part::Cut] Cut033
  Base = -> Pad002
  Tool = -> Extrude082
FEATURE [Part::Cut] Cut007
  Base = -> Cut033
  Tool = -> Extrude081
FEATURE [Part::Cut] Cut008  label="forkEndL"
  Base = -> Cut007
  Placement = pos=(-1255,0,0) rot=(0,0,1;0rad)
  Tool = -> Extrude076
  expr: .Placement.Base.x = -Spreadsheet012.L0
FEATURE [App::Part] Part042  label="TurnBackle"
  Group = -> [Spreadsheet012,Sketch103,Cylinder004,Cut030,Sketch104,Extrude077,Extrude078,Fusion007,Revolve012,Sketch012,Cut032,Cut031,Extrude004,Extrude079,Extrude080,Sketch106,Sketch105,Sketch107,Cut006,Cylinder001,Extrude076,Sketch102,Extrude081,Extrude082,Cut033,Cut007,Sketch108,Pad002,Sketch101,Sketch109,Cut008]
  Origin = -> Origin056
  Placement = pos=(1085.22,317,850.969) rot=(0,1,0;0.631809rad)
FEATURE [Part::FeaturePython] Clone018  label="TurnBackle001"  # Draft clone (typed FeaturePython)
  AttacherType = Attacher::AttachEngine3D
  Fuse = false
  Objects = -> [Part042]
  Placement = pos=(1085.51,-317,851.438) rot=(0,1,0;0.631809rad)
  Scale = (1,1,1)
FEATURE [App::Part] Part025  label="rakeAssy"
  Group = -> [Part024,Part022,Array015,Spreadsheet007,Part042,Clone018]
  Origin = -> Origin031
  Placement = pos=(179.94,-2.274e-13,924.66) rot=(0,1,0;-0.101229rad)
  mass = 530.337
FEATURE [Part::FeaturePython] Array016  # Draft array (typed FeaturePython)
  AlwaysSyncPlacement = false
  Angle = 360
  ArrayType = 1
  Axis = (0,0,1)
  Base = -> Part025
  Center = (0,0,7260)
  Count = 2
  ExpandArray = false
  Fuse = false
  IntervalAxis = (0,0,0)
  IntervalX = (50,0,0)
  IntervalY = (0,50,0)
  IntervalZ = (0,0,50)
  NumberCircles = 3
  NumberPolar = 2
  NumberX = 2
  NumberY = 2
  NumberZ = 1
  PlacementList = 2 placements: [(179.94,-2.274e-13,924.66),(-179.94,2.49436e-13,924.66)]
  RadialDistance = 50
  ScaleList = (2) [(1,1,1),(1,1,1)]
  Symmetry = 1
  TangentialDistance = 25
FEATURE [App::Part] Part036  label="mobingParts"
  Group = -> [Array016,Part007,Part041]
  Origin = -> Origin049
FEATURE [Spreadsheet::Sheet] Spreadsheet014  label="Spreadsheet_Assy"
  cells = A2='tankDia; B2(dia)=13500
FEATURE [Part::MultiFuse] Fusion010  label="elbow"
  Placement = pos=(-1500,0,3521) rot=(0,0,1;0rad)
  Shapes = -> [Single_flange_straight_pipe,Elbow]
  expr: .Placement.Base.x = -(<<Spreadsheet_Assy>>.dia * 0.2 / 2 + 150)
FEATURE [App::Part] Part038  label="inflowPipe"
  Group = -> [Both_flanges_straight_pipe,Both_flanges_straight_pipe001,Elbow,Single_flange_straight_pipe,Fusion010]
  Origin = -> Origin051
  mass = 627.646
FEATURE [Part::Feature] Part__Feature  label="\X2\7D426C888EAF4F5353F3\X0\_1100 v12"
  shape: bbox 15710 x 15750 x 6395 mm, 63 faces (baked)
FEATURE [Part::Feature] Part__Feature026  label="\X2\7D426C888EAF4F5353F3\X0\_1100 v013"
  shape: bbox 1000 x 1000 x 130.8 mm, 5 faces (baked)
FEATURE [Part::Feature] Part__Feature027  label="\X2\7D426C888EAF4F5353F3\X0\_1100 v014"
  shape: bbox 1000 x 1000 x 105 mm, 5 faces (baked)
FEATURE [Part::MultiFuse] Fusion011
  Refine = true
  Shapes = -> [Part__Feature,Part__Feature026,Part__Feature027]
FEATURE [Part::Part2DObjectPython] Rectangle  # Draft 2D object (typed FeaturePython)
  Area = 1.5232e+08
  ChamferSize = 0
  Columns = 1
  FilletRadius = 0
  Height = 8975.74
  Length = 16970.2
  MakeFace = true
  Placement = pos=(-8023.13,4.014e-13,-1958.45) rot=(1,0,0;1.5708rad)
  Rows = 1
FEATURE [Part::FeaturePython] Slice  # WARN: FeaturePython — macro-defined, semantics opaque (R4)
  Base = -> Fusion011
  Mode = 1
  Tolerance = 0
  Tools = -> [Rectangle]
FEATURE [Part::FeaturePython] Slice_child0  label="Slice.0"  # WARN: FeaturePython — macro-defined, semantics opaque (R4)
  Base = -> Slice
  FilterType = 1
  Invert = false
  OverrideMaxVal = 0
  WindowFrom = 80
  WindowTo = 100
  items = 0
FEATURE [Part::FeaturePython] Slice_child1  label="Slice.1"  # WARN: FeaturePython — macro-defined, semantics opaque (R4)
  Base = -> Slice
  FilterType = 1
  Invert = false
  OverrideMaxVal = 0
  WindowFrom = 80
  WindowTo = 100
  items = 1
FEATURE [App::DocumentObjectGroup] GrExplode_Slice  label="Exploded Slice"
  Group = -> [Slice_child0,Slice_child1]
FEATURE [App::Part] _X2_7D426C888EAF4F5353F3_X0__1100_v12  label="body13.5m"
  Group = -> [Part__Feature,Part__Feature026,Part__Feature027,Fusion011,Rectangle,Slice_child1,Slice,Slice_child0,GrExplode_Slice]
  Origin = -> Origin
FEATURE [Sketcher::SketchObject] Sketch122
  ArcFitTolerance = 0
  FullyConstrained = true
  MakeInternals = false
  Placement = pos=(0,0,0) rot=(1,0,0;1.5708rad)
  expr: Constraints[11] = Spreadsheet015.dia / 2
  expr: Constraints[9] = Spreadsheet015.h0
  sketch-geometry (4):
    g0: LineSegment StartX=1345 StartY=0 StartZ=0 EndX=1350 EndY=0 EndZ=0
    g1: LineSegment StartX=1350 StartY=0 StartZ=0 EndX=1350 EndY=1920 EndZ=0
    g2: LineSegment StartX=1350 StartY=1920 StartZ=0 EndX=1345 EndY=1920 EndZ=0
    g3: LineSegment StartX=1345 StartY=1920 StartZ=0 EndX=1345 EndY=0 EndZ=0
  constraints (12):
    c: Coincident(g0,g1)
    c: Coincident(g1,g2)
    c: Coincident(g2,g3)
    c: Coincident(g3,g0)
    c: Horizontal(g0)
    c: Horizontal(g2)
    c: Vertical(g1)
    c: Vertical(g3)
    c: DistanceX(g2,g2) = 5
    c: DistanceY(g1,g1) = 1920
    c: PointOnObject(g0,g-1)
    c: DistanceX(g-1,g0) = 1350
FEATURE [Part::Revolution] Revolve013
  Angle = 360
  Axis = (0,0,1)
  Base = (0,0,0)
  FaceMakerClass = Part::FaceMakerBullseye
  Solid = true
  Source = -> Sketch122
  Symmetric = false
FEATURE [Part::FeaturePython] AngleSteel017  label="AngleSteel022"  # WARN: FeaturePython — macro-defined, semantics opaque (R4)
  A = 75
  B = 75
  L = 1000
  Placement = pos=(1350,0,0) rot=(0,0,1;0rad)
  Solid = false
  g0 = 7.85
  mass = 0
  size = 10
  standard = SS_Equal
  t = 6
  expr: .Placement.Base.x = Spreadsheet015.dia / 2
FEATURE [Part::Revolution] Revolve014
  Angle = 360
  Axis = (0,0,1)
  Base = (0,0,0)
  FaceMakerClass = Part::FaceMakerBullseye
  Solid = false
  Source = -> AngleSteel017
  Symmetric = false
FEATURE [Part::FeaturePython] AngleSteel018  label="AngleSteel023"  # WARN: FeaturePython — macro-defined, semantics opaque (R4)
  A = 75
  B = 75
  L = 1000
  Placement = pos=(1350,0,1920) rot=(0,1,0;1.5708rad)
  Solid = false
  g0 = 7.85
  mass = 0
  size = 10
  standard = SS_Equal
  t = 6
  expr: .Placement.Base.x = Spreadsheet015.dia / 2
  expr: .Placement.Base.z = Spreadsheet015.h0
FEATURE [Part::Revolution] Revolve015
  Angle = 360
  Axis = (0,0,1)
  Base = (0,0,0)
  FaceMakerClass = Part::FaceMakerBullseye
  Solid = false
  Source = -> AngleSteel018
  Symmetric = false
FEATURE [Sketcher::SketchObject] Sketch123
  ArcFitTolerance = 0
  FullyConstrained = true
  MakeInternals = false
  Placement = pos=(0,0,0) rot=(1,0,0;1.5708rad)
  sketch-geometry (4):
    g0: LineSegment StartX=-275 StartY=1400 StartZ=0 EndX=275 EndY=1400 EndZ=0
    g1: LineSegment StartX=275 StartY=1400 StartZ=0 EndX=275 EndY=1920 EndZ=0
    g2: LineSegment StartX=275 StartY=1920 StartZ=0 EndX=-275 EndY=1920 EndZ=0
    g3: LineSegment StartX=-275 StartY=1920 StartZ=0 EndX=-275 EndY=1400 EndZ=0
  constraints (12):
    c: Coincident(g0,g1)
    c: Coincident(g1,g2)
    c: Coincident(g2,g3)
    c: Coincident(g3,g0)
    c: Horizontal(g0)
    c: Horizontal(g2)
    c: Vertical(g1)
    c: Vertical(g3)
    c: DistanceX(g0,g0) = 550
    c: DistanceY(g1,g1) = 520
    c: PointOnObject(g1,g-3)
    c: DistanceX(g-1,g0) = 275
FEATURE [Part::Extrusion] Extrude092  label="Extrude097"
  Base = -> Sketch123
  Dir = (0,-1,2e-16)
  DirMode = 2
  FaceMakerClass = Part::FaceMakerBullseye
  FaceMakerMode = 3
  LengthFwd = 1700
  LengthRev = 0
  Solid = true
  Symmetric = false
FEATURE [Part::MultiFuse] Fusion
  Shapes = -> [Revolve013,Revolve014,Revolve015]
FEATURE [Part::Cut] Cut036
  Base = -> Fusion
  Tool = -> Extrude092
FEATURE [Sketcher::SketchObject] Sketch124
  ArcFitTolerance = 0
  FullyConstrained = true
  MakeInternals = false
  MapMode = 5
  Placement = pos=(0,3.48e-13,0) rot=(0,0,1;0rad)
  sketch-geometry (4):
    g0: LineSegment StartX=-275 StartY=-1260.58 StartZ=0 EndX=-275 EndY=-1290.58 EndZ=0
    g1: LineSegment StartX=-275 StartY=-1260.58 StartZ=0 EndX=275 EndY=-1260.58 EndZ=0
    g2: LineSegment StartX=275 StartY=-1260.58 StartZ=0 EndX=275 EndY=-1290.58 EndZ=0
    g3: ArcOfCircle CenterX=0 CenterY=0 CenterZ=0 NormalX=0 NormalY=0 NormalZ=1 AngleXU=0 Radius=1319.55 StartAngle=4.50245 EndAngle=4.92233
  constraints (13):
    c: Vertical(g0)
    c: Coincident(g0,g1)
    c: Horizontal(g1)
    c: Coincident(g1,g2)
    c: Vertical(g2)
    c: Coincident(g3,g0)
    c: Coincident(g3,g2)
    c: PointOnObject(g-3,g0)
    c: PointOnObject(g-4,g2)
    c: DistanceY(g-3,g0) = 10
    c: DistanceY(g0,g0) = 30
    c: Coincident(g3,g-1)
    c: DistanceY(g-1,g1) = -1260.58  'brg'
FEATURE [Part::Extrusion] Extrude093  label="Extrude098"
  Base = -> Sketch124
  Dir = (0,0,1)
  DirMode = 2
  FaceMakerClass = Part::FaceMakerBullseye
  FaceMakerMode = 3
  LengthFwd = 5
  LengthRev = 0
  Placement = pos=(0,-50,1400) rot=(0,0,1;0rad)
  Solid = true
  Symmetric = false
  expr: .Placement.Base.y = -(<<Spreadsheet_feedWell>>.dia - 2600) / 2
  expr: .Placement.Base.z = <<Spreadsheet_feedWell>>.h0 - 520
FEATURE [Sketcher::SketchObject] Sketch125
  ArcFitTolerance = 0
  ExternalGeometry = -> [Extrude093]
  FullyConstrained = true
  MakeInternals = false
  MapMode = 5
  Placement = pos=(0,7.323e-12,1405) rot=(0,0,1;0rad)
  expr: .Placement.Base.z = <<Spreadsheet_feedWell>>.h0 - 520 + 5
  sketch-geometry (4):
    g0: LineSegment StartX=-275 StartY=-1325.58 StartZ=0 EndX=275 EndY=-1325.58 EndZ=0
    g1: LineSegment StartX=275 StartY=-1325.58 StartZ=0 EndX=275 EndY=-1315.58 EndZ=0
    g2: LineSegment StartX=275 StartY=-1315.58 StartZ=0 EndX=-275 EndY=-1315.58 EndZ=0
    g3: LineSegment StartX=-275 StartY=-1315.58 StartZ=0 EndX=-275 EndY=-1325.58 EndZ=0
  constraints (12):
    c: Coincident(g0,g1)
    c: Coincident(g1,g2)
    c: Coincident(g2,g3)
    c: Coincident(g3,g0)
    c: Horizontal(g0)
    c: Horizontal(g2)
    c: Vertical(g1)
    c: Vertical(g3)
    c: DistanceY(g1,g-3) = 5
    c: DistanceY(g1,g1) = 10
    c: PointOnObject(g1,g-4)
    c: PointOnObject(g2,g-5)
FEATURE [Part::Extrusion] Extrude094  label="Extrude099"
  Base = -> Sketch125
  Dir = (0,0,1)
  DirMode = 2
  FaceMakerClass = Part::FaceMakerBullseye
  FaceMakerMode = 3
  LengthFwd = 515
  LengthRev = 0
  Solid = true
  Symmetric = false
FEATURE [Sketcher::SketchObject] Sketch126
  ArcFitTolerance = 0
  FullyConstrained = true
  MakeInternals = false
  MapMode = 5
  Placement = pos=(0,-1530.41,7.07e-12) rot=(1,0,0;1.5708rad)
  sketch-geometry (4):
    g0: LineSegment StartX=-170 StartY=1920 StartZ=0 EndX=-170 EndY=1680 EndZ=0
    g1: ArcOfCircle CenterX=0 CenterY=1680 CenterZ=0 NormalX=0 NormalY=0 NormalZ=1 AngleXU=0 Radius=170 StartAngle=3.14159 EndAngle=6.28318
    g2: LineSegment StartX=170 StartY=1680 StartZ=0 EndX=170 EndY=1920 EndZ=0
    g3: LineSegment StartX=170 StartY=1920 StartZ=0 EndX=-170 EndY=1920 EndZ=0
  constraints (12):
    c: Vertical(g0)
    c: Tangent(g0,g1) = -1.5708
    c: Coincident(g1,g2)
    c: Vertical(g2)
    c: Coincident(g2,g3)
    c: Coincident(g3,g0)
    c: Horizontal(g3)
    c: Radius(g1) = 170
    c: DistanceX(g-2,g1) = 170
    c: PointOnObject(g2,g-3)
    c: Distance(g1,g3) = 240
    c: PointOnObject(g1,g-2)
FEATURE [Part::Extrusion] Extrude095  label="Extrude100"
  Base = -> Sketch126
  Dir = (0,-1,6.1e-15)
  DirMode = 2
  FaceMakerClass = Part::FaceMakerBullseye
  FaceMakerMode = 3
  LengthFwd = 1000
  LengthRev = 0
  Reversed = true
  Solid = true
  Symmetric = false
FEATURE [Part::Cut] Cut037  label="Cut001"
  Base = -> Extrude094
  Tool = -> Extrude095
FEATURE [Sketcher::SketchObject] Sketch127
  ArcFitTolerance = 0
  FullyConstrained = true
  MakeInternals = false
  MapMode = 5
  Placement = pos=(0,-1530.41,7.07e-12) rot=(1,0,0;1.5708rad)
  sketch-geometry (9):
    g0: Circle CenterX=-200 CenterY=1730 CenterZ=0 NormalX=0 NormalY=0 NormalZ=1 AngleXU=0 Radius=6
    g1: Circle CenterX=-200 CenterY=1870 CenterZ=0 NormalX=0 NormalY=0 NormalZ=1 AngleXU=0 Radius=6
    g2: Circle CenterX=200 CenterY=1870 CenterZ=0 NormalX=0 NormalY=0 NormalZ=1 AngleXU=0 Radius=6
    g3: Circle CenterX=200 CenterY=1730 CenterZ=0 NormalX=0 NormalY=0 NormalZ=1 AngleXU=0 Radius=6
    g4: Circle CenterX=-200 CenterY=1630 CenterZ=0 NormalX=0 NormalY=0 NormalZ=1 AngleXU=0 Radius=6
    g5: Circle CenterX=-200 CenterY=1460 CenterZ=0 NormalX=0 NormalY=0 NormalZ=1 AngleXU=0 Radius=6
    g6: Circle CenterX=200 CenterY=1630 CenterZ=0 NormalX=0 NormalY=0 NormalZ=1 AngleXU=0 Radius=6
    g7: Circle CenterX=200 CenterY=1460 CenterZ=0 NormalX=0 NormalY=0 NormalZ=1 AngleXU=0 Radius=6
    g8: Circle CenterX=0 CenterY=1460 CenterZ=0 NormalX=0 NormalY=0 NormalZ=1 AngleXU=0 Radius=6
  constraints (26):
    c: Radius(g0) = 6
    c: DistanceY(g-3,g0) = 50
    c: Radius(g1) = 6
    c: Vertical(g0,g1)
    c: Equal(g0,g3) = 6
    c: Equal(g1,g2) = 6
    c: Vertical(g3,g2)
    c: Radius(g4) = 6
    c: Equal(g4,g5) = 6
    c: DistanceY(g5,g4) = 170
    c: Vertical(g5,g4)
    c: Equal(g4,g6) = 6
    c: Equal(g6,g7) = 6
    c: DistanceY(g7,g6) = 170
    c: Vertical(g7,g6)
    c: PointOnObject(g8,g-2)
    c: Radius(g8) = 6
    c: Horizontal(g8,g5)
    c: DistanceY(g4,g-3) = 50
    c: Symmetric(g4,g6,g-2)
    c: Vertical(g4,g0)
    c: DistanceX(g5,g7) = 400
    c: DistanceY(g0,g1) = 140
    c: Horizontal(g0,g3)
    c: Horizontal(g1,g2)
    c: Vertical(g6,g3)
FEATURE [Part::Extrusion] Extrude096  label="Extrude101"
  Base = -> Sketch127
  Dir = (0,-1,6.1e-15)
  DirMode = 2
  FaceMakerClass = Part::FaceMakerBullseye
  FaceMakerMode = 3
  LengthFwd = 1000
  LengthRev = 0
  Reversed = true
  Solid = true
  Symmetric = false
FEATURE [Part::Cut] Cut002
  Base = -> Cut037
  Tool = -> Extrude096
FEATURE [Spreadsheet::Sheet] Spreadsheet015  label="Spreadsheet_feedWell"
  cells = A2='tankDia   D0; B2(D0)=13500; A3='depth of water  hw; B3(hw)=3200; A4='feedWell dia  dia; B4(dia)==D0 * 0.2; A5='feedWell hight  h0; B5(h0)==hw * 0.6; A6='bracket hight h1; B6(h1)=1000; A7='bracket angle ba; B7(ba)=0
FEATURE [Sketcher::SketchObject] Sketch128
  ArcFitTolerance = 0
  FullyConstrained = false
  MakeInternals = false
  Placement = pos=(0,0,0) rot=(1,0,0;1.5708rad)
  sketch-geometry (23):
    g0: LineSegment StartX=-235 StartY=2.04e-14 StartZ=0 EndX=-166.5 EndY=2.04e-14 EndZ=0
    g1: LineSegment StartX=235 StartY=0 StartZ=0 EndX=235 EndY=240 EndZ=0
    g2: LineSegment StartX=235 StartY=240 StartZ=0 EndX=-235 EndY=240 EndZ=0
    g3: LineSegment StartX=-235 StartY=240 StartZ=0 EndX=-235 EndY=2.84e-14 EndZ=0
    g4: ArcOfCircle CenterX=0 CenterY=0 CenterZ=0 NormalX=0 NormalY=0 NormalZ=1 AngleXU=0 Radius=166.5 StartAngle=0 EndAngle=3.14159
    g5: ArcOfCircle CenterX=200 CenterY=200 CenterZ=0 NormalX=0 NormalY=0 NormalZ=1 AngleXU=0 Radius=7 StartAngle=-9e-16 EndAngle=3.14159
    g6: ArcOfCircle CenterX=200 CenterY=180 CenterZ=0 NormalX=0 NormalY=0 NormalZ=1 AngleXU=0 Radius=7 StartAngle=3.14159 EndAngle=6.28319
    g7: LineSegment StartX=193 StartY=200 StartZ=0 EndX=193 EndY=180 EndZ=0
    g8: LineSegment StartX=207 StartY=180 StartZ=0 EndX=207 EndY=200 EndZ=0
    g9: ArcOfCircle CenterX=200 CenterY=60 CenterZ=0 NormalX=0 NormalY=0 NormalZ=1 AngleXU=0 Radius=7 StartAngle=0 EndAngle=3.14159
    g10: ArcOfCircle CenterX=200 CenterY=40 CenterZ=0 NormalX=0 NormalY=0 NormalZ=1 AngleXU=0 Radius=7 StartAngle=3.14159 EndAngle=6.28319
    g11: LineSegment StartX=193 StartY=60 StartZ=0 EndX=193 EndY=40 EndZ=0
    g12: LineSegment StartX=207 StartY=40 StartZ=0 EndX=207 EndY=60 EndZ=0
    g13: ArcOfCircle CenterX=-200 CenterY=200.393 CenterZ=0 NormalX=0 NormalY=0 NormalZ=1 AngleXU=0 Radius=7 StartAngle=3e-16 EndAngle=3.14159
    g14: ArcOfCircle CenterX=-200 CenterY=180.393 CenterZ=0 NormalX=0 NormalY=0 NormalZ=1 AngleXU=0 Radius=7 StartAngle=3.14159 EndAngle=6.28319
    g15: LineSegment StartX=-207 StartY=200.393 StartZ=0 EndX=-207 EndY=180.393 EndZ=0
    g16: LineSegment StartX=-193 StartY=180.393 StartZ=0 EndX=-193 EndY=200.393 EndZ=0
    g17: ArcOfCircle CenterX=-200 CenterY=60.3929 CenterZ=0 NormalX=0 NormalY=0 NormalZ=1 AngleXU=0 Radius=7 StartAngle=0 EndAngle=3.14159
    g18: ArcOfCircle CenterX=-200 CenterY=40.3929 CenterZ=0 NormalX=0 NormalY=0 NormalZ=1 AngleXU=0 Radius=7 StartAngle=3.14159 EndAngle=6.28319
    g19: LineSegment StartX=-207 StartY=60.3929 StartZ=0 EndX=-207 EndY=40.3929 EndZ=0
    g20: LineSegment StartX=-193 StartY=40.3929 StartZ=0 EndX=-193 EndY=60.3929 EndZ=0
    g21: LineSegment [constr] StartX=207.004 StartY=200.734 StartZ=0 EndX=-193 EndY=200.393 EndZ=0
    g22: LineSegment StartX=166.5 StartY=0 StartZ=0 EndX=235 EndY=0 EndZ=0
  constraints (58):
    c: Coincident(g22,g1)
    c: Coincident(g1,g2)
    c: Coincident(g2,g3)
    c: Coincident(g3,g0)
    c: Horizontal(g0)
    c: Vertical(g1)
    c: Vertical(g3)
    c: PointOnObject(g0,g-1)
    c: Coincident(g4,g-1)
    c: Radius(g4) = 166.5
    c: DistanceX(g2,g2) = 470
    c: Symmetric(g1,g2,g-2)
    c: DistanceY(g1,g1) = 240
    c: DistanceX(g5,g5) = 14
    c: DistanceY(g7,g7) = 20
    c: DistanceY(g5,g1) = 40
    c: DistanceX(g4,g5) = 200
    c: Tangent(g9,g11) = -1.5708
    c: Tangent(g11,g10) = -1.5708
    c: Tangent(g10,g12) = -1.5708
    c: Tangent(g12,g9) = -1.5708
    c: Equal(g9,g10)
    c: Vertical(g11)
    c: Equal(g5,g9) = 14
    c: Equal(g7,g11) = 20
    c: Vertical(g9,g6)
    c: DistanceY(g9,g5) = 140
    c: Equal(g5,g13) = 14
    c: Equal(g7,g15) = 20
    c: Tangent(g17,g19) = -1.5708
    c: Tangent(g19,g18) = -1.5708
    c: Tangent(g18,g20) = -1.5708
    c: Tangent(g20,g17) = -1.5708
    c: Equal(g17,g18)
    c: Vertical(g19)
    c: Equal(g13,g17) = 14
    c: Equal(g15,g19) = 20
    c: Vertical(g17,g14)
    c: DistanceY(g17,g13) = 140
    c: Angle(g21) = -3.14074
    c: Coincident(g0,g4)
    c: Coincident(g22,g4)
    c: Horizontal(g22)
    c: PointOnObject(g1,g-1)
    c: Vertical(g16)
    c: Vertical(g15)
    c: Coincident(g13,g21)
    c: Tangent(g5,g8) = -1.5708
    c: Tangent(g16,g13) = -1.5708
    c: Tangent(g15,g14) = -1.5708
    c: Tangent(g16,g14) = -1.5708
    c: Tangent(g15,g13) = -1.5708
    c: DistanceX(g13,g4) = 200
    c: Vertical(g8)
    c: Vertical(g7)
    c: Tangent(g5,g7) = -1.5708
    c: Tangent(g7,g6) = -1.5708
    c: Tangent(g8,g6) = -1.5708
FEATURE [Part::Extrusion] Extrude097  label="Extrude102"
  Base = -> Sketch128
  Dir = (0,-1,2e-16)
  DirMode = 2
  FaceMakerClass = Part::FaceMakerBullseye
  FaceMakerMode = 3
  LengthFwd = 10
  LengthRev = 0
  Solid = true
  Symmetric = false
FEATURE [Sketcher::SketchObject] Sketch129
  ArcFitTolerance = 0
  ExternalGeometry = -> [Extrude097]
  FullyConstrained = false
  MakeInternals = false
  Placement = pos=(0,0,0) rot=(1,0,0;1.5708rad)
  sketch-geometry (26):
    g0: LineSegment StartX=-235 StartY=0 StartZ=0 EndX=-166.5 EndY=-2.04e-14 EndZ=0
    g1: LineSegment StartX=235 StartY=0 StartZ=0 EndX=235 EndY=-267.623 EndZ=0
    g2: LineSegment StartX=235 StartY=-267.623 StartZ=0 EndX=-235 EndY=-267.623 EndZ=0
    g3: LineSegment StartX=-235 StartY=-267.623 StartZ=0 EndX=-235 EndY=0 EndZ=0
    g4: ArcOfCircle CenterX=0 CenterY=-2.04e-14 CenterZ=0 NormalX=0 NormalY=0 NormalZ=1 AngleXU=0 Radius=166.5 StartAngle=3.14159 EndAngle=6.28319
    g5: ArcOfCircle CenterX=200 CenterY=-40 CenterZ=0 NormalX=0 NormalY=0 NormalZ=1 AngleXU=0 Radius=7 StartAngle=3e-16 EndAngle=3.14159
    g6: ArcOfCircle CenterX=200 CenterY=-60 CenterZ=0 NormalX=0 NormalY=0 NormalZ=1 AngleXU=0 Radius=7 StartAngle=3.14159 EndAngle=6.28319
    g7: LineSegment StartX=193 StartY=-40 StartZ=0 EndX=193 EndY=-60 EndZ=0
    g8: LineSegment StartX=207 StartY=-60 StartZ=0 EndX=207 EndY=-40 EndZ=0
    g9: ArcOfCircle CenterX=200 CenterY=-210 CenterZ=0 NormalX=0 NormalY=0 NormalZ=1 AngleXU=0 Radius=7 StartAngle=0 EndAngle=3.14159
    g10: ArcOfCircle CenterX=200 CenterY=-230 CenterZ=0 NormalX=0 NormalY=0 NormalZ=1 AngleXU=0 Radius=7 StartAngle=3.14159 EndAngle=6.28319
    g11: LineSegment StartX=193 StartY=-210 StartZ=0 EndX=193 EndY=-230 EndZ=0
    g12: LineSegment StartX=207 StartY=-230 StartZ=0 EndX=207 EndY=-210 EndZ=0
    g13: ArcOfCircle CenterX=-200 CenterY=-40 CenterZ=0 NormalX=0 NormalY=0 NormalZ=1 AngleXU=0 Radius=7 StartAngle=0 EndAngle=3.14159
    g14: ArcOfCircle CenterX=-200 CenterY=-60 CenterZ=0 NormalX=0 NormalY=0 NormalZ=1 AngleXU=0 Radius=7 StartAngle=3.14159 EndAngle=6.28319
    g15: LineSegment StartX=-207 StartY=-40 StartZ=0 EndX=-207 EndY=-60 EndZ=0
    g16: LineSegment StartX=-193 StartY=-60 StartZ=0 EndX=-193 EndY=-40 EndZ=0
    g17: ArcOfCircle CenterX=-200 CenterY=-210 CenterZ=0 NormalX=0 NormalY=0 NormalZ=1 AngleXU=0 Radius=7 StartAngle=1.4e-15 EndAngle=3.14159
    g18: ArcOfCircle CenterX=-200 CenterY=-230 CenterZ=0 NormalX=0 NormalY=0 NormalZ=1 AngleXU=0 Radius=7 StartAngle=3.14159 EndAngle=6.28319
    g19: LineSegment StartX=-207 StartY=-210 StartZ=0 EndX=-207 EndY=-230 EndZ=0
    g20: LineSegment StartX=-193 StartY=-230 StartZ=0 EndX=-193 EndY=-210 EndZ=0
    g21: LineSegment StartX=166.5 StartY=-2.04e-14 StartZ=0 EndX=235 EndY=0 EndZ=0
    g22: ArcOfCircle CenterX=0 CenterY=-210 CenterZ=0 NormalX=0 NormalY=0 NormalZ=1 AngleXU=0 Radius=7 StartAngle=-9e-16 EndAngle=3.14159
    g23: ArcOfCircle CenterX=0 CenterY=-230 CenterZ=0 NormalX=0 NormalY=0 NormalZ=1 AngleXU=0 Radius=7 StartAngle=3.14159 EndAngle=6.28319
    g24: LineSegment StartX=-7 StartY=-210 StartZ=0 EndX=-7 EndY=-230 EndZ=0
    g25: LineSegment StartX=7 StartY=-230 StartZ=0 EndX=7 EndY=-210 EndZ=0
  constraints (65):
    c: Coincident(g21,g1)
    c: Coincident(g1,g2)
    c: Coincident(g2,g3)
    c: Coincident(g3,g0)
    c: Horizontal(g2)
    c: Vertical(g1)
    c: Vertical(g3)
    c: Coincident(g21,g-3)
    c: Coincident(g0,g-4)
    c: Coincident(g4,g-1)
    c: Horizontal(g4,g4)
    c: Horizontal(g4,g4)
    c: Tangent(g5,g7) = -1.5708
    c: Tangent(g7,g6) = -1.5708
    c: Tangent(g6,g8) = -1.5708
    c: Tangent(g8,g5) = -1.5708
    c: Equal(g5,g6)
    c: Vertical(g7)
    c: DistanceY(g8,g8) = 20
    c: DistanceX(g5,g5) = 14
    c: Vertical(g5,g-5)
    c: DistanceY(g5,g4) = 40
    c: Tangent(g9,g11) = -1.5708
    c: Tangent(g11,g10) = -1.5708
    c: Tangent(g10,g12) = -1.5708
    c: Tangent(g12,g9) = -1.5708
    c: Equal(g9,g10)
    c: Vertical(g11)
    c: Equal(g8,g12) = 20
    c: Equal(g5,g9) = 14
    c: Vertical(g6,g9)
    c: Tangent(g13,g15) = -1.5708
    c: Tangent(g15,g14) = -1.5708
    c: Tangent(g14,g16) = -1.5708
    c: Tangent(g16,g13) = -1.5708
    c: Equal(g13,g14)
    c: Vertical(g15)
    c: Equal(g8,g16) = 20
    c: Equal(g5,g13) = 14
    c: Tangent(g17,g19) = -1.5708
    c: Tangent(g19,g18) = -1.5708
    c: Tangent(g18,g20) = -1.5708
    c: Tangent(g20,g17) = -1.5708
    c: Equal(g17,g18)
    c: Vertical(g19)
    c: Equal(g16,g20) = 20
    c: Equal(g13,g17) = 14
    c: Vertical(g14,g17)
    c: Tangent(g22,g24) = -1.5708
    c: Tangent(g24,g23) = -1.5708
    c: Tangent(g23,g25) = -1.5708
    c: Tangent(g25,g22) = -1.5708
    c: Equal(g22,g23)
    c: Vertical(g24)
    c: DistanceX(g22,g22) = 14
    c: DistanceY(g24,g24) = 20
    c: PointOnObject(g22,g-2)
    c: Horizontal(g9,g22)
    c: DistanceY(g9,g5) = 170
    c: DistanceY(g17,g13) = 170
    c: DistanceX(g14,g6) = 400
    c: DistanceY(g13,g0) = 40
    c: Coincident(g0,g4)
    c: Coincident(g4,g21)
    c: Radius(g4) = 166.5
FEATURE [Part::Extrusion] Extrude098  label="Extrude103"
  Base = -> Sketch129
  Dir = (0,-1,2e-16)
  DirMode = 2
  FaceMakerClass = Part::FaceMakerBullseye
  FaceMakerMode = 3
  LengthFwd = 10
  LengthRev = 0
  Solid = true
  Symmetric = false
FEATURE [App::Part] Part  label="pipeBrg"
  Group = -> [Sketch128,Sketch129,Extrude097,Extrude098]
  Origin = -> Origin061
  Placement = pos=(0,-1325.6,1680) rot=(0,0,1;0rad)
  expr: .Placement.Base.y = -<<Spreadsheet_feedWell>>.dia / 2 + 24.4
  expr: .Placement.Base.z = <<Spreadsheet_feedWell>>.h0 - 260 + 20
FEATURE [Sketcher::SketchObject] Sketch008
  ArcFitTolerance = 0
  FullyConstrained = false
  MakeInternals = false
  sketch-geometry (4):
    g0: LineSegment StartX=1299.04 StartY=50 StartZ=0 EndX=1507.04 EndY=50 EndZ=0
    g1: LineSegment StartX=1507.04 StartY=50 StartZ=0 EndX=1507.04 EndY=-50 EndZ=0
    g2: LineSegment StartX=1507.04 StartY=-50 StartZ=0 EndX=1299.04 EndY=-50 EndZ=0
    g3: ArcOfCircle CenterX=-0.0298456 CenterY=4.574e-13 CenterZ=0 NormalX=0 NormalY=0 NormalZ=1 AngleXU=0 Radius=1300.03 StartAngle=6.24472 EndAngle=6.32166
  constraints (12):
    c: Horizontal(g0)
    c: Coincident(g0,g1)
    c: Vertical(g1)
    c: Coincident(g1,g2)
    c: Horizontal(g2)
    c: DistanceY(g-1,g0) = 50
    c: DistanceY(g1,g1) = 100
    c: Coincident(g3,g2)
    c: Coincident(g3,g0)
    c: PointOnObject(g0,g-5)
    c: PointOnObject(g2,g-6)
    c: DistanceX(g0,g0) = 208
FEATURE [Part::Extrusion] Extrude099  label="Extrude104"
  Base = -> Sketch008
  Dir = (0,0,1)
  DirMode = 2
  FaceMakerClass = Part::FaceMakerBullseye
  FaceMakerMode = 3
  LengthFwd = 10
  LengthRev = 0
  Solid = true
  Symmetric = false
FEATURE [Sketcher::SketchObject] Sketch130
  ArcFitTolerance = 0
  ExternalGeometry = -> [Extrude099]
  FullyConstrained = true
  MakeInternals = false
  MapMode = 5
  Placement = pos=(0,0,10) rot=(0,0,1;0rad)
  sketch-geometry (8):
    g0: LineSegment StartX=1299.04 StartY=50 StartZ=0 EndX=1507.04 EndY=50 EndZ=0
    g1: LineSegment StartX=1507.04 StartY=50 StartZ=0 EndX=1507.04 EndY=45 EndZ=0
    g2: LineSegment StartX=1507.04 StartY=45 StartZ=0 EndX=1299.04 EndY=45 EndZ=0
    g3: LineSegment StartX=1299.04 StartY=45 StartZ=0 EndX=1299.04 EndY=50 EndZ=0
    g4: LineSegment StartX=1299.04 StartY=-50 StartZ=0 EndX=1507.04 EndY=-50 EndZ=0
    g5: LineSegment StartX=1507.04 StartY=-50 StartZ=0 EndX=1507.04 EndY=-45 EndZ=0
    g6: LineSegment StartX=1507.04 StartY=-45 StartZ=0 EndX=1299.04 EndY=-45 EndZ=0
    g7: LineSegment StartX=1299.04 StartY=-45 StartZ=0 EndX=1299.04 EndY=-50 EndZ=0
  constraints (22):
    c: Coincident(g0,g1)
    c: Coincident(g1,g2)
    c: Coincident(g2,g3)
    c: Coincident(g3,g0)
    c: Horizontal(g0)
    c: Horizontal(g2)
    c: Vertical(g1)
    c: Vertical(g3)
    c: Coincident(g4,g5)
    c: Coincident(g5,g6)
    c: Coincident(g6,g7)
    c: Coincident(g7,g4)
    c: Horizontal(g4)
    c: Horizontal(g6)
    c: Vertical(g5)
    c: Vertical(g7)
    c: Coincident(g0,g-3)
    c: DistanceY(g1,g1) = 5
    c: DistanceY(g5,g5) = 5
    c: Coincident(g4,g-3)
    c: Vertical(g2,g6)
    c: PointOnObject(g4,g-4)
FEATURE [Part::Extrusion] Extrude100  label="Extrude105"
  Base = -> Sketch130
  Dir = (0,0,1)
  DirMode = 2
  FaceMakerClass = Part::FaceMakerBullseye
  FaceMakerMode = 3
  LengthFwd = 200
  LengthRev = 0
  Solid = true
  Symmetric = false
FEATURE [Part::Chamfer] Chamfer
  Base = -> Extrude100
  EdgeLinks = -> Extrude100 [Edge7,Edge19]
  Edges = 2 edges: [Edge7 r1=130 r2=70,Edge19 r1=130 r2=70]
FEATURE [Part::Compound] Compound025  label="gusset001"
  Links = -> [Extrude099,Chamfer]
FEATURE [Sketcher::SketchObject] Sketch131
  ArcFitTolerance = 0
  ExternalGeometry = -> [Compound025]
  FullyConstrained = true
  MakeInternals = false
  MapMode = 5
  Placement = pos=(0,0,10) rot=(0,0,1;0rad)
  sketch-geometry (1):
    g0: Circle CenterX=1532.04 CenterY=0 CenterZ=0 NormalX=0 NormalY=0 NormalZ=1 AngleXU=0 Radius=7
  constraints (3):
    c: Diameter(g0) = 14
    c: PointOnObject(g0,g-1)
    c: Distance(g0,g-3) = 25
FEATURE [Part::Extrusion] Extrude101  label="Extrude106"
  Base = -> Sketch131
  Dir = (0,0,1)
  DirMode = 2
  FaceMakerClass = Part::FaceMakerBullseye
  FaceMakerMode = 3
  LengthFwd = 10
  LengthRev = 0
  Reversed = true
  Solid = true
  Symmetric = false
FEATURE [Part::Cut] Cut003
  Base = -> Compound025
  Placement = pos=(50,0,998.5) rot=(0,0,1;0rad)
  Tool = -> Extrude101
  expr: .Placement.Base.x = (<<Spreadsheet_feedWell>>.dia - 2600) / 2
  expr: .Placement.Base.z = Spreadsheet015.h1 - 1.5
FEATURE [Sketcher::SketchObject] Sketch132
  ArcFitTolerance = 0
  FullyConstrained = true
  MakeInternals = false
  Placement = pos=(0,0,0) rot=(1,0,0;1.5708rad)
  sketch-geometry (4):
    g0: LineSegment StartX=0 StartY=0 StartZ=0 EndX=150 EndY=0 EndZ=0
    g1: LineSegment StartX=150 StartY=0 StartZ=0 EndX=150 EndY=300 EndZ=0
    g2: LineSegment StartX=150 StartY=300 StartZ=0 EndX=0 EndY=300 EndZ=0
    g3: LineSegment StartX=0 StartY=300 StartZ=0 EndX=0 EndY=0 EndZ=0
  constraints (11):
    c: Coincident(g0,g1)
    c: Coincident(g1,g2)
    c: Coincident(g2,g3)
    c: Coincident(g3,g0)
    c: Horizontal(g0)
    c: Horizontal(g2)
    c: Vertical(g1)
    c: Vertical(g3)
    c: Coincident(g0,g-1)
    c: DistanceX(g2,g2) = 150
    c: DistanceY(g1,g1) = 300
FEATURE [Part::Extrusion] Extrude102  label="Extrude107"
  Base = -> Sketch132
  Dir = (0,-1,2e-16)
  DirMode = 2
  FaceMakerClass = Part::FaceMakerBullseye
  FaceMakerMode = 3
  LengthFwd = 6
  LengthRev = 0
  Solid = true
  Symmetric = true
FEATURE [Part::FeaturePython] AngleSteel003  # WARN: FeaturePython — macro-defined, semantics opaque (R4)
  A = 75
  B = 75
  L = 300
  Placement = pos=(117.5,40.5,0) rot=(0,0,1;3.14159rad)
  Solid = true
  g0 = 7.85
  mass = 2.05506
  size = 10
  standard = SS_Equal
  t = 6
FEATURE [Part::Mirroring] Mirror018  label="AngleSteel003 (mirrored)"
  Base = (200,0,0)
  Normal = (0,1,0)
  Source = -> AngleSteel003
FEATURE [Part::Compound] Compound026  label="gusset002"
  Links = -> [Extrude102,Mirror018,AngleSteel003]
  Placement = pos=(6450,-1469.5,750) rot=(0,0,1;0rad)
  expr: .Placement.Base.x = Spreadsheet015.D0 / 2 - 300
  expr: .Placement.Base.y = -<<Spreadsheet_feedWell>>.dia / 2 - 119.5
FEATURE [Part::FeaturePython] Array030  # Draft array (typed FeaturePython)
  AlwaysSyncPlacement = false
  Angle = 360
  ArrayType = 1
  Axis = (0,0,1)
  Base = -> Cut003
  Center = (0,0,0)
  Count = 4
  ExpandArray = false
  Fuse = false
  IntervalAxis = (0,0,0)
  IntervalX = (50,0,0)
  IntervalY = (0,50,0)
  IntervalZ = (0,0,50)
  NumberCircles = 3
  NumberPolar = 4
  NumberX = 2
  NumberY = 2
  NumberZ = 1
  PlacementList = 4 placements: [(50,0,998.5),(0,50,998.5),(-50,6.12323e-15,998.5),(-1.11022e-14,-50,998.5)]
  RadialDistance = 50
  ScaleList = (4) [(1,1,1),(1,1,1),(1,1,1),(1,1,1)]
  Symmetry = 1
  TangentialDistance = 25
  expr: .Placement.Rotation.Angle = <<Spreadsheet_feedWell>>.ba
FEATURE [App::Part] Part045  label="centerWell"
  Group = -> [Chamfer,Sketch127,Sketch131,Sketch130,Sketch008,Compound025,Revolve013,Revolve014,Revolve015,Extrude093,Extrude100,Extrude096,Extrude095,Extrude092,Extrude094,Extrude099,Extrude101,Sketch123,Sketch125,Sketch122,Sketch124,Sketch126,AngleSteel017,AngleSteel018,Cut003,Fusion,Cut037,Cut036,Cut002,Array030,Part]
  Origin = -> Origin062
  Placement = pos=(0,0,0) rot=(0,0,1;1.5708rad)
  mass = 783.909
FEATURE [Part::Mirroring] Mirror009  label="gusset001 (mirrored)"
  Base = (0,0,0)
  Normal = (1,0,0)
  Source = -> Compound026
FEATURE [Part::Mirroring] Mirror010  label="gusset001 (mirrored) (mirrored)"
  Base = (0,0,0)
  Normal = (0,1,0)
  Source = -> Mirror009
FEATURE [Part::Mirroring] Mirror011  label="gusset001 (mirrored)001"
  Base = (0,0,0)
  Normal = (0,1,0)
  Source = -> Compound026
FEATURE [Part::FeaturePython] ChannelSteel006  # WARN: FeaturePython — macro-defined, semantics opaque (R4)
  B = 65
  H = 125
  L = 2920
  Placement = pos=(1520,-1450,0) rot=(-1,0,0;1.5708rad)
  Solid = true
  g0 = 7.85
  mass = 35.2721
  size = 2
  standard = SS
  t1 = 6
  t2 = 8
  expr: .Placement.Base.x = Spreadsheet015.dia / 2 + 170
  expr: .Placement.Base.y = -<<Spreadsheet_feedWell>>.dia / 2 - 100
  expr: L = Spreadsheet015.dia + 220
FEATURE [Sketcher::SketchObject] Sketch133
  ArcFitTolerance = 0
  FullyConstrained = false
  MakeInternals = false
  Placement = pos=(0,0,0) rot=(1,0,0;1.5708rad)
  expr: Constraints[2] = Spreadsheet016.Gb0
  expr: Constraints[5] = Spreadsheet016.rp0
  expr: Constraints[8] = Spreadsheet016.H0 - 60
  sketch-geometry (3):
    g0: LineSegment StartX=200 StartY=44.4 StartZ=0 EndX=725 EndY=734.4 EndZ=0
    g1: LineSegment StartX=725 StartY=734.4 StartZ=0 EndX=1250 EndY=44.4 EndZ=0
    g2: LineSegment [constr] StartX=725 StartY=734.4 StartZ=0 EndX=725 EndY=523.53 EndZ=0
  constraints (9):
    c: Coincident(g0,g1)
    c: Horizontal(g0,g1)
    c: DistanceX(g-1,g0) = 200
    c: Coincident(g2,g0)
    c: Symmetric(g1,g0,g2)
    c: DistanceX(g0,g1) = 1050
    c: DistanceY(g-1,g-4) = 14.4
    c: DistanceY(g-4,g0) = 30
    c: DistanceY(g0,g0) = 690
FEATURE [Sketcher::SketchObject] Sketch134
  ArcFitTolerance = 0
  ExternalGeometry = -> [Sketch133]
  FullyConstrained = true
  MakeInternals = false
  Placement = pos=(0,0,14.4) rot=(1,0,0;1.5708rad)
  expr: Constraints[23] = Spreadsheet016.Lb0
  expr: Constraints[24] = Spreadsheet016.H0 - 20
  expr: Constraints[25] = Spreadsheet016.Lb0 / 2
  sketch-geometry (9):
    g0: LineSegment StartX=200 StartY=71.2867 StartZ=0 EndX=708.804 EndY=740 EndZ=0
    g1: LineSegment StartX=725 StartY=678.713 StartZ=0 EndX=216.196 EndY=10 EndZ=0
    g2: LineSegment StartX=725 StartY=678.713 StartZ=0 EndX=1233.8 EndY=10 EndZ=0
    g3: LineSegment StartX=1250 StartY=71.2867 StartZ=0 EndX=741.196 EndY=740 EndZ=0
    g4: LineSegment StartX=708.804 StartY=740 StartZ=0 EndX=741.196 EndY=740 EndZ=0
    g5: LineSegment StartX=1233.8 StartY=10 StartZ=0 EndX=1250 EndY=10 EndZ=0
    g6: LineSegment StartX=1250 StartY=10 StartZ=0 EndX=1250 EndY=71.2867 EndZ=0
    g7: LineSegment StartX=216.196 StartY=10 StartZ=0 EndX=200 EndY=10 EndZ=0
    g8: LineSegment StartX=200 StartY=10 StartZ=0 EndX=200 EndY=71.2867 EndZ=0
  constraints (27):
    c: Coincident(g7,g8)
    c: Coincident(g0,g8)
    c: Coincident(g1,g7)
    c: Coincident(g0,g4)
    c: Coincident(g1,g2)
    c: Coincident(g3,g4)
    c: Coincident(g2,g5)
    c: Coincident(g5,g6)
    c: Coincident(g3,g6)
    c: Horizontal(g7)
    c: Horizontal(g4)
    c: Vertical(g8)
    c: Vertical(g7,g-4)
    c: Horizontal(g0,g3)
    c: Horizontal(g5)
    c: Horizontal(g1,g2)
    c: Vertical(g6)
    c: PointOnObject(g-3,g6)
    c: Parallel(g1,g-4)
    c: Parallel(g1,g0)
    c: Parallel(g2,g-3)
    c: Parallel(g-3,g3)
    c: Vertical(g1,g-4)
    c: Distance(g1,g0) = 50
    c: DistanceY(g2,g3) = 730
    c: Distance(g1,g-4) = 25
    c: DistanceY(g-5,g7) = 10
FEATURE [Part::Extrusion] Extrude015  label="Extrude108"
  Base = -> Sketch134
  Dir = (0,-1,2e-16)
  DirMode = 2
  FaceMakerClass = Part::FaceMakerBullseye
  FaceMakerMode = 3
  LengthFwd = 6
  LengthRev = 0
  Placement = pos=(0,28.8,0) rot=(0,0,1;0rad)
  Solid = true
  Symmetric = false
FEATURE [Part::FeaturePython] Array031  # Draft array (typed FeaturePython)
  AlwaysSyncPlacement = false
  Angle = 360
  ArrayType = 0
  Axis = (0,0,1)
  Base = -> Extrude015
  Center = (0,0,0)
  Count = 12
  ExpandArray = false
  Fuse = false
  IntervalAxis = (0,0,0)
  IntervalX = (1050,0,0)
  IntervalY = (0,100,0)
  IntervalZ = (0,0,100)
  NumberCircles = 3
  NumberPolar = 5
  NumberX = 12
  NumberY = 1
  NumberZ = 1
  PlacementList = 12 placements: arithmetic series from (0,28.8,0) step (1050,0,0) to (11550,28.8,0)
  RadialDistance = 50
  ScaleList = (12) [(1,1,1),(1,1,1),(1,1,1),(1,1,1),(1,1,1),(1,1,1),(1,1,1),(1,1,1),(1,1,1),(1,1,1),(1,1,1),(1,1,1)]
  Symmetry = 1
  TangentialDistance = 25
  expr: .IntervalX.x = Spreadsheet016.rp0
  expr: NumberX = Spreadsheet016.rn0
FEATURE [Spreadsheet::Sheet] Spreadsheet016  label="Spreadsheet_support"
  cells = A2='梁成H0; B2(H0)=750; A3='梁長L0; B3(L0)=13000; A4='玄材shp; B4(shp)='75x75x6; A5='玄材ゲージラインGL0; B5(GL0)=40; A6='ラチス材Lshp; B6(Lshp)='6x50; A7='ラチス材幅Lb0; B7(Lb0)=50; A8='ラチス材厚Lt0; B8(Gt0)=6; A9='ガセットプレート幅Gb0; B9(Gb0)=200; A10='ラチスピッチrp0; B10(rp0)==(L0 - 2 * Gb0) / rn0; A11='ラチス配列数rn0; B11(rn0)=12; B16='t; C16='A; D16='GLine; A17='40x40x3; B17=3; C17=40; D17=22; A18='40x40x5; B18=5; C18=40; D18=22; A19='50x50x4; B19=4; C19=50; D19=30; A20='50x50x6; B20=6; C20=50; D20=30; A21='65x65x6; B21=6; C21=65; D21=35; A22='65x65x8; B22=8; C22=65; D22=35; A23='75x75x6; B23=6; C23=75; D23=40; A24='75x75x9; B24=9; C24=75; D24=40; A25='75x75x12; B25=12; C25=75; D25=40; A26='90x90x7; B26=7; C26=90; D26=50; A27='90x90x10; B27=10; C27=90; D27=50; A28='90x90x13; B28=13; C28=90; D28=50; A29='100x100x7; B29=7; C29=100; D29=55; A30='100x100x10; B30=10; C30=100; D30=55; A31='100x100x13; B31=13; C31=100; D31=55; A34='6x38; B34=6; C34=38; A35='9x38; B35=9; C35=38; A36='6x44; B36=6; C36=44; A37='9x44; B37=9; C37=44; A38='4.5x50; B38=4.5; C38=50; A39='6x50; B39=6; C39=50; A40='9x50; B40=9; C40=50; A41='6x65; B41=6; C41=65; A42='9x65; B42=9; C42=65; A43='6x75; B43=6; C43=75; A44='9x75; B44=9; C44=75; A45='6x90; B45=6; C45=90; A46='9x90; B46=9; C46=90
FEATURE [Sketcher::SketchObject] Sketch135
  ArcFitTolerance = 0
  FullyConstrained = true
  MakeInternals = false
  Placement = pos=(0,0,14.4) rot=(1,0,0;1.5708rad)
  expr: Constraints[22] = Spreadsheet016.L0
  sketch-geometry (8):
    g0: LineSegment StartX=0 StartY=10 StartZ=0 EndX=200 EndY=10 EndZ=0
    g1: LineSegment StartX=200 StartY=10 StartZ=0 EndX=200 EndY=690 EndZ=0
    g2: LineSegment StartX=200 StartY=690 StartZ=0 EndX=0 EndY=690 EndZ=0
    g3: LineSegment StartX=0 StartY=690 StartZ=0 EndX=0 EndY=10 EndZ=0
    g4: LineSegment StartX=13000 StartY=690 StartZ=0 EndX=12800 EndY=690 EndZ=0
    g5: LineSegment StartX=12800 StartY=690 StartZ=0 EndX=12800 EndY=10 EndZ=0
    g6: LineSegment StartX=12800 StartY=10 StartZ=0 EndX=13000 EndY=10 EndZ=0
    g7: LineSegment StartX=13000 StartY=10 StartZ=0 EndX=13000 EndY=690 EndZ=0
  constraints (23):
    c: Coincident(g0,g1)
    c: Coincident(g1,g2)
    c: Coincident(g2,g3)
    c: Coincident(g3,g0)
    c: Horizontal(g0)
    c: Horizontal(g2)
    c: Vertical(g1)
    c: Vertical(g3)
    c: Vertical(g-1,g0)
    c: Coincident(g0,g-3)
    c: Horizontal(g1,g-4)
    c: Coincident(g4,g5)
    c: Coincident(g5,g6)
    c: Coincident(g6,g7)
    c: Coincident(g7,g4)
    c: Horizontal(g4)
    c: Horizontal(g6)
    c: Vertical(g5)
    c: Vertical(g7)
    c: Equal(g0,g6)
    c: Horizontal(g6,g0)
    c: Horizontal(g1,g4)
    c: DistanceX(g0,g6) = 13000
FEATURE [Part::Extrusion] Extrude016  label="Extrude109"
  Base = -> Sketch135
  Dir = (0,-1,2e-16)
  DirMode = 2
  FaceMakerClass = Part::FaceMakerBullseye
  FaceMakerMode = 3
  LengthFwd = 6
  LengthRev = 0
  Placement = pos=(0,28.8,0) rot=(0,0,1;0rad)
  Solid = true
  Symmetric = false
  expr: LengthFwd = Spreadsheet016.Gt0
FEATURE [Part::FeaturePython] AngleSteel004  # WARN: FeaturePython — macro-defined, semantics opaque (R4)
  A = 75
  B = 75
  L = 1000
  Placement = pos=(0,28.8,14.4) rot=(0,0,1;1.5708rad)
  Solid = false
  g0 = 7.85
  mass = 0
  size = 10
  standard = SS_Equal
  t = 8
FEATURE [Part::Mirroring] Mirror019  label="AngleSteel (mirrored)"
  Base = (-2.54e-14,114.396,14.3963)
  Normal = (0,0,-1)
  Placement = pos=(0,0,750) rot=(0,0,1;0rad)
  Source = -> AngleSteel004
  expr: .Placement.Base.z = Spreadsheet016.H0
FEATURE [Part::Extrusion] Extrude103  label="Extrude110"
  Base = -> AngleSteel004
  Dir = (-1,-2e-16,0)
  DirMode = 2
  FaceMakerClass = Part::FaceMakerBullseye
  FaceMakerMode = 3
  LengthFwd = 13000
  LengthRev = 0
  Reversed = true
  Solid = false
  Symmetric = false
  expr: LengthFwd = Spreadsheet016.L0
FEATURE [Part::Extrusion] Extrude104  label="Extrude111"
  Base = -> Mirror019
  Dir = (-1,-2e-16,0)
  DirMode = 2
  FaceMakerClass = Part::FaceMakerBullseye
  FaceMakerMode = 3
  LengthFwd = 13000
  LengthRev = 0
  Reversed = true
  Solid = false
  Symmetric = false
  expr: LengthFwd = Spreadsheet016.L0
FEATURE [Part::MultiFuse] Fusion001
  Shapes = -> [Extrude104,Extrude103]
FEATURE [Part::Mirroring] Mirror020  label="Fusion (mirrored)"
  Base = (-3.2e-15,28.7963,514.396)
  Normal = (0,-1,0)
  Placement = pos=(0,-6,0) rot=(0,0,1;0rad)
  Source = -> Fusion001
  expr: .Placement.Base.y = -Spreadsheet016.Gt0
FEATURE [Part::Compound] Compound027
  Links = -> [Mirror020,Fusion001]
FEATURE [App::Part] Part048  label="latticeBeam"
  Group = -> [Sketch133,Sketch135,Sketch134,Fusion001,Mirror019,Mirror020,Extrude015,Extrude016,Extrude104,Extrude103,Array031,AngleSteel004,Compound027]
  Origin = -> Origin065
  Placement = pos=(-6500,1450,484) rot=(0,0,1;0rad)
  expr: .Placement.Base.x = -<<Spreadsheet_support>>.L0 / 2
  expr: .Placement.Base.y = <<Spreadsheet_feedWell>>.dia / 2 + 100
  expr: .Placement.Base.z = 534 - (<<Spreadsheet_support>>.H0 - 700)
FEATURE [Part::Mirroring] Mirror012  label="latticeBeam (mirrored)"
  Base = (150,0,334)
  Normal = (0,-1,0)
  Source = -> Part048
FEATURE [Part::FeaturePython] Array032  # Draft array (typed FeaturePython)
  AlwaysSyncPlacement = false
  Angle = 360
  ArrayType = 0
  Axis = (0,0,1)
  Base = -> ChannelSteel006
  Center = (0,0,0)
  Count = 3
  ExpandArray = false
  Fuse = false
  IntervalAxis = (0,0,0)
  IntervalX = (2000,0,0)
  IntervalY = (0,100,0)
  IntervalZ = (0,0,100)
  NumberCircles = 3
  NumberPolar = 5
  NumberX = 3
  NumberY = 1
  NumberZ = 1
  Placement = pos=(0,0,1186) rot=(0,0,1;0rad)
  PlacementList = 3 placements: arithmetic series from (1520,-1450,0) step (2000,0,0) to (5520,-1450,0)
  RadialDistance = 50
  ScaleList = (3) [(1,1,1),(1,1,1),(1,1,1)]
  Symmetry = 1
  TangentialDistance = 25
FEATURE [Part::Mirroring] Mirror013  label="Array002 (mirrored)"
  Base = (0,0,0)
  Normal = (1,0,0)
  Source = -> Array032
FEATURE [App::Part] Part046  label="centerWellSupport"
  Group = -> [Extrude102,Mirror018,Sketch132,Mirror009,Mirror010,Compound026,AngleSteel003,Mirror011,ChannelSteel006,Part048,Mirror012,Array032,Mirror013]
  Origin = -> Origin063
  Placement = pos=(0,0,-250) rot=(0,0,1;0rad)
  mass = 535.912
  expr: .Placement.Base.z = <<Spreadsheet_feedWell>>.h1 - 1250
FEATURE [App::Part] Part047  label="feedWell"
  Group = -> [Part046,Part045,Spreadsheet015,Spreadsheet016]
  Origin = -> Origin064
  Placement = pos=(0,0,3121) rot=(0,0,1;0rad)
FEATURE [Part::FeaturePython] HShapeSteel  # WARN: FeaturePython — macro-defined, semantics opaque (R4)
  B = 200
  H = 294
  L = 5500
  Placement = pos=(0,-500,0) rot=(0,0,1;1.5708rad)
  Solid = false
  g0 = 7.85
  mass = 0
  size = 3
  standard = SS_Medium
  t1 = 8
  t2 = 12
  type = 02_H_Shape
FEATURE [Spreadsheet::Sheet] Spreadsheet017  label="Spreadsheet_bridge"
  cells = A2='tankDia; B2(dia)=13500; A3='bridgeLength; B3(L0)==dia + 600; A4='hight; B4(hight)=500
FEATURE [Part::Extrusion] Extrude105  label="Extrude112"
  Base = -> HShapeSteel
  Dir = (-1,-2e-16,0)
  DirMode = 2
  FaceMakerClass = Part::FaceMakerBullseye
  FaceMakerMode = 3
  LengthFwd = 14100
  LengthRev = 0
  Solid = false
  Symmetric = true
  expr: LengthFwd = Spreadsheet017.L0
FEATURE [Part::FeaturePython] Clone019  label="Extrude113"  # Draft clone (typed FeaturePython)
  AttacherType = Attacher::AttachEngine3D
  Fuse = false
  Objects = -> [Extrude105]
  Placement = pos=(0,800,0) rot=(0,0,1;0rad)
  Scale = (1,1,1)
  expr: .Placement.Base.y = 1000 - HShapeSteel.B
FEATURE [Part::FeaturePython] ChannelSteel007  # WARN: FeaturePython — macro-defined, semantics opaque (R4)
  B = 75
  H = 150
  L = 5500
  Placement = pos=(-1000,0,0) rot=(0,0,1;0rad)
  Solid = false
  g0 = 7.85
  mass = 0
  size = 3
  standard = SS
  t1 = 6.5
  t2 = 10
  type = 01_Channel
FEATURE [Sketcher::SketchObject] Sketch136
  ArcFitTolerance = 1e-06
  FullyConstrained = true
  MakeInternals = false
  sketch-geometry (5):
    g0: LineSegment StartX=-1000 StartY=-1000 StartZ=0 EndX=1000 EndY=-1000 EndZ=0
    g1: LineSegment StartX=1000 StartY=-1000 StartZ=0 EndX=1000 EndY=1000 EndZ=0
    g2: LineSegment StartX=1000 StartY=1000 StartZ=0 EndX=-1000 EndY=1000 EndZ=0
    g3: LineSegment StartX=-1000 StartY=1000 StartZ=0 EndX=-1000 EndY=-1000 EndZ=0
    g4: GeomPoint [constr] X=0 Y=0 Z=0
  constraints (12):
    c: Coincident(g0,g1)
    c: Coincident(g1,g2)
    c: Coincident(g2,g3)
    c: Coincident(g3,g0)
    c: Horizontal(g0)
    c: Horizontal(g2)
    c: Vertical(g1)
    c: Vertical(g3)
    c: Symmetric(g2,g0,g4)
    c: Coincident(g4,g-1)
    c: DistanceX(g2,g2) = 2000
    c: DistanceY(g3,g3) = 2000
FEATURE [Part::Sweep] Sweep011
  Frenet = true
  Placement = pos=(0,0,144) rot=(0,0,1;0rad)
  Sections = -> [ChannelSteel007]
  Solid = true
  Spine = -> Sketch136 [Edge4,Edge3,Edge2,Edge1]
  Transition = 1
FEATURE [Part::FeaturePython] AngleSteel019  # WARN: FeaturePython — macro-defined, semantics opaque (R4)
  A = 65
  B = 65
  L = 5500
  Placement = pos=(-6800,0,0) rot=(0,0,1;0rad)
  Solid = false
  g0 = 7.85
  mass = 0
  size = 8
  standard = SS_Equal
  t = 6
  type = 00_Angle
FEATURE [Part::FeaturePython] AngleSteel020  # WARN: FeaturePython — macro-defined, semantics opaque (R4)
  A = 65
  B = 65
  L = 5500
  Placement = pos=(-6800,0,294) rot=(0,1,0;1.5708rad)
  Solid = false
  g0 = 7.85
  mass = 0
  size = 8
  standard = SS_Equal
  t = 6
  type = 00_Angle
FEATURE [Part::Extrusion] Extrude106  label="Extrude114"
  Base = -> AngleSteel020
  Dir = (0,1,0)
  DirMode = 2
  FaceMakerClass = Part::FaceMakerBullseye
  FaceMakerMode = 3
  LengthFwd = 600
  LengthRev = 0
  Solid = false
  Symmetric = true
  expr: LengthFwd = 1000 - HShapeSteel.B * 2
FEATURE [Part::Extrusion] Extrude107  label="Extrude115"
  Base = -> AngleSteel019
  Dir = (0,1,0)
  DirMode = 2
  FaceMakerClass = Part::FaceMakerBullseye
  FaceMakerMode = 3
  LengthFwd = 600
  LengthRev = 0
  Solid = false
  Symmetric = true
  expr: LengthFwd = 1000 - HShapeSteel.B * 2
FEATURE [Part::Compound] Compound028
  Links = -> [Extrude106,Extrude107]
FEATURE [Part::FeaturePython] Array033  # Draft array (typed FeaturePython)
  AlwaysSyncPlacement = false
  Angle = 360
  ArrayType = 0
  Axis = (0,0,1)
  Base = -> Compound028
  Center = (0,0,0)
  Count = 3
  ExpandArray = false
  Fuse = false
  IntervalAxis = (0,0,0)
  IntervalX = (2000,0,0)
  IntervalY = (0,100,0)
  IntervalZ = (0,0,100)
  NumberCircles = 3
  NumberPolar = 5
  NumberX = 3
  NumberY = 1
  NumberZ = 1
  PlacementList = 3 placements: arithmetic series from (0,0,0) step (2000,0,0) to (4000,0,0)
  RadialDistance = 50
  ScaleList = (3) [(1,1,1),(1,1,1),(1,1,1)]
  Symmetry = 1
  TangentialDistance = 25
FEATURE [Part::Mirroring] Mirror021  label="Array (mirrored)"
  Base = (0,2000,0)
  Normal = (1,0,0)
  Source = -> Array033
FEATURE [Sketcher::SketchObject] Sketch137
  ArcFitTolerance = 1e-06
  AttachmentSupport = -> [Extrude105]
  FullyConstrained = true
  MakeInternals = false
  MapMode = 5
  Placement = pos=(0,0,294) rot=(0,0,1;0rad)
  expr: Constraints[25] = Spreadsheet017.dia + 600
  sketch-geometry (12):
    g0: LineSegment StartX=-7050 StartY=500 StartZ=0 EndX=-1000 EndY=500 EndZ=0
    g1: LineSegment StartX=-1000 StartY=500 StartZ=0 EndX=-1000 EndY=1000 EndZ=0
    g2: LineSegment StartX=-1000 StartY=1000 StartZ=0 EndX=1000 EndY=1000 EndZ=0
    g3: LineSegment StartX=1000 StartY=1000 StartZ=0 EndX=1000 EndY=500 EndZ=0
    g4: LineSegment StartX=1000 StartY=500 StartZ=0 EndX=7050 EndY=500 EndZ=0
    g5: LineSegment StartX=7050 StartY=500 StartZ=0 EndX=7050 EndY=-500 EndZ=0
    g6: LineSegment StartX=7050 StartY=-500 StartZ=0 EndX=1000 EndY=-500 EndZ=0
    g7: LineSegment StartX=1000 StartY=-500 StartZ=0 EndX=1000 EndY=-1000 EndZ=0
    g8: LineSegment StartX=1000 StartY=-1000 StartZ=0 EndX=-1000 EndY=-1000 EndZ=0
    g9: LineSegment StartX=-1000 StartY=-1000 StartZ=0 EndX=-1000 EndY=-500 EndZ=0
    g10: LineSegment StartX=-1000 StartY=-500 StartZ=0 EndX=-7050 EndY=-500 EndZ=0
    g11: LineSegment StartX=-7050 StartY=-500 StartZ=0 EndX=-7050 EndY=500 EndZ=0
  constraints (33):
    c: Horizontal(g0)
    c: Coincident(g0,g1)
    c: Vertical(g1)
    c: Coincident(g1,g2)
    c: Horizontal(g2)
    c: Coincident(g2,g3)
    c: Vertical(g3)
    c: Coincident(g3,g4)
    c: Horizontal(g4)
    c: Coincident(g4,g5)
    c: Vertical(g5)
    c: Coincident(g5,g6)
    c: Horizontal(g6)
    c: Coincident(g6,g7)
    c: Vertical(g7)
    c: Coincident(g7,g8)
    c: Coincident(g8,g9)
    c: Vertical(g9)
    c: Coincident(g9,g10)
    c: Horizontal(g10)
    c: Coincident(g10,g11)
    c: Coincident(g11,g0)
    c: Symmetric(g10,g0,g-1)
    c: DistanceY(g11,g11) = 1000
    c: Symmetric(g10,g5,g-2)
    c: DistanceX(g10,g5) = 14100
    c: Horizontal(g0,g3)
    c: Vertical(g0,g9)
    c: DistanceX(g8,g8) = 2000
    c: Symmetric(g8,g7,g-2)
    c: Vertical(g6,g3)
    c: DistanceY(g7,g2) = 2000
    c: Distance(g7,g-1) = 1000
FEATURE [Part::Extrusion] Extrude108  label="Extrude116"
  Base = -> Sketch137
  Dir = (0,0,1)
  DirMode = 2
  FaceMakerClass = Part::FaceMakerBullseye
  FaceMakerMode = 3
  LengthFwd = 4.5
  LengthRev = 0
  Solid = true
  Symmetric = false
FEATURE [Part::Compound] Compound029  label="Compound001"
  Links = -> [Mirror021,Array033]
FEATURE [Part::FeaturePython] ChannelSteel001  # WARN: FeaturePython — macro-defined, semantics opaque (R4)
  B = 75
  H = 150
  L = 5500
  Placement = pos=(250,0,0) rot=(0,0,1;0rad)
  Solid = false
  g0 = 7.85
  mass = 0
  size = 3
  standard = SS
  t1 = 6.5
  t2 = 10
  type = 01_Channel
FEATURE [Part::Extrusion] Extrude109  label="Extrude117"
  Base = -> ChannelSteel001
  Dir = (0,1,0)
  DirMode = 2
  FaceMakerClass = Part::FaceMakerBullseye
  FaceMakerMode = 3
  LengthFwd = 600
  LengthRev = 0
  Placement = pos=(0,0,144) rot=(0,0,1;0rad)
  Solid = false
  Symmetric = true
  expr: LengthFwd = 1000 - HShapeSteel.B * 2
FEATURE [Part::FeaturePython] Array001  label="Array034"  # Draft array (typed FeaturePython)
  AlwaysSyncPlacement = false
  Angle = 360
  ArrayType = 1
  Axis = (0,0,1)
  Base = -> Extrude109
  Center = (0,0,0)
  Count = 2
  ExpandArray = false
  Fuse = false
  IntervalAxis = (0,0,0)
  IntervalX = (50,0,0)
  IntervalY = (0,50,0)
  IntervalZ = (0,0,50)
  NumberCircles = 3
  NumberPolar = 2
  NumberX = 2
  NumberY = 2
  NumberZ = 1
  PlacementList = 2 placements: [(0,0,144),(0,0,144)]
  RadialDistance = 50
  ScaleList = (2) [(1,1,1),(1,1,1)]
  Symmetry = 1
  TangentialDistance = 25
FEATURE [Sketcher::SketchObject] Sketch138
  ArcFitTolerance = 1e-06
  AttachmentSupport = -> [Extrude108]
  FullyConstrained = true
  MakeInternals = false
  MapMode = 5
  Placement = pos=(0,0,298.5) rot=(0,0,1;0rad)
  sketch-geometry (4):
    g0: LineSegment StartX=6800 StartY=500 StartZ=0 EndX=8110 EndY=500 EndZ=0
    g1: LineSegment StartX=8110 StartY=500 StartZ=0 EndX=8110 EndY=-500 EndZ=0
    g2: LineSegment StartX=8110 StartY=-500 StartZ=0 EndX=6800 EndY=-500 EndZ=0
    g3: LineSegment StartX=6800 StartY=-500 StartZ=0 EndX=6800 EndY=500 EndZ=0
  constraints (10):
    c: Horizontal(g0)
    c: Coincident(g0,g1)
    c: Vertical(g1)
    c: Coincident(g1,g2)
    c: Horizontal(g2)
    c: Coincident(g0,g-3)
    c: Coincident(g2,g-3)
    c: DistanceX(g2,g2) = 1310
    c: Coincident(g3,g2)
    c: Coincident(g3,g0)
FEATURE [Part::FeaturePython] ChannelSteel002  # WARN: FeaturePython — macro-defined, semantics opaque (R4)
  B = 75
  H = 150
  L = 5500
  Placement = pos=(8110,0,294) rot=(0,1,0;3.14159rad)
  Solid = false
  g0 = 7.85
  mass = 0
  size = 3
  standard = SS
  t1 = 6.5
  t2 = 10
  type = 01_Channel
FEATURE [Part::Sweep] Sweep012  label="Sweep001"
  Frenet = true
  Sections = -> [ChannelSteel002]
  Solid = true
  Spine = -> Sketch138 [Edge3,Edge2,Edge1,Edge4]
  Transition = 1
FEATURE [Sketcher::SketchObject] Sketch139
  ArcFitTolerance = 1e-06
  AttachmentSupport = -> [Sweep012]
  ExternalGeometry = -> [Sweep012,Sketch138]
  FullyConstrained = true
  MakeInternals = false
  MapMode = 5
  Placement = pos=(0,3.53e-14,294) rot=(0,0,1;0rad)
  sketch-geometry (9):
    g0: LineSegment StartX=6850 StartY=-450 StartZ=0 EndX=8060 EndY=-450 EndZ=0
    g1: LineSegment StartX=8060 StartY=-450 StartZ=0 EndX=8060 EndY=450 EndZ=0
    g2: LineSegment StartX=8060 StartY=450 StartZ=0 EndX=6850 EndY=450 EndZ=0
    g3: LineSegment StartX=6850 StartY=450 StartZ=0 EndX=6850 EndY=-450 EndZ=0
    g4: GeomPoint [constr] X=7455 Y=2.715e-13 Z=0
    g5: LineSegment StartX=6800 StartY=-500 StartZ=0 EndX=8110 EndY=-500 EndZ=0
    g6: LineSegment StartX=8110 StartY=-500 StartZ=0 EndX=8110 EndY=500 EndZ=0
    g7: LineSegment StartX=8110 StartY=500 StartZ=0 EndX=6800 EndY=500 EndZ=0
    g8: LineSegment StartX=6800 StartY=500 StartZ=0 EndX=6800 EndY=-500 EndZ=0
  constraints (23):
    c: Coincident(g0,g1)
    c: Coincident(g1,g2)
    c: Coincident(g2,g3)
    c: Coincident(g3,g0)
    c: Horizontal(g0)
    c: Horizontal(g2)
    c: Vertical(g1)
    c: Vertical(g3)
    c: Symmetric(g2,g0,g4)
    c: DistanceY(g0,g-4) = 25
    c: Distance(g-4,g3) = 25
    c: DistanceY(g-3,g1) = 25
    c: DistanceX(g-3,g1) = 25
    c: Coincident(g5,g6)
    c: Coincident(g6,g7)
    c: Coincident(g7,g8)
    c: Coincident(g8,g5)
    c: Horizontal(g5)
    c: Horizontal(g7)
    c: Vertical(g6)
    c: Vertical(g8)
    c: Coincident(g-6,g6)
    c: Coincident(g-5,g5)
FEATURE [Part::Extrusion] Extrude110  label="Extrude118"
  Base = -> Sketch139
  Dir = (0,0,1)
  DirMode = 2
  FaceMakerClass = Part::FaceMakerBullseye
  FaceMakerMode = 3
  LengthFwd = 4.5
  LengthRev = 0
  Solid = true
  Symmetric = false
FEATURE [Sketcher::SketchObject] Sketch140
  ArcFitTolerance = 1e-06
  AttachmentSupport = -> [XY_Plane067]
  FullyConstrained = true
  MakeInternals = false
  MapMode = 5
  sketch-geometry (5):
    g0: LineSegment StartX=-302.5 StartY=-450 StartZ=0 EndX=302.5 EndY=-450 EndZ=0
    g1: LineSegment StartX=302.5 StartY=-450 StartZ=0 EndX=302.5 EndY=450 EndZ=0
    g2: LineSegment StartX=302.5 StartY=450 StartZ=0 EndX=-302.5 EndY=450 EndZ=0
    g3: LineSegment StartX=-302.5 StartY=450 StartZ=0 EndX=-302.5 EndY=-450 EndZ=0
    g4: GeomPoint [constr] X=0 Y=0 Z=0
  constraints (12):
    c: Coincident(g0,g1)
    c: Coincident(g1,g2)
    c: Coincident(g2,g3)
    c: Coincident(g3,g0)
    c: Horizontal(g0)
    c: Horizontal(g2)
    c: Vertical(g1)
    c: Vertical(g3)
    c: Symmetric(g2,g0,g4)
    c: Coincident(g4,g-1)
    c: DistanceY(g3,g3) = 900
    c: DistanceX(g2,g2) = 605
FEATURE [Sketcher::SketchObject] Sketch141
  ArcFitTolerance = 1e-06
  AttachmentSupport = -> [XY_Plane067]
  ExternalGeometry = -> [Sketch140]
  FullyConstrained = true
  MakeInternals = false
  MapMode = 5
  sketch-geometry (5):
    g0: LineSegment StartX=-272.5 StartY=-420 StartZ=0 EndX=272.5 EndY=-420 EndZ=0
    g1: LineSegment StartX=272.5 StartY=-420 StartZ=0 EndX=272.5 EndY=420 EndZ=0
    g2: LineSegment StartX=272.5 StartY=420 StartZ=0 EndX=-272.5 EndY=420 EndZ=0
    g3: LineSegment StartX=-272.5 StartY=420 StartZ=0 EndX=-272.5 EndY=-420 EndZ=0
    g4: GeomPoint [constr] X=0 Y=0 Z=0
  constraints (12):
    c: Coincident(g0,g1)
    c: Coincident(g1,g2)
    c: Coincident(g2,g3)
    c: Coincident(g3,g0)
    c: Horizontal(g0)
    c: Horizontal(g2)
    c: Vertical(g1)
    c: Vertical(g3)
    c: Symmetric(g2,g0,g4)
    c: Coincident(g4,g-1)
    c: DistanceX(g1,g-3) = 30
    c: DistanceY(g1,g-3) = 30
FEATURE [Part::FeaturePython] AngleSteel021  # WARN: FeaturePython — macro-defined, semantics opaque (R4)
  A = 50
  B = 50
  L = 5500
  Placement = pos=(275,0,3.74e-14) rot=(0,1,0;3.14159rad)
  Solid = false
  g0 = 7.85
  mass = 0
  size = 6
  standard = SS_Equal
  t = 4
  type = 00_Angle
FEATURE [Part::Extrusion] Extrude111  label="Extrude119"
  Base = -> Sketch140
  Dir = (0,0,1)
  DirMode = 2
  FaceMakerClass = Part::FaceMakerBullseye
  FaceMakerMode = 3
  LengthFwd = 4.5
  LengthRev = 0
  Solid = true
  Symmetric = false
FEATURE [Part::Sweep] Sweep002
  Frenet = true
  Sections = -> [AngleSteel021]
  Solid = true
  Spine = -> Sketch141 [Edge2,Edge3,Edge4,Edge1]
  Transition = 1
FEATURE [PartDesign::FeatureBase] BaseFeature
  BaseFeature = -> Extrude111
  Suppressed = false
FEATURE [Sketcher::SketchObject] Sketch142
  ArcFitTolerance = 1e-06
  AttachmentSupport = -> [BaseFeature]
  FullyConstrained = true
  MakeInternals = false
  MapMode = 5
  Placement = pos=(0,0,4.5) rot=(0,0,1;0rad)
  sketch-geometry (8):
    g0: LineSegment StartX=-48.25 StartY=225 StartZ=0 EndX=48.25 EndY=225 EndZ=0
    g1: LineSegment StartX=48.25 StartY=225 StartZ=0 EndX=48.25 EndY=265 EndZ=0
    g2: LineSegment StartX=48.25 StartY=265 StartZ=0 EndX=-48.25 EndY=265 EndZ=0
    g3: LineSegment StartX=-48.25 StartY=265 StartZ=0 EndX=-48.25 EndY=225 EndZ=0
    g4: LineSegment StartX=-48.25 StartY=-265 StartZ=0 EndX=48.25 EndY=-265 EndZ=0
    g5: LineSegment StartX=48.25 StartY=-265 StartZ=0 EndX=48.25 EndY=-225 EndZ=0
    g6: LineSegment StartX=48.25 StartY=-225 StartZ=0 EndX=-48.25 EndY=-225 EndZ=0
    g7: LineSegment StartX=-48.25 StartY=-225 StartZ=0 EndX=-48.25 EndY=-265 EndZ=0
  constraints (23):
    c: Coincident(g0,g1)
    c: Coincident(g1,g2)
    c: Coincident(g2,g3)
    c: Coincident(g3,g0)
    c: Horizontal(g2)
    c: Vertical(g1)
    c: Vertical(g3)
    c: Coincident(g4,g5)
    c: Coincident(g5,g6)
    c: Coincident(g6,g7)
    c: Coincident(g7,g4)
    c: Horizontal(g4)
    c: Horizontal(g6)
    c: Vertical(g5)
    c: Vertical(g7)
    c: DistanceX(g2,g2) = 96.5
    c: DistanceY(g1,g1) = 40
    c: Vertical(g0,g6)
    c: Vertical(g0,g5)
    c: Symmetric(g0,g0,g-2)
    c: DistanceY(g-1,g0) = 225
    c: DistanceY(g5,g5) = 40
    c: DistanceY(g5,g-1) = 225
FEATURE [PartDesign::Pocket] Pocket003
  BaseFeature = -> BaseFeature
  Direction = (0,0,-1)
  Length = 5
  Length2 = 5
  Profile = -> Sketch142
  ReferenceAxis = -> Sketch142 [N_Axis]
  Suppressed = false
  Type = 0
FEATURE [PartDesign::Body] Body010
  AllowCompound = false
  BaseFeature = -> Extrude111
  Group = -> [BaseFeature,Sketch142,Pocket003]
  Origin = -> Origin067
  Tip = -> Pocket003
FEATURE [Part::Feature] Part__Feature028  label="AP-268-2\X\96{\X\91\X\CC__\X\C3\X\DE\X\CC\X\AB\X\D9\X\\\\C005"
  Placement = pos=(1044.74,-585.443,742.289) rot=(0,0,1;0rad)
  shape: bbox 104.7 x 52.9 x 35.45 mm, 341 faces (baked)
FEATURE [App::Part] AP_268_2_black_v004  label="AP-268-2-black v004"
  Group = -> [Part__Feature028]
  Origin = -> Origin068
  Placement = pos=(-154,-42.5,-734) rot=(0,0,1;0rad)
FEATURE [Part::FeaturePython] Array034  label="Array035"  # Draft array (typed FeaturePython)
  AlwaysSyncPlacement = false
  Angle = 360
  ArrayType = 1
  Axis = (0,0,1)
  Base = -> AP_268_2_black_v004
  Center = (0,0,0)
  Count = 2
  ExpandArray = false
  Fuse = false
  IntervalAxis = (0,0,0)
  IntervalX = (50,0,0)
  IntervalY = (0,50,0)
  IntervalZ = (0,0,50)
  NumberCircles = 3
  NumberPolar = 2
  NumberX = 2
  NumberY = 2
  NumberZ = 1
  PlacementList = 2 placements: [(-154,-42.5,-734),(154,42.5,-734)]
  RadialDistance = 50
  ScaleList = (2) [(1,1,1),(1,1,1)]
  Symmetry = 1
  TangentialDistance = 25
FEATURE [Part::FeaturePython] Channel  # WARN: FeaturePython — macro-defined, semantics opaque (R4)
  Placement = pos=(0,-975,298.5) rot=(0,0,1;0rad)
  Reverse = false
  g0 = 7.85
  h = 1100
  k = 90
  l1 = 975
  l2 = 249
  p = 500
  spec = 0
  type = 6
FEATURE [Part::FeaturePython] Corner_with_end001  # WARN: FeaturePython — macro-defined, semantics opaque (R4)
  Placement = pos=(-6985.5,-474.5,299) rot=(0,0,1;0rad)
  Reverse = false
  g0 = 7.85
  h = 1100
  k = -90
  l1 = 6010
  l2 = 249
  p = 500
  spec = 0
  type = 1
  expr: .Placement.Base.x = -6735.5 - (Spreadsheet017.dia - 13000) / 2
  expr: l1 = 5760 + (Spreadsheet017.dia - 13000) / 2
FEATURE [Part::Compound] Compound030  label="Compound003"
  Links = -> [Sweep002,Extrude111,Body010,Array034]
  Placement = pos=(250,0,0) rot=(0,0,1;0rad)
  expr: .Placement.Base.x = (Spreadsheet017.dia - 13000) / 2
FEATURE [App::Part] Part002  label="inspectionCover"
  Group = -> [Sketch140,Sketch141,Sweep002,AngleSteel021,Extrude111,Body010,AP_268_2_black_v004,Array034,Compound030]
  Origin = -> Origin003
  Placement = pos=(7758,0,294) rot=(0,0,1;0rad)
FEATURE [Part::FeaturePython] Clone020  label="inspectionCover001"  # Draft clone (typed FeaturePython)
  AttacherType = Attacher::AttachEngine3D
  Fuse = false
  Objects = -> [Part002]
  Placement = pos=(7153,0,294) rot=(0,0,1;0rad)
  Scale = (1,1,1)
FEATURE [Part::FeaturePython] Corner_with_end002  # WARN: FeaturePython — macro-defined, semantics opaque (R4)
  Placement = pos=(-6985.5,469.5,299) rot=(0,0,1;0rad)
  Reverse = true
  g0 = 7.85
  h = 1100
  k = 90
  l1 = 6010
  l2 = 249
  p = 500
  spec = 0
  type = 1
  expr: .Placement.Base.x = -6735.5 - (Spreadsheet017.dia - 13000) / 2
  expr: l1 = 5760 + (Spreadsheet017.dia - 13000) / 2
FEATURE [Part::FeaturePython] Channel001  # WARN: FeaturePython — macro-defined, semantics opaque (R4)
  Placement = pos=(0,-975,298.5) rot=(0,0,1;0rad)
  Reverse = false
  g0 = 7.85
  h = 1100
  k = 90
  l1 = 975
  l2 = 249
  p = 500
  spec = 0
  type = 6
FEATURE [Part::FeaturePython] Channel002  # WARN: FeaturePython — macro-defined, semantics opaque (R4)
  Placement = pos=(0,973.5,298.5) rot=(0,0,1;0rad)
  Reverse = true
  g0 = 7.85
  h = 1100
  k = -90
  l1 = 975
  l2 = 249
  p = 500
  spec = 0
  type = 6
FEATURE [Part::FeaturePython] Corner  # WARN: FeaturePython — macro-defined, semantics opaque (R4)
  Placement = pos=(7226,474,298) rot=(0,0,1;3.14159rad)
  Reverse = false
  g0 = 7.85
  h = 1100
  k = -90
  l1 = 6250
  l2 = 240
  p = 500
  spec = 0
  type = 2
  expr: .Placement.Base.x = 6976 + (Spreadsheet017.dia - 13000) / 2
  expr: l1 = 6000 + (Spreadsheet017.dia - 13000) / 2
FEATURE [Part::FeaturePython] Corner_with_end003  # WARN: FeaturePython — macro-defined, semantics opaque (R4)
  Placement = pos=(8335,-434.5,299) rot=(0,0,1;1.5708rad)
  Reverse = false
  g0 = 7.85
  h = 1100
  k = 90
  l1 = 910
  l2 = 1102
  p = 1000
  spec = 0
  type = 1
  expr: .Placement.Base.x = 8085 + (Spreadsheet017.dia - 13000) / 2
FEATURE [Part::FeaturePython] SquarePipe001  # WARN: FeaturePython — macro-defined, semantics opaque (R4)
  A = 200
  B = 200
  L = 206
  Placement = pos=(0,0,-200) rot=(0,0,1;0rad)
  Solid = true
  g0 = 7.85
  mass = 7.3793
  size = 44
  standard = SS
  t = 4.5
  type = 10_Square_Pipe
  expr: .Placement.Base.z = -(Spreadsheet017.hight - 294) + 6
  expr: L = <<Spreadsheet_bridge>>.hight - 294
FEATURE [Sketcher::SketchObject] Sketch143
  ArcFitTolerance = 1e-06
  AttachmentSupport = -> [SquarePipe001]
  ExternalGeometry = -> [SquarePipe001]
  FullyConstrained = true
  MakeInternals = false
  MapMode = 5
  Placement = pos=(0,0,-200) rot=(1,0,0;3.14159rad)
  sketch-geometry (9):
    g0: LineSegment StartX=-138 StartY=-150 StartZ=0 EndX=138 EndY=-150 EndZ=0
    g1: LineSegment StartX=138 StartY=-150 StartZ=0 EndX=138 EndY=150 EndZ=0
    g2: LineSegment StartX=138 StartY=150 StartZ=0 EndX=-138 EndY=150 EndZ=0
    g3: LineSegment StartX=-138 StartY=150 StartZ=0 EndX=-138 EndY=-150 EndZ=0
    g4: GeomPoint [constr] X=-2e-16 Y=3e-16 Z=0
    g5: Circle CenterX=-113 CenterY=125 CenterZ=0 NormalX=0 NormalY=0 NormalZ=1 AngleXU=0 Radius=10
    g6: Circle CenterX=-113 CenterY=-125 CenterZ=0 NormalX=0 NormalY=0 NormalZ=1 AngleXU=0 Radius=10
    g7: Circle CenterX=113 CenterY=-125 CenterZ=0 NormalX=0 NormalY=0 NormalZ=1 AngleXU=0 Radius=10
    g8: Circle CenterX=113 CenterY=125 CenterZ=0 NormalX=0 NormalY=0 NormalZ=1 AngleXU=0 Radius=10
  constraints (24):
    c: Coincident(g0,g1)
    c: Coincident(g1,g2)
    c: Coincident(g2,g3)
    c: Coincident(g3,g0)
    c: Horizontal(g0)
    c: Horizontal(g2)
    c: Vertical(g1)
    c: Vertical(g3)
    c: Symmetric(g2,g0,g4)
    c: Coincident(g4,g-1)
    c: DistanceY(g-3,g1) = 50
    c: DistanceX(g-5,g0) = 50
    c: Diameter(g5) = 20
    c: Equal(g5,g6)
    c: Equal(g6,g7)
    c: Equal(g7,g8)
    c: Vertical(g5,g6)
    c: Vertical(g8,g7)
    c: Horizontal(g5,g8)
    c: Horizontal(g6,g7)
    c: DistanceY(g5,g2) = 25
    c: DistanceX(g2,g5) = 25
    c: DistanceX(g8,g1) = 25
    c: DistanceY(g0,g7) = 25
FEATURE [PartDesign::Pad] Pad003  label="plt"
  Direction = (0,0,-1)
  Length = 9
  Length2 = 10
  Placement = pos=(0,0,-200) rot=(0,0,1;0rad)
  Profile = -> Sketch143
  ReferenceAxis = -> Sketch143 [N_Axis]
  Refine = true
  Reversed = true
  Suppressed = false
  Type = 0
FEATURE [Sketcher::SketchObject] Sketch144
  ArcFitTolerance = 1e-06
  AttachmentSupport = -> [SquarePipe001]
  ExternalGeometry = -> [SquarePipe001]
  FullyConstrained = true
  MakeInternals = false
  MapMode = 5
  Placement = pos=(0,0,6) rot=(0,0,1;0rad)
  sketch-geometry (13):
    g0: LineSegment StartX=-88 StartY=-100 StartZ=0 EndX=88 EndY=-100 EndZ=0
    g1: LineSegment StartX=100 StartY=-88 StartZ=0 EndX=100 EndY=88 EndZ=0
    g2: LineSegment StartX=88 StartY=100 StartZ=0 EndX=-88 EndY=100 EndZ=0
    g3: LineSegment StartX=-100 StartY=88 StartZ=0 EndX=-100 EndY=-88 EndZ=0
    g4: GeomPoint [constr] X=0 Y=0 Z=0
    g5: ArcOfCircle CenterX=88 CenterY=88 CenterZ=0 NormalX=0 NormalY=0 NormalZ=1 AngleXU=0 Radius=12 StartAngle=1e-16 EndAngle=1.5708
    g6: GeomPoint [constr] X=100 Y=100 Z=0
    g7: ArcOfCircle CenterX=-88 CenterY=88 CenterZ=0 NormalX=0 NormalY=0 NormalZ=1 AngleXU=0 Radius=12 StartAngle=1.5708 EndAngle=3.14159
    g8: GeomPoint [constr] X=-100 Y=100 Z=0
    g9: ArcOfCircle CenterX=-88 CenterY=-88 CenterZ=0 NormalX=0 NormalY=0 NormalZ=1 AngleXU=0 Radius=12 StartAngle=3.14159 EndAngle=4.71239
    g10: GeomPoint [constr] X=-100 Y=-100 Z=0
    g11: ArcOfCircle CenterX=88 CenterY=-88 CenterZ=0 NormalX=0 NormalY=0 NormalZ=1 AngleXU=0 Radius=12 StartAngle=4.71239 EndAngle=6.28319
    g12: GeomPoint [constr] X=100 Y=-100 Z=0
  constraints (28):
    c: Horizontal(g0)
    c: Horizontal(g2)
    c: Vertical(g1)
    c: Vertical(g3)
    c: Symmetric(g6,g10,g4)
    c: Coincident(g4,g-1)
    c: PointOnObject(g-4,g2)
    c: PointOnObject(g-3,g1)
    c: PointOnObject(g6,g2)
    c: PointOnObject(g6,g1)
    c: Tangent(g2,g5) = -1.5708
    c: Tangent(g1,g5) = -1.5708
    c: PointOnObject(g8,g2)
    c: PointOnObject(g8,g3)
    c: Tangent(g2,g7) = -1.5708
    c: Tangent(g3,g7) = -1.5708
    c: PointOnObject(g10,g0)
    c: PointOnObject(g10,g3)
    c: Tangent(g0,g9) = -1.5708
    c: Tangent(g3,g9) = -1.5708
    c: Equal(g5,g-5)
    c: PointOnObject(g12,g1)
    c: PointOnObject(g12,g0)
    c: Tangent(g1,g11) = -1.5708
    c: Tangent(g0,g11) = -1.5708
    c: Equal(g5,g7)
    c: Equal(g7,g9)
    c: Equal(g9,g11)
FEATURE [Part::Extrusion] Extrude112  label="Extrude120"
  Base = -> Sketch144
  Dir = (0,0,1)
  DirMode = 2
  FaceMakerClass = Part::FaceMakerBullseye
  FaceMakerMode = 3
  LengthFwd = 9
  LengthRev = 0
  Reversed = true
  Solid = true
  Symmetric = false
FEATURE [Part::MultiFuse] Fusion012  label="Pst_SQ"
  Refine = true
  Shapes = -> [SquarePipe001,Pad003,Extrude112]
FEATURE [App::Part] Part050  label="pst_SQ"
  Group = -> [Sketch144,SquarePipe001,Sketch143,Pad003,Extrude112,Fusion012]
  Origin = -> Origin069
  Placement = pos=(-6950,-400,0) rot=(0,0,1;0rad)
  expr: .Placement.Base.x = -Spreadsheet017.L0 / 2 + 100
  expr: .Placement.Base.y = -400
FEATURE [Part::FeaturePython] Array035  label="Array003"  # Draft array (typed FeaturePython)
  AlwaysSyncPlacement = false
  Angle = 360
  ArrayType = 0
  Axis = (0,0,1)
  Base = -> Part050
  Center = (0,0,0)
  Count = 4
  ExpandArray = false
  Fuse = false
  IntervalAxis = (0,0,0)
  IntervalX = (13900,0,0)
  IntervalY = (0,800,0)
  IntervalZ = (0,0,100)
  NumberCircles = 3
  NumberPolar = 5
  NumberX = 2
  NumberY = 2
  NumberZ = 1
  Placement = pos=(0,0,-6) rot=(0,0,1;0rad)
  PlacementList = 4 placements: [(-6950,-400,0),(-6950,400,0),(6950,-400,0),(6950,400,0)]
  RadialDistance = 50
  ScaleList = (4) [(1,1,1),(1,1,1),(1,1,1),(1,1,1)]
  Symmetry = 1
  TangentialDistance = 25
  expr: .IntervalX.x = Spreadsheet017.L0 - 200
FEATURE [Part::Compound] Compound031  label="Compound004"
  Links = -> [Sweep012,Extrude110]
  Placement = pos=(250,0,0) rot=(0,0,1;0rad)
  expr: .Placement.Base.x = (Spreadsheet017.dia - 13000) / 2
FEATURE [Sketcher::SketchObject] Sketch145
  ArcFitTolerance = 1e-06
  AttachmentSupport = -> [Extrude105]
  FullyConstrained = true
  MakeInternals = false
  MapMode = 5
  Placement = pos=(0,0,294) rot=(0,0,1;0rad)
  expr: Constraints[9] = Spreadsheet017.L0 / 2
  sketch-geometry (3):
    g0: LineSegment StartX=7050 StartY=-400 StartZ=0 EndX=7050 EndY=-900 EndZ=0
    g1: LineSegment StartX=7050 StartY=-900 StartZ=0 EndX=5550 EndY=-900 EndZ=0
    g2: LineSegment StartX=5550 StartY=-900 StartZ=0 EndX=5550 EndY=-400 EndZ=0
  constraints (10):
    c: Coincident(g0,g1)
    c: Horizontal(g1)
    c: Coincident(g1,g2)
    c: Vertical(g2)
    c: Vertical(g0)
    c: Horizontal(g2,g0)
    c: DistanceX(g1,g1) = 1500
    c: DistanceY(g1,g-1) = 900
    c: DistanceY(g2,g2) = 500
    c: DistanceX(g-1,g0) = 7050
FEATURE [Part::FeaturePython] ChannelSteel003  # WARN: FeaturePython — macro-defined, semantics opaque (R4)
  B = 75
  H = 150
  L = 5500
  Placement = pos=(5550,-800,140) rot=(0,0,1;0rad)
  Solid = false
  g0 = 7.85
  mass = 0
  size = 3
  standard = SS
  t1 = 6.5
  t2 = 10
  type = 01_Channel
  expr: .Placement.Base.x = Spreadsheet017.dia / 2 - 1200
FEATURE [Sketcher::SketchObject] Sketch146
  ArcFitTolerance = 1e-06
  FullyConstrained = true
  MakeInternals = false
  MapMode = 5
  Placement = pos=(0,3.55e-14,290) rot=(0,0,1;0rad)
  expr: Constraints[10] = Spreadsheet017.L0 / 2
  sketch-geometry (4):
    g0: LineSegment StartX=5550 StartY=-900 StartZ=0 EndX=7050 EndY=-900 EndZ=0
    g1: LineSegment StartX=7050 StartY=-500 StartZ=0 EndX=5550 EndY=-500 EndZ=0
    g2: LineSegment StartX=5550 StartY=-500 StartZ=0 EndX=5550 EndY=-900 EndZ=0
    g3: LineSegment StartX=7050 StartY=-500 StartZ=0 EndX=7050 EndY=-900 EndZ=0
  constraints (12):
    c: Coincident(g1,g2)
    c: Coincident(g2,g0)
    c: Horizontal(g0)
    c: DistanceX(g0,g0) = 1500
    c: Distance(g0,g-1) = 900
    c: Coincident(g3,g1)
    c: Coincident(g3,g0)
    c: Vertical(g3)
    c: Vertical(g2)
    c: Horizontal(g1)
    c: DistanceX(g-1,g0) = 7050
    c: DistanceY(g0,g1) = 400
FEATURE [Part::FeaturePython] Channel003  # WARN: FeaturePython — macro-defined, semantics opaque (R4)
  Placement = pos=(6300,-874.78,298) rot=(0,0,1;0rad)
  Reverse = false
  g0 = 7.85
  h = 1100
  k = 90
  l1 = 725
  l2 = 249
  p = 500
  spec = 0
  type = 6
  expr: .Placement.Base.x = Spreadsheet017.L0 / 2 - 750
FEATURE [Part::FeaturePython] Corner001  # WARN: FeaturePython — macro-defined, semantics opaque (R4)
  Placement = pos=(3125.34,-469.24,299) rot=(0,0,1;0rad)
  Reverse = false
  g0 = 7.85
  h = 1100
  k = -90
  l1 = 2450
  l2 = 150
  p = 500
  spec = 0
  type = 2
  expr: l1 = 2200 + (Spreadsheet017.dia - 13000) / 2
FEATURE [Part::FeaturePython] Corner002  # WARN: FeaturePython — macro-defined, semantics opaque (R4)
  Placement = pos=(3123.18,-468.54,298) rot=(0,0,1;3.14159rad)
  Reverse = true
  g0 = 7.85
  h = 1100
  k = 90
  l1 = 2150
  l2 = 249
  p = 500
  spec = 0
  type = 2
FEATURE [Part::FeaturePython] Edge_R  # WARN: FeaturePython — macro-defined, semantics opaque (R4)
  Placement = pos=(7025,-565.122,298.5) rot=(0,0,1;1.5708rad)
  Reverse = true
  g0 = 7.85
  h = 1100
  p = 500
  spec = 0
  type = 4
  expr: .Placement.Base.x = Spreadsheet017.L0 / 2 - 25
FEATURE [App::Part] Part003  label="handrail"
  Group = -> [Channel,Corner_with_end001,Corner_with_end002,Channel001,Channel002,Corner,Corner_with_end003,Array035,Channel003,Corner001,Corner002,Edge_R]
  Origin = -> Origin005
FEATURE [Part::Sweep] Sweep003
  Frenet = true
  Sections = -> [ChannelSteel003]
  Solid = true
  Spine = -> Sketch145 [Edge3,Edge2,Edge1]
  Transition = 1
FEATURE [Part::Extrusion] Extrude113  label="Extrude121"
  Base = -> Sketch146
  Dir = (0,0,1)
  DirMode = 2
  FaceMakerClass = Part::FaceMakerBullseye
  FaceMakerMode = 3
  LengthFwd = 4.5
  LengthRev = 0
  Solid = true
  Symmetric = false
FEATURE [Part::MultiFuse] Fusion013
  Shapes = -> [Extrude108,Extrude105,Compound029,Sweep011,Clone019,Array001,Extrude113,Sweep003]
FEATURE [App::Part] Part049  label="bridge_s"
  Group = -> [Spreadsheet017,AngleSteel019,AngleSteel020,Extrude106,Extrude107,Compound028,ChannelSteel001,Extrude109,Sketch138,ChannelSteel002,Sweep012,Sketch139,Extrude110,Part002,Clone020,Part003,Compound031,Extrude108,Extrude105,Sweep011,Array033,HShapeSteel,Clone019,ChannelSteel007,Array001,Sketch137,Compound029,Sketch136,Mirror021,Fusion013]
  Origin = -> Origin066
  Placement = pos=(0,0,5621) rot=(0,0,1;0rad)
  mass = 3136.49
FEATURE [Sketcher::SketchObject] Sketch147
  ArcFitTolerance = 1e-06
  FullyConstrained = true
  MakeInternals = false
  Placement = pos=(0,0,0) rot=(1,0,0;1.5708rad)
  expr: Constraints[5] = <<Spreadsheet_Assy>>.dia / 2 + 400 + 200 + 150
  sketch-geometry (7):
    g0: LineSegment StartX=0 StartY=0 StartZ=0 EndX=1664.7 EndY=605.901 EndZ=0
    g1: LineSegment StartX=1737.38 StartY=622.497 StartZ=0 EndX=6485.07 EndY=1098.5 EndZ=0
    g2: LineSegment StartX=6515 StartY=1100 StartZ=0 EndX=7500 EndY=1100 EndZ=0
    g3: ArcOfCircle CenterX=1767.31 CenterY=323.993 CenterZ=0 NormalX=0 NormalY=0 NormalZ=1 AngleXU=0 Radius=300 StartAngle=1.67072 EndAngle=1.91986
    g4: GeomPoint [constr] X=1700 Y=618.749 Z=0
    g5: ArcOfCircle CenterX=6515 CenterY=800 CenterZ=0 NormalX=0 NormalY=0 NormalZ=1 AngleXU=0 Radius=300 StartAngle=1.5708 EndAngle=1.67072
    g6: GeomPoint [constr] X=6500 Y=1100 Z=0
  constraints (17):
    c: Coincident(g-1,g0)
    c: Horizontal(g2)
    c: Angle(g-1,g0) = 0.349066
    c: DistanceX(g6,g2) = 1000
    c: DistanceX(g0,g4) = 1700
    c: DistanceX(g0,g2) = 7500
    c: PointOnObject(g4,g0)
    c: PointOnObject(g4,g1)
    c: Tangent(g0,g3) = 1.5708
    c: Tangent(g1,g3) = 1.5708
    c: PointOnObject(g6,g1)
    c: PointOnObject(g6,g2)
    c: Tangent(g1,g5) = 1.5708
    c: Tangent(g2,g5) = 1.5708
    c: Radius(g3) = 300
    c: Radius(g5) = 300
    c: DistanceY(g0,g2) = 1100
FEATURE [Part::Part2DObjectPython] Circle  # Draft 2D object (typed FeaturePython)
  Area = 21382.5
  FirstAngle = 0
  LastAngle = 0
  MakeFace = true
  Placement = pos=(7500,-2.4e-13,1100) rot=(0,1,0;1.5708rad)
  Radius = 82.5
FEATURE [Part::Sweep] Sweep013
  Frenet = true
  Sections = -> [Circle]
  Solid = true
  Spine = -> Sketch147 [Edge5,Edge4,Edge3,Edge2,Edge1]
  Transition = 1
FEATURE [Part::Part2DObjectPython] Circle001  # Draft 2D object (typed FeaturePython)
  Area = 18385.4
  FirstAngle = 0
  LastAngle = 0
  MakeFace = true
  Placement = pos=(7500,0,1100) rot=(0,1,0;1.5708rad)
  Radius = 76.5
  expr: .Placement.Base.x = <<Spreadsheet_Assy>>.dia / 2 + 750
FEATURE [Part::Sweep] Sweep014
  Frenet = true
  Sections = -> [Circle001]
  Solid = true
  Spine = -> Sweep013 [Edge10,Edge8,Edge6,Edge4,Edge1]
  Transition = 1
FEATURE [Part::Cut] Cut038
  Base = -> Sweep013
  Tool = -> Sweep014
FEATURE [Part::FeaturePython] Flange001  # WARN: FeaturePython — macro-defined, semantics opaque (R4)
  Placement = pos=(7500,0,1100) rot=(0,1,0;4.71239rad)
  dia = 3
  fittings = 00_Flange
  material = 0
  standard = 1
  expr: .Placement.Base.x = <<Spreadsheet_Assy>>.dia / 2 + 750
FEATURE [Part::Part2DObjectPython] Wire  # Draft 2D object (typed FeaturePython)
  Area = 522106
  ChamferSize = 0
  Closed = true
  End = (1.33926,5.68e-14,-223.082)
  FilletRadius = 0
  Length = 3013.47
  MakeFace = true
  Placement = pos=(-5.05626,-1.421e-13,659.485) rot=(1,0,0;1.5708rad)
  Points = (4) [(0,0,0),(767.45,0,0),(422.098,-882.568,-3.94921e-13),(6.39552,-882.568,-3.94921e-13)]
  Start = (-5.05626,-1.421e-13,659.485)
  Subdivisions = 0
FEATURE [Part::Revolution] Revolve016
  Angle = 360
  Axis = (-0.0072463,-2e-16,0.999974)
  AxisLink = -> Wire [Edge4]
  Base = (-5.05626,-1.421e-13,659.485)
  FaceMakerClass = Part::FaceMakerBullseye
  Solid = true
  Source = -> Wire
  Symmetric = false
FEATURE [Part::Cut] Cut039
  Base = -> Cut038
  Tool = -> Revolve016
FEATURE [App::Part] Part051  label="sludgePipe"
  Group = -> [Flange001,Wire,Sweep014,Sweep013,Circle001,Circle,Revolve016,Cut038,Sketch147,Cut039]
  Origin = -> Origin070
  mass = 172.279
FEATURE [App::Part] Part052  label="buffle"
  Group = -> [AngleSteel001,Revolve001,Revolve002,Sketch016,Compound004,Array003]
  Origin = -> Origin071
  mass = 651.705
FEATURE [App::Part] Part004  label="buffleAssy"
  Group = -> [Spreadsheet001,Revolve,Array002,Sketch014,Sketch017,Sketch015,Cut001,Extrude007,Extrude006,AngleSteel002,Mirror002,Compound003,Part052]
  Origin = -> Origin008
  Placement = pos=(0,0,4717) rot=(0,0,1;0rad)
FEATURE [App::Part] Part037  label="suspendAssy13.5m"
  Group = -> [Part001,Part004,Single_flange_straight_pipe001,Part017,Part035,Part036,Part038,Spreadsheet014,_X2_7D426C888EAF4F5353F3_X0__1100_v12,Part047,Part049,Part051]
  Origin = -> Origin050
FEATURE [Spreadsheet::Sheet] Parts_List
  cells = A1='No; B1='Name; C1='Standard; D1='Count; E1='Unit[kg]; F1='Mass[kg]; A2=1; B2='mainShaftBrg; D2=1; E2=9.64; F2=9.64; A3=2; B3='skimmerBrade; D3=1; E3=61.35; F3=61.35; A4=3; B4='Single_flange_straight_pipe001; C4=300; D4=1; E4=44.67; F4=44.67; A5=4; B5='skimmerBrg; D5=1; E5=72.01; F5=72.01; A6=5; B6='pipeSkimmerBody; D6=1; E6=274.65; F6=274.65; A7=6; B7='pipeSkimmerRod; D7=1; E7=5.81; F7=5.81; A8=7; B8='pipeSkimmerControlDevice; D8=1; E8=120; F8=120; A9=8; B9='pipeSkimmerRod001; D9=1; E9=5.73; F9=5.73; A10=9; B10='rakeAssy; D10=2; E10=530.34; F10=1060.67; A11=10; B11='__basic; D11=1; E11=288.54; F11=288.54; A12=11; B12='DriveSystem; D12=1; E12=1145.89; F12=1145.89; A13=12; B13='inflowPipe; D13=1; E13=627.65; F13=627.65; A14=13; B14='mainShaft; D14=1; E14=321.2; F14=321.2; A15=14; B15='centerWell; D15=1; E15=783.91; F15=783.91; A16=15; B16='centerWellSupport; D16=1; E16=535.91; F16=535.91; A17=16; B17='bridge_s; D17=1; E17=3136.49; F17=3136.49; A18=17; B18='sludgePipe; D18=1; E18=172.28; F18=172.28; A19=18; B19='buffle; D19=1; E19=651.7; F19=651.7; F20=9318.1
